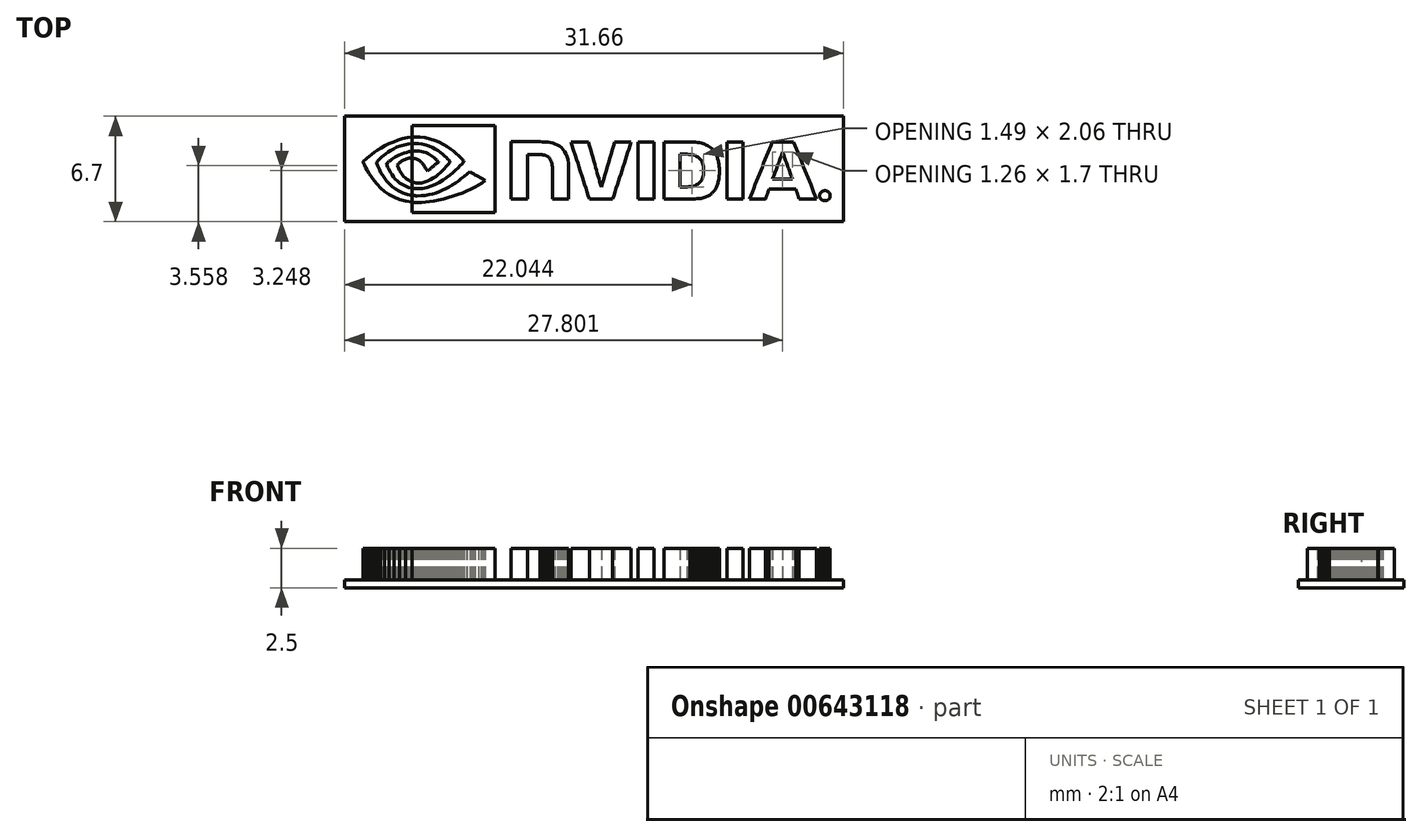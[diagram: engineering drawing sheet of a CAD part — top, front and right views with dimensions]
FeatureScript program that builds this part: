
annotation { "Feature Type Name" : "Feature", "Feature Type Description" : "" }
export const myFeature = defineFeature(function(context is Context, id is Id, definition is map)
    precondition{}
    {
        {
            var Q0;
            Q0=qCreatedBy(makeId("Top.planeOp"),FACE);
            var sketch = newSketch(context, id + "F0", { "sketchPlane" : qUnion([Q0])});
            skLineSegment(sketch, "E0", {"start": v(15, -1.7) * mm, "end": v(15, -1.67) * mm});
            skLineSegment(sketch, "E1", {"start": v(15, -1.67) * mm, "end": v(15, -1.63) * mm});
            skLineSegment(sketch, "E2", {"start": v(15, -1.63) * mm, "end": v(14.98, -1.6) * mm});
            skLineSegment(sketch, "E3", {"start": v(14.98, -1.6) * mm, "end": v(14.97, -1.57) * mm});
            skLineSegment(sketch, "E4", {"start": v(14.97, -1.57) * mm, "end": v(14.96, -1.54) * mm});
            skLineSegment(sketch, "E5", {"start": v(14.96, -1.54) * mm, "end": v(14.94, -1.51) * mm});
            skLineSegment(sketch, "E6", {"start": v(14.94, -1.51) * mm, "end": v(14.92, -1.49) * mm});
            skLineSegment(sketch, "E7", {"start": v(14.92, -1.49) * mm, "end": v(14.9, -1.47) * mm});
            skLineSegment(sketch, "E8", {"start": v(14.9, -1.47) * mm, "end": v(14.88, -1.45) * mm});
            skLineSegment(sketch, "E9", {"start": v(14.88, -1.45) * mm, "end": v(14.85, -1.43) * mm});
            skLineSegment(sketch, "E10", {"start": v(14.85, -1.43) * mm, "end": v(14.82, -1.42) * mm});
            skLineSegment(sketch, "E11", {"start": v(14.82, -1.42) * mm, "end": v(14.8, -1.4) * mm});
            skLineSegment(sketch, "E12", {"start": v(14.8, -1.4) * mm, "end": v(14.76, -1.4) * mm});
            skLineSegment(sketch, "E13", {"start": v(14.76, -1.4) * mm, "end": v(14.73, -1.39) * mm});
            skLineSegment(sketch, "E14", {"start": v(14.73, -1.39) * mm, "end": v(14.7, -1.38) * mm});
            skLineSegment(sketch, "E15", {"start": v(14.7, -1.38) * mm, "end": v(14.67, -1.38) * mm});
            skLineSegment(sketch, "E16", {"start": v(14.67, -1.38) * mm, "end": v(14.64, -1.38) * mm});
            skLineSegment(sketch, "E17", {"start": v(14.64, -1.38) * mm, "end": v(14.6, -1.39) * mm});
            skLineSegment(sketch, "E18", {"start": v(14.6, -1.39) * mm, "end": v(14.57, -1.4) * mm});
            skLineSegment(sketch, "E19", {"start": v(14.57, -1.4) * mm, "end": v(14.54, -1.4) * mm});
            skLineSegment(sketch, "E20", {"start": v(14.54, -1.4) * mm, "end": v(14.51, -1.42) * mm});
            skLineSegment(sketch, "E21", {"start": v(14.51, -1.42) * mm, "end": v(14.49, -1.43) * mm});
            skLineSegment(sketch, "E22", {"start": v(14.49, -1.43) * mm, "end": v(14.46, -1.45) * mm});
            skLineSegment(sketch, "E23", {"start": v(14.46, -1.45) * mm, "end": v(14.44, -1.47) * mm});
            skLineSegment(sketch, "E24", {"start": v(14.44, -1.47) * mm, "end": v(14.41, -1.49) * mm});
            skLineSegment(sketch, "E25", {"start": v(14.41, -1.49) * mm, "end": v(14.4, -1.51) * mm});
            skLineSegment(sketch, "E26", {"start": v(14.4, -1.51) * mm, "end": v(14.38, -1.54) * mm});
            skLineSegment(sketch, "E27", {"start": v(14.38, -1.54) * mm, "end": v(14.36, -1.57) * mm});
            skLineSegment(sketch, "E28", {"start": v(14.36, -1.57) * mm, "end": v(14.35, -1.6) * mm});
            skLineSegment(sketch, "E29", {"start": v(14.35, -1.6) * mm, "end": v(14.34, -1.63) * mm});
            skLineSegment(sketch, "E30", {"start": v(14.34, -1.63) * mm, "end": v(14.34, -1.67) * mm});
            skLineSegment(sketch, "E31", {"start": v(14.34, -1.67) * mm, "end": v(14.34, -1.7) * mm});
            skLineSegment(sketch, "E32", {"start": v(14.34, -1.7) * mm, "end": v(14.34, -1.74) * mm});
            skLineSegment(sketch, "E33", {"start": v(14.34, -1.74) * mm, "end": v(14.34, -1.77) * mm});
            skLineSegment(sketch, "E34", {"start": v(14.34, -1.77) * mm, "end": v(14.35, -1.8) * mm});
            skLineSegment(sketch, "E35", {"start": v(14.35, -1.8) * mm, "end": v(14.36, -1.84) * mm});
            skLineSegment(sketch, "E36", {"start": v(14.36, -1.84) * mm, "end": v(14.38, -1.87) * mm});
            skLineSegment(sketch, "E37", {"start": v(14.38, -1.87) * mm, "end": v(14.4, -1.9) * mm});
            skLineSegment(sketch, "E38", {"start": v(14.4, -1.9) * mm, "end": v(14.41, -1.92) * mm});
            skLineSegment(sketch, "E39", {"start": v(14.41, -1.92) * mm, "end": v(14.44, -1.94) * mm});
            skLineSegment(sketch, "E40", {"start": v(14.44, -1.94) * mm, "end": v(14.46, -1.96) * mm});
            skLineSegment(sketch, "E41", {"start": v(14.46, -1.96) * mm, "end": v(14.49, -1.97) * mm});
            skLineSegment(sketch, "E42", {"start": v(14.49, -1.97) * mm, "end": v(14.51, -1.99) * mm});
            skLineSegment(sketch, "E43", {"start": v(14.51, -1.99) * mm, "end": v(14.54, -2) * mm});
            skLineSegment(sketch, "E44", {"start": v(14.54, -2) * mm, "end": v(14.57, -2) * mm});
            skLineSegment(sketch, "E45", {"start": v(14.57, -2) * mm, "end": v(14.6, -2.02) * mm});
            skLineSegment(sketch, "E46", {"start": v(14.6, -2.02) * mm, "end": v(14.64, -2.02) * mm});
            skLineSegment(sketch, "E47", {"start": v(14.64, -2.02) * mm, "end": v(14.67, -2.02) * mm});
            skLineSegment(sketch, "E48", {"start": v(14.67, -2.02) * mm, "end": v(14.7, -2.02) * mm});
            skLineSegment(sketch, "E49", {"start": v(14.7, -2.02) * mm, "end": v(14.73, -2.02) * mm});
            skLineSegment(sketch, "E50", {"start": v(14.73, -2.02) * mm, "end": v(14.76, -2) * mm});
            skLineSegment(sketch, "E51", {"start": v(14.76, -2) * mm, "end": v(14.8, -2) * mm});
            skLineSegment(sketch, "E52", {"start": v(14.8, -2) * mm, "end": v(14.82, -1.99) * mm});
            skLineSegment(sketch, "E53", {"start": v(14.82, -1.99) * mm, "end": v(14.85, -1.97) * mm});
            skLineSegment(sketch, "E54", {"start": v(14.85, -1.97) * mm, "end": v(14.88, -1.96) * mm});
            skLineSegment(sketch, "E55", {"start": v(14.88, -1.96) * mm, "end": v(14.9, -1.94) * mm});
            skLineSegment(sketch, "E56", {"start": v(14.9, -1.94) * mm, "end": v(14.92, -1.92) * mm});
            skLineSegment(sketch, "E57", {"start": v(14.92, -1.92) * mm, "end": v(14.94, -1.9) * mm});
            skLineSegment(sketch, "E58", {"start": v(14.94, -1.9) * mm, "end": v(14.96, -1.87) * mm});
            skLineSegment(sketch, "E59", {"start": v(14.96, -1.87) * mm, "end": v(14.97, -1.84) * mm});
            skLineSegment(sketch, "E60", {"start": v(14.97, -1.84) * mm, "end": v(14.98, -1.8) * mm});
            skLineSegment(sketch, "E61", {"start": v(14.98, -1.8) * mm, "end": v(15, -1.77) * mm});
            skLineSegment(sketch, "E62", {"start": v(15, -1.77) * mm, "end": v(15, -1.74) * mm});
            skLineSegment(sketch, "E63", {"start": v(15, -1.74) * mm, "end": v(15, -1.7) * mm});
            skLineSegment(sketch, "E64", {"start": v(2.8, 1.72) * mm, "end": v(2.8, 1.5) * mm});
            skLineSegment(sketch, "E65", {"start": v(2.8, 1.5) * mm, "end": v(2.8, 1.27) * mm});
            skLineSegment(sketch, "E66", {"start": v(2.8, 1.27) * mm, "end": v(2.8, 1.04) * mm});
            skLineSegment(sketch, "E67", {"start": v(2.8, 1.04) * mm, "end": v(2.8, 0.81) * mm});
            skLineSegment(sketch, "E68", {"start": v(2.8, 0.81) * mm, "end": v(2.8, 0.59) * mm});
            skLineSegment(sketch, "E69", {"start": v(2.8, 0.59) * mm, "end": v(2.8, 0.36) * mm});
            skLineSegment(sketch, "E70", {"start": v(2.8, 0.36) * mm, "end": v(2.8, 0.13) * mm});
            skLineSegment(sketch, "E71", {"start": v(2.8, 0.13) * mm, "end": v(2.8, -0.1) * mm});
            skLineSegment(sketch, "E72", {"start": v(2.8, -0.1) * mm, "end": v(2.8, -0.32) * mm});
            skLineSegment(sketch, "E73", {"start": v(2.8, -0.32) * mm, "end": v(2.8, -0.55) * mm});
            skLineSegment(sketch, "E74", {"start": v(2.8, -0.55) * mm, "end": v(2.8, -0.78) * mm});
            skLineSegment(sketch, "E75", {"start": v(2.8, -0.78) * mm, "end": v(2.8, -1) * mm});
            skLineSegment(sketch, "E76", {"start": v(2.8, -1) * mm, "end": v(2.8, -1.23) * mm});
            skLineSegment(sketch, "E77", {"start": v(2.8, -1.23) * mm, "end": v(2.8, -1.46) * mm});
            skLineSegment(sketch, "E78", {"start": v(2.8, -1.46) * mm, "end": v(2.8, -1.68) * mm});
            skLineSegment(sketch, "E79", {"start": v(2.8, -1.68) * mm, "end": v(2.8, -1.91) * mm});
            skLineSegment(sketch, "E80", {"start": v(2.8, -1.91) * mm, "end": v(2.86, -1.91) * mm});
            skLineSegment(sketch, "E81", {"start": v(2.86, -1.91) * mm, "end": v(2.93, -1.91) * mm});
            skLineSegment(sketch, "E82", {"start": v(2.93, -1.91) * mm, "end": v(3, -1.91) * mm});
            skLineSegment(sketch, "E83", {"start": v(3, -1.91) * mm, "end": v(3.06, -1.91) * mm});
            skLineSegment(sketch, "E84", {"start": v(3.06, -1.91) * mm, "end": v(3.12, -1.91) * mm});
            skLineSegment(sketch, "E85", {"start": v(3.12, -1.91) * mm, "end": v(3.18, -1.91) * mm});
            skLineSegment(sketch, "E86", {"start": v(3.18, -1.91) * mm, "end": v(3.25, -1.91) * mm});
            skLineSegment(sketch, "E87", {"start": v(3.25, -1.91) * mm, "end": v(3.31, -1.91) * mm});
            skLineSegment(sketch, "E88", {"start": v(3.31, -1.91) * mm, "end": v(3.38, -1.91) * mm});
            skLineSegment(sketch, "E89", {"start": v(3.38, -1.91) * mm, "end": v(3.44, -1.91) * mm});
            skLineSegment(sketch, "E90", {"start": v(3.44, -1.91) * mm, "end": v(3.5, -1.91) * mm});
            skLineSegment(sketch, "E91", {"start": v(3.5, -1.91) * mm, "end": v(3.57, -1.91) * mm});
            skLineSegment(sketch, "E92", {"start": v(3.57, -1.91) * mm, "end": v(3.63, -1.91) * mm});
            skLineSegment(sketch, "E93", {"start": v(3.63, -1.91) * mm, "end": v(3.7, -1.91) * mm});
            skLineSegment(sketch, "E94", {"start": v(3.7, -1.91) * mm, "end": v(3.76, -1.91) * mm});
            skLineSegment(sketch, "E95", {"start": v(3.76, -1.91) * mm, "end": v(3.82, -1.91) * mm});
            skLineSegment(sketch, "E96", {"start": v(3.82, -1.91) * mm, "end": v(3.82, -1.68) * mm});
            skLineSegment(sketch, "E97", {"start": v(3.82, -1.68) * mm, "end": v(3.82, -1.46) * mm});
            skLineSegment(sketch, "E98", {"start": v(3.82, -1.46) * mm, "end": v(3.82, -1.23) * mm});
            skLineSegment(sketch, "E99", {"start": v(3.82, -1.23) * mm, "end": v(3.82, -1) * mm});
            skLineSegment(sketch, "E100", {"start": v(3.82, -1) * mm, "end": v(3.82, -0.78) * mm});
            skLineSegment(sketch, "E101", {"start": v(3.82, -0.78) * mm, "end": v(3.82, -0.55) * mm});
            skLineSegment(sketch, "E102", {"start": v(3.82, -0.55) * mm, "end": v(3.82, -0.32) * mm});
            skLineSegment(sketch, "E103", {"start": v(3.82, -0.32) * mm, "end": v(3.82, -0.1) * mm});
            skLineSegment(sketch, "E104", {"start": v(3.82, -0.1) * mm, "end": v(3.82, 0.13) * mm});
            skLineSegment(sketch, "E105", {"start": v(3.82, 0.13) * mm, "end": v(3.82, 0.36) * mm});
            skLineSegment(sketch, "E106", {"start": v(3.82, 0.36) * mm, "end": v(3.82, 0.59) * mm});
            skLineSegment(sketch, "E107", {"start": v(3.82, 0.59) * mm, "end": v(3.82, 0.81) * mm});
            skLineSegment(sketch, "E108", {"start": v(3.82, 0.81) * mm, "end": v(3.82, 1.04) * mm});
            skLineSegment(sketch, "E109", {"start": v(3.82, 1.04) * mm, "end": v(3.82, 1.27) * mm});
            skLineSegment(sketch, "E110", {"start": v(3.82, 1.27) * mm, "end": v(3.82, 1.5) * mm});
            skLineSegment(sketch, "E111", {"start": v(3.82, 1.5) * mm, "end": v(3.82, 1.72) * mm});
            skLineSegment(sketch, "E112", {"start": v(3.82, 1.72) * mm, "end": v(3.76, 1.72) * mm});
            skLineSegment(sketch, "E113", {"start": v(3.76, 1.72) * mm, "end": v(3.7, 1.72) * mm});
            skLineSegment(sketch, "E114", {"start": v(3.7, 1.72) * mm, "end": v(3.63, 1.72) * mm});
            skLineSegment(sketch, "E115", {"start": v(3.63, 1.72) * mm, "end": v(3.57, 1.72) * mm});
            skLineSegment(sketch, "E116", {"start": v(3.57, 1.72) * mm, "end": v(3.5, 1.72) * mm});
            skLineSegment(sketch, "E117", {"start": v(3.5, 1.72) * mm, "end": v(3.44, 1.72) * mm});
            skLineSegment(sketch, "E118", {"start": v(3.44, 1.72) * mm, "end": v(3.37, 1.72) * mm});
            skLineSegment(sketch, "E119", {"start": v(3.37, 1.72) * mm, "end": v(3.31, 1.72) * mm});
            skLineSegment(sketch, "E120", {"start": v(3.31, 1.72) * mm, "end": v(3.25, 1.72) * mm});
            skLineSegment(sketch, "E121", {"start": v(3.25, 1.72) * mm, "end": v(3.18, 1.72) * mm});
            skLineSegment(sketch, "E122", {"start": v(3.18, 1.72) * mm, "end": v(3.12, 1.72) * mm});
            skLineSegment(sketch, "E123", {"start": v(3.12, 1.72) * mm, "end": v(3.05, 1.72) * mm});
            skLineSegment(sketch, "E124", {"start": v(3.05, 1.72) * mm, "end": v(3, 1.72) * mm});
            skLineSegment(sketch, "E125", {"start": v(3, 1.72) * mm, "end": v(2.93, 1.72) * mm});
            skLineSegment(sketch, "E126", {"start": v(2.93, 1.72) * mm, "end": v(2.86, 1.72) * mm});
            skLineSegment(sketch, "E127", {"start": v(2.86, 1.72) * mm, "end": v(2.8, 1.72) * mm});
            skLineSegment(sketch, "E128", {"start": v(-5.27, 1.73) * mm, "end": v(-5.27, 1.5) * mm});
            skLineSegment(sketch, "E129", {"start": v(-5.27, 1.5) * mm, "end": v(-5.27, 1.27) * mm});
            skLineSegment(sketch, "E130", {"start": v(-5.27, 1.27) * mm, "end": v(-5.27, 1.04) * mm});
            skLineSegment(sketch, "E131", {"start": v(-5.27, 1.04) * mm, "end": v(-5.27, 0.82) * mm});
            skLineSegment(sketch, "E132", {"start": v(-5.27, 0.82) * mm, "end": v(-5.27, 0.59) * mm});
            skLineSegment(sketch, "E133", {"start": v(-5.27, 0.59) * mm, "end": v(-5.27, 0.36) * mm});
            skLineSegment(sketch, "E134", {"start": v(-5.27, 0.36) * mm, "end": v(-5.27, 0.14) * mm});
            skLineSegment(sketch, "E135", {"start": v(-5.27, 0.14) * mm, "end": v(-5.27, -0.1) * mm});
            skLineSegment(sketch, "E136", {"start": v(-5.27, -0.1) * mm, "end": v(-5.27, -0.32) * mm});
            skLineSegment(sketch, "E137", {"start": v(-5.27, -0.32) * mm, "end": v(-5.27, -0.55) * mm});
            skLineSegment(sketch, "E138", {"start": v(-5.27, -0.55) * mm, "end": v(-5.27, -0.77) * mm});
            skLineSegment(sketch, "E139", {"start": v(-5.27, -0.77) * mm, "end": v(-5.27, -1) * mm});
            skLineSegment(sketch, "E140", {"start": v(-5.27, -1) * mm, "end": v(-5.27, -1.23) * mm});
            skLineSegment(sketch, "E141", {"start": v(-5.27, -1.23) * mm, "end": v(-5.27, -1.46) * mm});
            skLineSegment(sketch, "E142", {"start": v(-5.27, -1.46) * mm, "end": v(-5.27, -1.68) * mm});
            skLineSegment(sketch, "E143", {"start": v(-5.27, -1.68) * mm, "end": v(-5.27, -1.91) * mm});
            skLineSegment(sketch, "E144", {"start": v(-5.27, -1.91) * mm, "end": v(-5.2, -1.91) * mm});
            skLineSegment(sketch, "E145", {"start": v(-5.2, -1.91) * mm, "end": v(-5.14, -1.91) * mm});
            skLineSegment(sketch, "E146", {"start": v(-5.14, -1.91) * mm, "end": v(-5.07, -1.91) * mm});
            skLineSegment(sketch, "E147", {"start": v(-5.07, -1.91) * mm, "end": v(-5, -1.91) * mm});
            skLineSegment(sketch, "E148", {"start": v(-5, -1.91) * mm, "end": v(-4.94, -1.91) * mm});
            skLineSegment(sketch, "E149", {"start": v(-4.94, -1.91) * mm, "end": v(-4.88, -1.91) * mm});
            skLineSegment(sketch, "E150", {"start": v(-4.88, -1.91) * mm, "end": v(-4.82, -1.91) * mm});
            skLineSegment(sketch, "E151", {"start": v(-4.82, -1.91) * mm, "end": v(-4.75, -1.91) * mm});
            skLineSegment(sketch, "E152", {"start": v(-4.75, -1.91) * mm, "end": v(-4.69, -1.91) * mm});
            skLineSegment(sketch, "E153", {"start": v(-4.69, -1.91) * mm, "end": v(-4.62, -1.91) * mm});
            skLineSegment(sketch, "E154", {"start": v(-4.62, -1.91) * mm, "end": v(-4.56, -1.91) * mm});
            skLineSegment(sketch, "E155", {"start": v(-4.56, -1.91) * mm, "end": v(-4.5, -1.91) * mm});
            skLineSegment(sketch, "E156", {"start": v(-4.5, -1.91) * mm, "end": v(-4.43, -1.91) * mm});
            skLineSegment(sketch, "E157", {"start": v(-4.43, -1.91) * mm, "end": v(-4.36, -1.91) * mm});
            skLineSegment(sketch, "E158", {"start": v(-4.36, -1.91) * mm, "end": v(-4.3, -1.91) * mm});
            skLineSegment(sketch, "E159", {"start": v(-4.3, -1.91) * mm, "end": v(-4.23, -1.91) * mm});
            skLineSegment(sketch, "E160", {"start": v(-4.23, -1.91) * mm, "end": v(-4.23, -1.73) * mm});
            skLineSegment(sketch, "E161", {"start": v(-4.23, -1.73) * mm, "end": v(-4.23, -1.56) * mm});
            skLineSegment(sketch, "E162", {"start": v(-4.23, -1.56) * mm, "end": v(-4.23, -1.38) * mm});
            skLineSegment(sketch, "E163", {"start": v(-4.23, -1.38) * mm, "end": v(-4.23, -1.2) * mm});
            skLineSegment(sketch, "E164", {"start": v(-4.23, -1.2) * mm, "end": v(-4.23, -1.03) * mm});
            skLineSegment(sketch, "E165", {"start": v(-4.23, -1.03) * mm, "end": v(-4.23, -0.85) * mm});
            skLineSegment(sketch, "E166", {"start": v(-4.23, -0.85) * mm, "end": v(-4.23, -0.68) * mm});
            skLineSegment(sketch, "E167", {"start": v(-4.23, -0.68) * mm, "end": v(-4.23, -0.5) * mm});
            skLineSegment(sketch, "E168", {"start": v(-4.23, -0.5) * mm, "end": v(-4.23, -0.32) * mm});
            skLineSegment(sketch, "E169", {"start": v(-4.23, -0.32) * mm, "end": v(-4.23, -0.15) * mm});
            skLineSegment(sketch, "E170", {"start": v(-4.23, -0.15) * mm, "end": v(-4.23, 0.03) * mm});
            skLineSegment(sketch, "E171", {"start": v(-4.23, 0.03) * mm, "end": v(-4.23, 0.2) * mm});
            skLineSegment(sketch, "E172", {"start": v(-4.23, 0.2) * mm, "end": v(-4.23, 0.38) * mm});
            skLineSegment(sketch, "E173", {"start": v(-4.23, 0.38) * mm, "end": v(-4.23, 0.56) * mm});
            skLineSegment(sketch, "E174", {"start": v(-4.23, 0.56) * mm, "end": v(-4.23, 0.74) * mm});
            skLineSegment(sketch, "E175", {"start": v(-4.23, 0.74) * mm, "end": v(-4.23, 0.91) * mm});
            skLineSegment(sketch, "E176", {"start": v(-4.23, 0.91) * mm, "end": v(-4.18, 0.91) * mm});
            skLineSegment(sketch, "E177", {"start": v(-4.18, 0.91) * mm, "end": v(-4.13, 0.91) * mm});
            skLineSegment(sketch, "E178", {"start": v(-4.13, 0.91) * mm, "end": v(-4.08, 0.91) * mm});
            skLineSegment(sketch, "E179", {"start": v(-4.08, 0.91) * mm, "end": v(-4.03, 0.91) * mm});
            skLineSegment(sketch, "E180", {"start": v(-4.03, 0.91) * mm, "end": v(-3.98, 0.91) * mm});
            skLineSegment(sketch, "E181", {"start": v(-3.98, 0.91) * mm, "end": v(-3.93, 0.91) * mm});
            skLineSegment(sketch, "E182", {"start": v(-3.93, 0.91) * mm, "end": v(-3.88, 0.91) * mm});
            skLineSegment(sketch, "E183", {"start": v(-3.88, 0.91) * mm, "end": v(-3.83, 0.91) * mm});
            skLineSegment(sketch, "E184", {"start": v(-3.83, 0.91) * mm, "end": v(-3.78, 0.91) * mm});
            skLineSegment(sketch, "E185", {"start": v(-3.78, 0.91) * mm, "end": v(-3.73, 0.91) * mm});
            skLineSegment(sketch, "E186", {"start": v(-3.73, 0.91) * mm, "end": v(-3.68, 0.91) * mm});
            skLineSegment(sketch, "E187", {"start": v(-3.68, 0.91) * mm, "end": v(-3.63, 0.91) * mm});
            skLineSegment(sketch, "E188", {"start": v(-3.63, 0.91) * mm, "end": v(-3.58, 0.9) * mm});
            skLineSegment(sketch, "E189", {"start": v(-3.58, 0.9) * mm, "end": v(-3.53, 0.9) * mm});
            skLineSegment(sketch, "E190", {"start": v(-3.53, 0.9) * mm, "end": v(-3.48, 0.9) * mm});
            skLineSegment(sketch, "E191", {"start": v(-3.48, 0.9) * mm, "end": v(-3.43, 0.9) * mm});
            skLineSegment(sketch, "E192", {"start": v(-3.43, 0.9) * mm, "end": v(-3.38, 0.9) * mm});
            skLineSegment(sketch, "E193", {"start": v(-3.38, 0.9) * mm, "end": v(-3.33, 0.9) * mm});
            skLineSegment(sketch, "E194", {"start": v(-3.33, 0.9) * mm, "end": v(-3.29, 0.9) * mm});
            skLineSegment(sketch, "E195", {"start": v(-3.29, 0.9) * mm, "end": v(-3.24, 0.9) * mm});
            skLineSegment(sketch, "E196", {"start": v(-3.24, 0.9) * mm, "end": v(-3.2, 0.9) * mm});
            skLineSegment(sketch, "E197", {"start": v(-3.2, 0.9) * mm, "end": v(-3.16, 0.88) * mm});
            skLineSegment(sketch, "E198", {"start": v(-3.16, 0.88) * mm, "end": v(-3.12, 0.87) * mm});
            skLineSegment(sketch, "E199", {"start": v(-3.12, 0.87) * mm, "end": v(-3.09, 0.86) * mm});
            skLineSegment(sketch, "E200", {"start": v(-3.09, 0.86) * mm, "end": v(-3.05, 0.85) * mm});
            skLineSegment(sketch, "E201", {"start": v(-3.05, 0.85) * mm, "end": v(-3.02, 0.83) * mm});
            skLineSegment(sketch, "E202", {"start": v(-3.02, 0.83) * mm, "end": v(-2.99, 0.82) * mm});
            skLineSegment(sketch, "E203", {"start": v(-2.99, 0.82) * mm, "end": v(-2.96, 0.8) * mm});
            skLineSegment(sketch, "E204", {"start": v(-2.96, 0.8) * mm, "end": v(-2.93, 0.78) * mm});
            skLineSegment(sketch, "E205", {"start": v(-2.93, 0.78) * mm, "end": v(-2.9, 0.76) * mm});
            skLineSegment(sketch, "E206", {"start": v(-2.9, 0.76) * mm, "end": v(-2.87, 0.73) * mm});
            skLineSegment(sketch, "E207", {"start": v(-2.87, 0.73) * mm, "end": v(-2.85, 0.7) * mm});
            skLineSegment(sketch, "E208", {"start": v(-2.85, 0.7) * mm, "end": v(-2.82, 0.68) * mm});
            skLineSegment(sketch, "E209", {"start": v(-2.82, 0.68) * mm, "end": v(-2.8, 0.64) * mm});
            skLineSegment(sketch, "E210", {"start": v(-2.8, 0.64) * mm, "end": v(-2.77, 0.6) * mm});
            skLineSegment(sketch, "E211", {"start": v(-2.77, 0.6) * mm, "end": v(-2.75, 0.56) * mm});
            skLineSegment(sketch, "E212", {"start": v(-2.75, 0.56) * mm, "end": v(-2.72, 0.51) * mm});
            skLineSegment(sketch, "E213", {"start": v(-2.72, 0.51) * mm, "end": v(-2.7, 0.46) * mm});
            skLineSegment(sketch, "E214", {"start": v(-2.7, 0.46) * mm, "end": v(-2.69, 0.41) * mm});
            skLineSegment(sketch, "E215", {"start": v(-2.69, 0.41) * mm, "end": v(-2.67, 0.36) * mm});
            skLineSegment(sketch, "E216", {"start": v(-2.67, 0.36) * mm, "end": v(-2.66, 0.3) * mm});
            skLineSegment(sketch, "E217", {"start": v(-2.66, 0.3) * mm, "end": v(-2.65, 0.23) * mm});
            skLineSegment(sketch, "E218", {"start": v(-2.65, 0.23) * mm, "end": v(-2.64, 0.16) * mm});
            skLineSegment(sketch, "E219", {"start": v(-2.64, 0.16) * mm, "end": v(-2.63, 0.09) * mm});
            skLineSegment(sketch, "E220", {"start": v(-2.63, 0.09) * mm, "end": v(-2.63, 0.01) * mm});
            skLineSegment(sketch, "E221", {"start": v(-2.63, 0.01) * mm, "end": v(-2.62, -0.07) * mm});
            skLineSegment(sketch, "E222", {"start": v(-2.62, -0.07) * mm, "end": v(-2.62, -0.16) * mm});
            skLineSegment(sketch, "E223", {"start": v(-2.62, -0.16) * mm, "end": v(-2.62, -0.25) * mm});
            skLineSegment(sketch, "E224", {"start": v(-2.62, -0.25) * mm, "end": v(-2.62, -0.36) * mm});
            skLineSegment(sketch, "E225", {"start": v(-2.62, -0.36) * mm, "end": v(-2.62, -0.46) * mm});
            skLineSegment(sketch, "E226", {"start": v(-2.62, -0.46) * mm, "end": v(-2.62, -0.56) * mm});
            skLineSegment(sketch, "E227", {"start": v(-2.62, -0.56) * mm, "end": v(-2.62, -0.67) * mm});
            skLineSegment(sketch, "E228", {"start": v(-2.62, -0.67) * mm, "end": v(-2.62, -0.77) * mm});
            skLineSegment(sketch, "E229", {"start": v(-2.62, -0.77) * mm, "end": v(-2.62, -0.87) * mm});
            skLineSegment(sketch, "E230", {"start": v(-2.62, -0.87) * mm, "end": v(-2.62, -0.98) * mm});
            skLineSegment(sketch, "E231", {"start": v(-2.62, -0.98) * mm, "end": v(-2.62, -1.08) * mm});
            skLineSegment(sketch, "E232", {"start": v(-2.62, -1.08) * mm, "end": v(-2.62, -1.18) * mm});
            skLineSegment(sketch, "E233", {"start": v(-2.62, -1.18) * mm, "end": v(-2.62, -1.29) * mm});
            skLineSegment(sketch, "E234", {"start": v(-2.62, -1.29) * mm, "end": v(-2.62, -1.4) * mm});
            skLineSegment(sketch, "E235", {"start": v(-2.62, -1.4) * mm, "end": v(-2.62, -1.5) * mm});
            skLineSegment(sketch, "E236", {"start": v(-2.62, -1.5) * mm, "end": v(-2.62, -1.6) * mm});
            skLineSegment(sketch, "E237", {"start": v(-2.62, -1.6) * mm, "end": v(-2.62, -1.7) * mm});
            skLineSegment(sketch, "E238", {"start": v(-2.62, -1.7) * mm, "end": v(-2.62, -1.8) * mm});
            skLineSegment(sketch, "E239", {"start": v(-2.62, -1.8) * mm, "end": v(-2.62, -1.91) * mm});
            skLineSegment(sketch, "E240", {"start": v(-2.62, -1.91) * mm, "end": v(-2.56, -1.91) * mm});
            skLineSegment(sketch, "E241", {"start": v(-2.56, -1.91) * mm, "end": v(-2.5, -1.91) * mm});
            skLineSegment(sketch, "E242", {"start": v(-2.5, -1.91) * mm, "end": v(-2.43, -1.91) * mm});
            skLineSegment(sketch, "E243", {"start": v(-2.43, -1.91) * mm, "end": v(-2.37, -1.91) * mm});
            skLineSegment(sketch, "E244", {"start": v(-2.37, -1.91) * mm, "end": v(-2.3, -1.91) * mm});
            skLineSegment(sketch, "E245", {"start": v(-2.3, -1.91) * mm, "end": v(-2.25, -1.91) * mm});
            skLineSegment(sketch, "E246", {"start": v(-2.25, -1.91) * mm, "end": v(-2.18, -1.91) * mm});
            skLineSegment(sketch, "E247", {"start": v(-2.18, -1.91) * mm, "end": v(-2.12, -1.91) * mm});
            skLineSegment(sketch, "E248", {"start": v(-2.12, -1.91) * mm, "end": v(-2.06, -1.91) * mm});
            skLineSegment(sketch, "E249", {"start": v(-2.06, -1.91) * mm, "end": v(-2, -1.91) * mm});
            skLineSegment(sketch, "E250", {"start": v(-2, -1.91) * mm, "end": v(-1.93, -1.91) * mm});
            skLineSegment(sketch, "E251", {"start": v(-1.93, -1.91) * mm, "end": v(-1.87, -1.91) * mm});
            skLineSegment(sketch, "E252", {"start": v(-1.87, -1.91) * mm, "end": v(-1.8, -1.91) * mm});
            skLineSegment(sketch, "E253", {"start": v(-1.8, -1.91) * mm, "end": v(-1.74, -1.91) * mm});
            skLineSegment(sketch, "E254", {"start": v(-1.74, -1.91) * mm, "end": v(-1.68, -1.91) * mm});
            skLineSegment(sketch, "E255", {"start": v(-1.68, -1.91) * mm, "end": v(-1.62, -1.91) * mm});
            skLineSegment(sketch, "E256", {"start": v(-1.62, -1.91) * mm, "end": v(-1.62, -1.78) * mm});
            skLineSegment(sketch, "E257", {"start": v(-1.62, -1.78) * mm, "end": v(-1.62, -1.66) * mm});
            skLineSegment(sketch, "E258", {"start": v(-1.62, -1.66) * mm, "end": v(-1.62, -1.53) * mm});
            skLineSegment(sketch, "E259", {"start": v(-1.62, -1.53) * mm, "end": v(-1.62, -1.4) * mm});
            skLineSegment(sketch, "E260", {"start": v(-1.62, -1.4) * mm, "end": v(-1.62, -1.28) * mm});
            skLineSegment(sketch, "E261", {"start": v(-1.62, -1.28) * mm, "end": v(-1.62, -1.16) * mm});
            skLineSegment(sketch, "E262", {"start": v(-1.62, -1.16) * mm, "end": v(-1.62, -1.03) * mm});
            skLineSegment(sketch, "E263", {"start": v(-1.62, -1.03) * mm, "end": v(-1.62, -0.9) * mm});
            skLineSegment(sketch, "E264", {"start": v(-1.62, -0.9) * mm, "end": v(-1.62, -0.78) * mm});
            skLineSegment(sketch, "E265", {"start": v(-1.62, -0.78) * mm, "end": v(-1.62, -0.65) * mm});
            skLineSegment(sketch, "E266", {"start": v(-1.62, -0.65) * mm, "end": v(-1.62, -0.53) * mm});
            skLineSegment(sketch, "E267", {"start": v(-1.62, -0.53) * mm, "end": v(-1.62, -0.4) * mm});
            skLineSegment(sketch, "E268", {"start": v(-1.62, -0.4) * mm, "end": v(-1.62, -0.28) * mm});
            skLineSegment(sketch, "E269", {"start": v(-1.62, -0.28) * mm, "end": v(-1.62, -0.15) * mm});
            skLineSegment(sketch, "E270", {"start": v(-1.62, -0.15) * mm, "end": v(-1.62, -0.03) * mm});
            skLineSegment(sketch, "E271", {"start": v(-1.62, -0.03) * mm, "end": v(-1.62, 0.1) * mm});
            skLineSegment(sketch, "E272", {"start": v(-1.62, 0.1) * mm, "end": v(-1.63, 0.35) * mm});
            skLineSegment(sketch, "E273", {"start": v(-1.63, 0.35) * mm, "end": v(-1.66, 0.58) * mm});
            skLineSegment(sketch, "E274", {"start": v(-1.66, 0.58) * mm, "end": v(-1.7, 0.78) * mm});
            skLineSegment(sketch, "E275", {"start": v(-1.7, 0.78) * mm, "end": v(-1.78, 0.96) * mm});
            skLineSegment(sketch, "E276", {"start": v(-1.78, 0.96) * mm, "end": v(-1.86, 1.11) * mm});
            skLineSegment(sketch, "E277", {"start": v(-1.86, 1.11) * mm, "end": v(-1.96, 1.24) * mm});
            skLineSegment(sketch, "E278", {"start": v(-1.96, 1.24) * mm, "end": v(-2.07, 1.36) * mm});
            skLineSegment(sketch, "E279", {"start": v(-2.07, 1.36) * mm, "end": v(-2.19, 1.45) * mm});
            skLineSegment(sketch, "E280", {"start": v(-2.19, 1.45) * mm, "end": v(-2.32, 1.53) * mm});
            skLineSegment(sketch, "E281", {"start": v(-2.32, 1.53) * mm, "end": v(-2.46, 1.59) * mm});
            skLineSegment(sketch, "E282", {"start": v(-2.46, 1.59) * mm, "end": v(-2.61, 1.64) * mm});
            skLineSegment(sketch, "E283", {"start": v(-2.61, 1.64) * mm, "end": v(-2.77, 1.67) * mm});
            skLineSegment(sketch, "E284", {"start": v(-2.77, 1.67) * mm, "end": v(-2.93, 1.7) * mm});
            skLineSegment(sketch, "E285", {"start": v(-2.93, 1.7) * mm, "end": v(-3.1, 1.71) * mm});
            skLineSegment(sketch, "E286", {"start": v(-3.1, 1.71) * mm, "end": v(-3.26, 1.72) * mm});
            skLineSegment(sketch, "E287", {"start": v(-3.26, 1.72) * mm, "end": v(-3.43, 1.73) * mm});
            skLineSegment(sketch, "E288", {"start": v(-3.43, 1.73) * mm, "end": v(-3.54, 1.73) * mm});
            skLineSegment(sketch, "E289", {"start": v(-3.54, 1.73) * mm, "end": v(-3.66, 1.73) * mm});
            skLineSegment(sketch, "E290", {"start": v(-3.66, 1.73) * mm, "end": v(-3.77, 1.73) * mm});
            skLineSegment(sketch, "E291", {"start": v(-3.77, 1.73) * mm, "end": v(-3.89, 1.73) * mm});
            skLineSegment(sketch, "E292", {"start": v(-3.89, 1.73) * mm, "end": v(-4, 1.73) * mm});
            skLineSegment(sketch, "E293", {"start": v(-4, 1.73) * mm, "end": v(-4.12, 1.73) * mm});
            skLineSegment(sketch, "E294", {"start": v(-4.12, 1.73) * mm, "end": v(-4.23, 1.73) * mm});
            skLineSegment(sketch, "E295", {"start": v(-4.23, 1.73) * mm, "end": v(-4.35, 1.73) * mm});
            skLineSegment(sketch, "E296", {"start": v(-4.35, 1.73) * mm, "end": v(-4.46, 1.73) * mm});
            skLineSegment(sketch, "E297", {"start": v(-4.46, 1.73) * mm, "end": v(-4.58, 1.73) * mm});
            skLineSegment(sketch, "E298", {"start": v(-4.58, 1.73) * mm, "end": v(-4.7, 1.73) * mm});
            skLineSegment(sketch, "E299", {"start": v(-4.7, 1.73) * mm, "end": v(-4.8, 1.73) * mm});
            skLineSegment(sketch, "E300", {"start": v(-4.8, 1.73) * mm, "end": v(-4.92, 1.73) * mm});
            skLineSegment(sketch, "E301", {"start": v(-4.92, 1.73) * mm, "end": v(-5.04, 1.73) * mm});
            skLineSegment(sketch, "E302", {"start": v(-5.04, 1.73) * mm, "end": v(-5.15, 1.73) * mm});
            skLineSegment(sketch, "E303", {"start": v(-5.15, 1.73) * mm, "end": v(-5.27, 1.73) * mm});
            skLineSegment(sketch, "E304", {"start": v(4.45, 1.72) * mm, "end": v(4.45, 1.5) * mm});
            skLineSegment(sketch, "E305", {"start": v(4.45, 1.5) * mm, "end": v(4.45, 1.27) * mm});
            skLineSegment(sketch, "E306", {"start": v(4.45, 1.27) * mm, "end": v(4.45, 1.04) * mm});
            skLineSegment(sketch, "E307", {"start": v(4.45, 1.04) * mm, "end": v(4.45, 0.81) * mm});
            skLineSegment(sketch, "E308", {"start": v(4.45, 0.81) * mm, "end": v(4.45, 0.59) * mm});
            skLineSegment(sketch, "E309", {"start": v(4.45, 0.59) * mm, "end": v(4.45, 0.36) * mm});
            skLineSegment(sketch, "E310", {"start": v(4.45, 0.36) * mm, "end": v(4.45, 0.13) * mm});
            skLineSegment(sketch, "E311", {"start": v(4.45, 0.13) * mm, "end": v(4.45, -0.1) * mm});
            skLineSegment(sketch, "E312", {"start": v(4.45, -0.1) * mm, "end": v(4.45, -0.32) * mm});
            skLineSegment(sketch, "E313", {"start": v(4.45, -0.32) * mm, "end": v(4.45, -0.55) * mm});
            skLineSegment(sketch, "E314", {"start": v(4.45, -0.55) * mm, "end": v(4.45, -0.78) * mm});
            skLineSegment(sketch, "E315", {"start": v(4.45, -0.78) * mm, "end": v(4.45, -1) * mm});
            skLineSegment(sketch, "E316", {"start": v(4.45, -1) * mm, "end": v(4.45, -1.23) * mm});
            skLineSegment(sketch, "E317", {"start": v(4.45, -1.23) * mm, "end": v(4.45, -1.46) * mm});
            skLineSegment(sketch, "E318", {"start": v(4.45, -1.46) * mm, "end": v(4.45, -1.68) * mm});
            skLineSegment(sketch, "E319", {"start": v(4.45, -1.68) * mm, "end": v(4.45, -1.91) * mm});
            skLineSegment(sketch, "E320", {"start": v(4.45, -1.91) * mm, "end": v(4.55, -1.91) * mm});
            skLineSegment(sketch, "E321", {"start": v(4.55, -1.91) * mm, "end": v(4.66, -1.91) * mm});
            skLineSegment(sketch, "E322", {"start": v(4.66, -1.91) * mm, "end": v(4.76, -1.91) * mm});
            skLineSegment(sketch, "E323", {"start": v(4.76, -1.91) * mm, "end": v(4.86, -1.91) * mm});
            skLineSegment(sketch, "E324", {"start": v(4.86, -1.91) * mm, "end": v(4.97, -1.91) * mm});
            skLineSegment(sketch, "E325", {"start": v(4.97, -1.91) * mm, "end": v(5.07, -1.91) * mm});
            skLineSegment(sketch, "E326", {"start": v(5.07, -1.91) * mm, "end": v(5.18, -1.91) * mm});
            skLineSegment(sketch, "E327", {"start": v(5.18, -1.91) * mm, "end": v(5.28, -1.91) * mm});
            skLineSegment(sketch, "E328", {"start": v(5.28, -1.91) * mm, "end": v(5.38, -1.91) * mm});
            skLineSegment(sketch, "E329", {"start": v(5.38, -1.91) * mm, "end": v(5.49, -1.91) * mm});
            skLineSegment(sketch, "E330", {"start": v(5.49, -1.91) * mm, "end": v(5.6, -1.91) * mm});
            skLineSegment(sketch, "E331", {"start": v(5.6, -1.91) * mm, "end": v(5.7, -1.91) * mm});
            skLineSegment(sketch, "E332", {"start": v(5.7, -1.91) * mm, "end": v(5.8, -1.91) * mm});
            skLineSegment(sketch, "E333", {"start": v(5.8, -1.91) * mm, "end": v(5.9, -1.91) * mm});
            skLineSegment(sketch, "E334", {"start": v(5.9, -1.91) * mm, "end": v(6, -1.91) * mm});
            skLineSegment(sketch, "E335", {"start": v(6, -1.91) * mm, "end": v(6.11, -1.91) * mm});
            skLineSegment(sketch, "E336", {"start": v(6.11, -1.91) * mm, "end": v(6.27, -1.9) * mm});
            skLineSegment(sketch, "E337", {"start": v(6.27, -1.9) * mm, "end": v(6.42, -1.9) * mm});
            skLineSegment(sketch, "E338", {"start": v(6.42, -1.9) * mm, "end": v(6.55, -1.9) * mm});
            skLineSegment(sketch, "E339", {"start": v(6.55, -1.9) * mm, "end": v(6.67, -1.88) * mm});
            skLineSegment(sketch, "E340", {"start": v(6.67, -1.88) * mm, "end": v(6.79, -1.87) * mm});
            skLineSegment(sketch, "E341", {"start": v(6.79, -1.87) * mm, "end": v(6.9, -1.85) * mm});
            skLineSegment(sketch, "E342", {"start": v(6.9, -1.85) * mm, "end": v(6.98, -1.82) * mm});
            skLineSegment(sketch, "E343", {"start": v(6.98, -1.82) * mm, "end": v(7.07, -1.8) * mm});
            skLineSegment(sketch, "E344", {"start": v(7.07, -1.8) * mm, "end": v(7.15, -1.76) * mm});
            skLineSegment(sketch, "E345", {"start": v(7.15, -1.76) * mm, "end": v(7.23, -1.73) * mm});
            skLineSegment(sketch, "E346", {"start": v(7.23, -1.73) * mm, "end": v(7.3, -1.69) * mm});
            skLineSegment(sketch, "E347", {"start": v(7.3, -1.69) * mm, "end": v(7.36, -1.65) * mm});
            skLineSegment(sketch, "E348", {"start": v(7.36, -1.65) * mm, "end": v(7.42, -1.6) * mm});
            skLineSegment(sketch, "E349", {"start": v(7.42, -1.6) * mm, "end": v(7.48, -1.55) * mm});
            skLineSegment(sketch, "E350", {"start": v(7.48, -1.55) * mm, "end": v(7.54, -1.5) * mm});
            skLineSegment(sketch, "E351", {"start": v(7.54, -1.5) * mm, "end": v(7.6, -1.43) * mm});
            skLineSegment(sketch, "E352", {"start": v(7.6, -1.43) * mm, "end": v(7.64, -1.39) * mm});
            skLineSegment(sketch, "E353", {"start": v(7.64, -1.39) * mm, "end": v(7.68, -1.33) * mm});
            skLineSegment(sketch, "E354", {"start": v(7.68, -1.33) * mm, "end": v(7.72, -1.27) * mm});
            skLineSegment(sketch, "E355", {"start": v(7.72, -1.27) * mm, "end": v(7.75, -1.2) * mm});
            skLineSegment(sketch, "E356", {"start": v(7.75, -1.2) * mm, "end": v(7.78, -1.14) * mm});
            skLineSegment(sketch, "E357", {"start": v(7.78, -1.14) * mm, "end": v(7.81, -1.07) * mm});
            skLineSegment(sketch, "E358", {"start": v(7.81, -1.07) * mm, "end": v(7.84, -0.99) * mm});
            skLineSegment(sketch, "E359", {"start": v(7.84, -0.99) * mm, "end": v(7.87, -0.9) * mm});
            skLineSegment(sketch, "E360", {"start": v(7.87, -0.9) * mm, "end": v(7.89, -0.82) * mm});
            skLineSegment(sketch, "E361", {"start": v(7.89, -0.82) * mm, "end": v(7.9, -0.73) * mm});
            skLineSegment(sketch, "E362", {"start": v(7.9, -0.73) * mm, "end": v(7.92, -0.64) * mm});
            skLineSegment(sketch, "E363", {"start": v(7.92, -0.64) * mm, "end": v(7.94, -0.54) * mm});
            skLineSegment(sketch, "E364", {"start": v(7.94, -0.54) * mm, "end": v(7.95, -0.44) * mm});
            skLineSegment(sketch, "E365", {"start": v(7.95, -0.44) * mm, "end": v(7.96, -0.34) * mm});
            skLineSegment(sketch, "E366", {"start": v(7.96, -0.34) * mm, "end": v(7.96, -0.24) * mm});
            skLineSegment(sketch, "E367", {"start": v(7.96, -0.24) * mm, "end": v(7.96, -0.13) * mm});
            skLineSegment(sketch, "E368", {"start": v(7.96, -0.13) * mm, "end": v(7.96, -0.04) * mm});
            skLineSegment(sketch, "E369", {"start": v(7.96, -0.04) * mm, "end": v(7.96, 0.05) * mm});
            skLineSegment(sketch, "E370", {"start": v(7.96, 0.05) * mm, "end": v(7.95, 0.15) * mm});
            skLineSegment(sketch, "E371", {"start": v(7.95, 0.15) * mm, "end": v(7.94, 0.24) * mm});
            skLineSegment(sketch, "E372", {"start": v(7.94, 0.24) * mm, "end": v(7.93, 0.32) * mm});
            skLineSegment(sketch, "E373", {"start": v(7.93, 0.32) * mm, "end": v(7.91, 0.41) * mm});
            skLineSegment(sketch, "E374", {"start": v(7.91, 0.41) * mm, "end": v(7.9, 0.5) * mm});
            skLineSegment(sketch, "E375", {"start": v(7.9, 0.5) * mm, "end": v(7.88, 0.57) * mm});
            skLineSegment(sketch, "E376", {"start": v(7.88, 0.57) * mm, "end": v(7.85, 0.65) * mm});
            skLineSegment(sketch, "E377", {"start": v(7.85, 0.65) * mm, "end": v(7.83, 0.73) * mm});
            skLineSegment(sketch, "E378", {"start": v(7.83, 0.73) * mm, "end": v(7.8, 0.8) * mm});
            skLineSegment(sketch, "E379", {"start": v(7.8, 0.8) * mm, "end": v(7.77, 0.87) * mm});
            skLineSegment(sketch, "E380", {"start": v(7.77, 0.87) * mm, "end": v(7.74, 0.94) * mm});
            skLineSegment(sketch, "E381", {"start": v(7.74, 0.94) * mm, "end": v(7.7, 1) * mm});
            skLineSegment(sketch, "E382", {"start": v(7.7, 1) * mm, "end": v(7.67, 1.06) * mm});
            skLineSegment(sketch, "E383", {"start": v(7.67, 1.06) * mm, "end": v(7.63, 1.11) * mm});
            skLineSegment(sketch, "E384", {"start": v(7.63, 1.11) * mm, "end": v(7.56, 1.2) * mm});
            skLineSegment(sketch, "E385", {"start": v(7.56, 1.2) * mm, "end": v(7.48, 1.29) * mm});
            skLineSegment(sketch, "E386", {"start": v(7.48, 1.29) * mm, "end": v(7.4, 1.36) * mm});
            skLineSegment(sketch, "E387", {"start": v(7.4, 1.36) * mm, "end": v(7.31, 1.42) * mm});
            skLineSegment(sketch, "E388", {"start": v(7.31, 1.42) * mm, "end": v(7.22, 1.48) * mm});
            skLineSegment(sketch, "E389", {"start": v(7.22, 1.48) * mm, "end": v(7.13, 1.53) * mm});
            skLineSegment(sketch, "E390", {"start": v(7.13, 1.53) * mm, "end": v(7.03, 1.57) * mm});
            skLineSegment(sketch, "E391", {"start": v(7.03, 1.57) * mm, "end": v(6.92, 1.6) * mm});
            skLineSegment(sketch, "E392", {"start": v(6.92, 1.6) * mm, "end": v(6.81, 1.64) * mm});
            skLineSegment(sketch, "E393", {"start": v(6.81, 1.64) * mm, "end": v(6.7, 1.66) * mm});
            skLineSegment(sketch, "E394", {"start": v(6.7, 1.66) * mm, "end": v(6.58, 1.68) * mm});
            skLineSegment(sketch, "E395", {"start": v(6.58, 1.68) * mm, "end": v(6.45, 1.7) * mm});
            skLineSegment(sketch, "E396", {"start": v(6.45, 1.7) * mm, "end": v(6.32, 1.7) * mm});
            skLineSegment(sketch, "E397", {"start": v(6.32, 1.7) * mm, "end": v(6.18, 1.72) * mm});
            skLineSegment(sketch, "E398", {"start": v(6.18, 1.72) * mm, "end": v(6.04, 1.72) * mm});
            skLineSegment(sketch, "E399", {"start": v(6.04, 1.72) * mm, "end": v(5.89, 1.72) * mm});
            skLineSegment(sketch, "E400", {"start": v(5.89, 1.72) * mm, "end": v(5.8, 1.72) * mm});
            skLineSegment(sketch, "E401", {"start": v(5.8, 1.72) * mm, "end": v(5.7, 1.72) * mm});
            skLineSegment(sketch, "E402", {"start": v(5.7, 1.72) * mm, "end": v(5.62, 1.72) * mm});
            skLineSegment(sketch, "E403", {"start": v(5.62, 1.72) * mm, "end": v(5.53, 1.72) * mm});
            skLineSegment(sketch, "E404", {"start": v(5.53, 1.72) * mm, "end": v(5.44, 1.72) * mm});
            skLineSegment(sketch, "E405", {"start": v(5.44, 1.72) * mm, "end": v(5.35, 1.72) * mm});
            skLineSegment(sketch, "E406", {"start": v(5.35, 1.72) * mm, "end": v(5.26, 1.72) * mm});
            skLineSegment(sketch, "E407", {"start": v(5.26, 1.72) * mm, "end": v(5.17, 1.72) * mm});
            skLineSegment(sketch, "E408", {"start": v(5.17, 1.72) * mm, "end": v(5.08, 1.72) * mm});
            skLineSegment(sketch, "E409", {"start": v(5.08, 1.72) * mm, "end": v(4.99, 1.72) * mm});
            skLineSegment(sketch, "E410", {"start": v(4.99, 1.72) * mm, "end": v(4.9, 1.72) * mm});
            skLineSegment(sketch, "E411", {"start": v(4.9, 1.72) * mm, "end": v(4.8, 1.72) * mm});
            skLineSegment(sketch, "E412", {"start": v(4.8, 1.72) * mm, "end": v(4.72, 1.72) * mm});
            skLineSegment(sketch, "E413", {"start": v(4.72, 1.72) * mm, "end": v(4.63, 1.72) * mm});
            skLineSegment(sketch, "E414", {"start": v(4.63, 1.72) * mm, "end": v(4.54, 1.72) * mm});
            skLineSegment(sketch, "E415", {"start": v(4.54, 1.72) * mm, "end": v(4.45, 1.72) * mm});
            skLineSegment(sketch, "E416", {"start": v(5.47, 0.93) * mm, "end": v(5.5, 0.93) * mm});
            skLineSegment(sketch, "E417", {"start": v(5.5, 0.93) * mm, "end": v(5.52, 0.93) * mm});
            skLineSegment(sketch, "E418", {"start": v(5.52, 0.93) * mm, "end": v(5.55, 0.93) * mm});
            skLineSegment(sketch, "E419", {"start": v(5.55, 0.93) * mm, "end": v(5.58, 0.93) * mm});
            skLineSegment(sketch, "E420", {"start": v(5.58, 0.93) * mm, "end": v(5.6, 0.93) * mm});
            skLineSegment(sketch, "E421", {"start": v(5.6, 0.93) * mm, "end": v(5.63, 0.93) * mm});
            skLineSegment(sketch, "E422", {"start": v(5.63, 0.93) * mm, "end": v(5.66, 0.93) * mm});
            skLineSegment(sketch, "E423", {"start": v(5.66, 0.93) * mm, "end": v(5.69, 0.93) * mm});
            skLineSegment(sketch, "E424", {"start": v(5.69, 0.93) * mm, "end": v(5.71, 0.93) * mm});
            skLineSegment(sketch, "E425", {"start": v(5.71, 0.93) * mm, "end": v(5.74, 0.93) * mm});
            skLineSegment(sketch, "E426", {"start": v(5.74, 0.93) * mm, "end": v(5.77, 0.93) * mm});
            skLineSegment(sketch, "E427", {"start": v(5.77, 0.93) * mm, "end": v(5.8, 0.93) * mm});
            skLineSegment(sketch, "E428", {"start": v(5.8, 0.93) * mm, "end": v(5.82, 0.93) * mm});
            skLineSegment(sketch, "E429", {"start": v(5.82, 0.93) * mm, "end": v(5.85, 0.93) * mm});
            skLineSegment(sketch, "E430", {"start": v(5.85, 0.93) * mm, "end": v(5.88, 0.93) * mm});
            skLineSegment(sketch, "E431", {"start": v(5.88, 0.93) * mm, "end": v(5.9, 0.93) * mm});
            skLineSegment(sketch, "E432", {"start": v(5.9, 0.93) * mm, "end": v(6.02, 0.93) * mm});
            skLineSegment(sketch, "E433", {"start": v(6.02, 0.93) * mm, "end": v(6.14, 0.92) * mm});
            skLineSegment(sketch, "E434", {"start": v(6.14, 0.92) * mm, "end": v(6.24, 0.9) * mm});
            skLineSegment(sketch, "E435", {"start": v(6.24, 0.9) * mm, "end": v(6.34, 0.87) * mm});
            skLineSegment(sketch, "E436", {"start": v(6.34, 0.87) * mm, "end": v(6.43, 0.84) * mm});
            skLineSegment(sketch, "E437", {"start": v(6.43, 0.84) * mm, "end": v(6.52, 0.8) * mm});
            skLineSegment(sketch, "E438", {"start": v(6.52, 0.8) * mm, "end": v(6.6, 0.75) * mm});
            skLineSegment(sketch, "E439", {"start": v(6.6, 0.75) * mm, "end": v(6.67, 0.7) * mm});
            skLineSegment(sketch, "E440", {"start": v(6.67, 0.7) * mm, "end": v(6.74, 0.63) * mm});
            skLineSegment(sketch, "E441", {"start": v(6.74, 0.63) * mm, "end": v(6.8, 0.55) * mm});
            skLineSegment(sketch, "E442", {"start": v(6.8, 0.55) * mm, "end": v(6.84, 0.47) * mm});
            skLineSegment(sketch, "E443", {"start": v(6.84, 0.47) * mm, "end": v(6.89, 0.37) * mm});
            skLineSegment(sketch, "E444", {"start": v(6.89, 0.37) * mm, "end": v(6.92, 0.27) * mm});
            skLineSegment(sketch, "E445", {"start": v(6.92, 0.27) * mm, "end": v(6.94, 0.16) * mm});
            skLineSegment(sketch, "E446", {"start": v(6.94, 0.16) * mm, "end": v(6.96, 0.03) * mm});
            skLineSegment(sketch, "E447", {"start": v(6.96, 0.03) * mm, "end": v(6.96, -0.1) * mm});
            skLineSegment(sketch, "E448", {"start": v(6.96, -0.1) * mm, "end": v(6.96, -0.24) * mm});
            skLineSegment(sketch, "E449", {"start": v(6.96, -0.24) * mm, "end": v(6.94, -0.36) * mm});
            skLineSegment(sketch, "E450", {"start": v(6.94, -0.36) * mm, "end": v(6.92, -0.47) * mm});
            skLineSegment(sketch, "E451", {"start": v(6.92, -0.47) * mm, "end": v(6.89, -0.58) * mm});
            skLineSegment(sketch, "E452", {"start": v(6.89, -0.58) * mm, "end": v(6.84, -0.67) * mm});
            skLineSegment(sketch, "E453", {"start": v(6.84, -0.67) * mm, "end": v(6.8, -0.76) * mm});
            skLineSegment(sketch, "E454", {"start": v(6.8, -0.76) * mm, "end": v(6.74, -0.83) * mm});
            skLineSegment(sketch, "E455", {"start": v(6.74, -0.83) * mm, "end": v(6.67, -0.9) * mm});
            skLineSegment(sketch, "E456", {"start": v(6.67, -0.9) * mm, "end": v(6.6, -0.96) * mm});
            skLineSegment(sketch, "E457", {"start": v(6.6, -0.96) * mm, "end": v(6.52, -1) * mm});
            skLineSegment(sketch, "E458", {"start": v(6.52, -1) * mm, "end": v(6.43, -1.05) * mm});
            skLineSegment(sketch, "E459", {"start": v(6.43, -1.05) * mm, "end": v(6.34, -1.08) * mm});
            skLineSegment(sketch, "E460", {"start": v(6.34, -1.08) * mm, "end": v(6.24, -1.1) * mm});
            skLineSegment(sketch, "E461", {"start": v(6.24, -1.1) * mm, "end": v(6.14, -1.12) * mm});
            skLineSegment(sketch, "E462", {"start": v(6.14, -1.12) * mm, "end": v(6.02, -1.13) * mm});
            skLineSegment(sketch, "E463", {"start": v(6.02, -1.13) * mm, "end": v(5.9, -1.13) * mm});
            skLineSegment(sketch, "E464", {"start": v(5.9, -1.13) * mm, "end": v(5.88, -1.13) * mm});
            skLineSegment(sketch, "E465", {"start": v(5.88, -1.13) * mm, "end": v(5.85, -1.13) * mm});
            skLineSegment(sketch, "E466", {"start": v(5.85, -1.13) * mm, "end": v(5.82, -1.13) * mm});
            skLineSegment(sketch, "E467", {"start": v(5.82, -1.13) * mm, "end": v(5.8, -1.13) * mm});
            skLineSegment(sketch, "E468", {"start": v(5.8, -1.13) * mm, "end": v(5.77, -1.13) * mm});
            skLineSegment(sketch, "E469", {"start": v(5.77, -1.13) * mm, "end": v(5.74, -1.13) * mm});
            skLineSegment(sketch, "E470", {"start": v(5.74, -1.13) * mm, "end": v(5.71, -1.13) * mm});
            skLineSegment(sketch, "E471", {"start": v(5.71, -1.13) * mm, "end": v(5.69, -1.13) * mm});
            skLineSegment(sketch, "E472", {"start": v(5.69, -1.13) * mm, "end": v(5.66, -1.13) * mm});
            skLineSegment(sketch, "E473", {"start": v(5.66, -1.13) * mm, "end": v(5.63, -1.13) * mm});
            skLineSegment(sketch, "E474", {"start": v(5.63, -1.13) * mm, "end": v(5.6, -1.13) * mm});
            skLineSegment(sketch, "E475", {"start": v(5.6, -1.13) * mm, "end": v(5.58, -1.13) * mm});
            skLineSegment(sketch, "E476", {"start": v(5.58, -1.13) * mm, "end": v(5.55, -1.13) * mm});
            skLineSegment(sketch, "E477", {"start": v(5.55, -1.13) * mm, "end": v(5.52, -1.13) * mm});
            skLineSegment(sketch, "E478", {"start": v(5.52, -1.13) * mm, "end": v(5.5, -1.13) * mm});
            skLineSegment(sketch, "E479", {"start": v(5.5, -1.13) * mm, "end": v(5.47, -1.13) * mm});
            skLineSegment(sketch, "E480", {"start": v(5.47, -1.13) * mm, "end": v(5.47, -1) * mm});
            skLineSegment(sketch, "E481", {"start": v(5.47, -1) * mm, "end": v(5.47, -0.88) * mm});
            skLineSegment(sketch, "E482", {"start": v(5.47, -0.88) * mm, "end": v(5.47, -0.75) * mm});
            skLineSegment(sketch, "E483", {"start": v(5.47, -0.75) * mm, "end": v(5.47, -0.62) * mm});
            skLineSegment(sketch, "E484", {"start": v(5.47, -0.62) * mm, "end": v(5.47, -0.49) * mm});
            skLineSegment(sketch, "E485", {"start": v(5.47, -0.49) * mm, "end": v(5.47, -0.36) * mm});
            skLineSegment(sketch, "E486", {"start": v(5.47, -0.36) * mm, "end": v(5.47, -0.23) * mm});
            skLineSegment(sketch, "E487", {"start": v(5.47, -0.23) * mm, "end": v(5.47, -0.1) * mm});
            skLineSegment(sketch, "E488", {"start": v(5.47, -0.1) * mm, "end": v(5.47, 0.03) * mm});
            skLineSegment(sketch, "E489", {"start": v(5.47, 0.03) * mm, "end": v(5.47, 0.16) * mm});
            skLineSegment(sketch, "E490", {"start": v(5.47, 0.16) * mm, "end": v(5.47, 0.28) * mm});
            skLineSegment(sketch, "E491", {"start": v(5.47, 0.28) * mm, "end": v(5.47, 0.41) * mm});
            skLineSegment(sketch, "E492", {"start": v(5.47, 0.41) * mm, "end": v(5.47, 0.54) * mm});
            skLineSegment(sketch, "E493", {"start": v(5.47, 0.54) * mm, "end": v(5.47, 0.67) * mm});
            skLineSegment(sketch, "E494", {"start": v(5.47, 0.67) * mm, "end": v(5.47, 0.8) * mm});
            skLineSegment(sketch, "E495", {"start": v(5.47, 0.8) * mm, "end": v(5.47, 0.93) * mm});
            skLineSegment(sketch, "E496", {"start": v(1.32, 1.72) * mm, "end": v(1.27, 1.54) * mm});
            skLineSegment(sketch, "E497", {"start": v(1.27, 1.54) * mm, "end": v(1.21, 1.36) * mm});
            skLineSegment(sketch, "E498", {"start": v(1.21, 1.36) * mm, "end": v(1.16, 1.18) * mm});
            skLineSegment(sketch, "E499", {"start": v(1.16, 1.18) * mm, "end": v(1.1, 1) * mm});
            skLineSegment(sketch, "E500", {"start": v(1.1, 1) * mm, "end": v(1.05, 0.82) * mm});
            skLineSegment(sketch, "E501", {"start": v(1.05, 0.82) * mm, "end": v(1, 0.64) * mm});
            skLineSegment(sketch, "E502", {"start": v(1, 0.64) * mm, "end": v(0.95, 0.46) * mm});
            skLineSegment(sketch, "E503", {"start": v(0.95, 0.46) * mm, "end": v(0.9, 0.28) * mm});
            skLineSegment(sketch, "E504", {"start": v(0.9, 0.28) * mm, "end": v(0.84, 0.1) * mm});
            skLineSegment(sketch, "E505", {"start": v(0.84, 0.1) * mm, "end": v(0.79, -0.08) * mm});
            skLineSegment(sketch, "E506", {"start": v(0.79, -0.08) * mm, "end": v(0.73, -0.26) * mm});
            skLineSegment(sketch, "E507", {"start": v(0.73, -0.26) * mm, "end": v(0.68, -0.44) * mm});
            skLineSegment(sketch, "E508", {"start": v(0.68, -0.44) * mm, "end": v(0.62, -0.62) * mm});
            skLineSegment(sketch, "E509", {"start": v(0.62, -0.62) * mm, "end": v(0.57, -0.8) * mm});
            skLineSegment(sketch, "E510", {"start": v(0.57, -0.8) * mm, "end": v(0.52, -0.98) * mm});
            skLineSegment(sketch, "E511", {"start": v(0.52, -0.98) * mm, "end": v(0.46, -1.16) * mm});
            skLineSegment(sketch, "E512", {"start": v(0.46, -1.16) * mm, "end": v(0.41, -0.98) * mm});
            skLineSegment(sketch, "E513", {"start": v(0.41, -0.98) * mm, "end": v(0.36, -0.8) * mm});
            skLineSegment(sketch, "E514", {"start": v(0.36, -0.8) * mm, "end": v(0.31, -0.62) * mm});
            skLineSegment(sketch, "E515", {"start": v(0.31, -0.62) * mm, "end": v(0.26, -0.44) * mm});
            skLineSegment(sketch, "E516", {"start": v(0.26, -0.44) * mm, "end": v(0.2, -0.26) * mm});
            skLineSegment(sketch, "E517", {"start": v(0.2, -0.26) * mm, "end": v(0.16, -0.08) * mm});
            skLineSegment(sketch, "E518", {"start": v(0.16, -0.08) * mm, "end": v(0.1, 0.1) * mm});
            skLineSegment(sketch, "E519", {"start": v(0.1, 0.1) * mm, "end": v(0.05, 0.28) * mm});
            skLineSegment(sketch, "E520", {"start": v(0.05, 0.28) * mm, "end": v(0, 0.46) * mm});
            skLineSegment(sketch, "E521", {"start": v(0, 0.46) * mm, "end": v(-0.05, 0.64) * mm});
            skLineSegment(sketch, "E522", {"start": v(-0.05, 0.64) * mm, "end": v(-0.1, 0.82) * mm});
            skLineSegment(sketch, "E523", {"start": v(-0.1, 0.82) * mm, "end": v(-0.15, 1) * mm});
            skLineSegment(sketch, "E524", {"start": v(-0.15, 1) * mm, "end": v(-0.2, 1.18) * mm});
            skLineSegment(sketch, "E525", {"start": v(-0.2, 1.18) * mm, "end": v(-0.25, 1.36) * mm});
            skLineSegment(sketch, "E526", {"start": v(-0.25, 1.36) * mm, "end": v(-0.3, 1.54) * mm});
            skLineSegment(sketch, "E527", {"start": v(-0.3, 1.54) * mm, "end": v(-0.36, 1.72) * mm});
            skLineSegment(sketch, "E528", {"start": v(-0.36, 1.72) * mm, "end": v(-0.43, 1.72) * mm});
            skLineSegment(sketch, "E529", {"start": v(-0.43, 1.72) * mm, "end": v(-0.5, 1.72) * mm});
            skLineSegment(sketch, "E530", {"start": v(-0.5, 1.72) * mm, "end": v(-0.56, 1.72) * mm});
            skLineSegment(sketch, "E531", {"start": v(-0.56, 1.72) * mm, "end": v(-0.63, 1.72) * mm});
            skLineSegment(sketch, "E532", {"start": v(-0.63, 1.72) * mm, "end": v(-0.7, 1.72) * mm});
            skLineSegment(sketch, "E533", {"start": v(-0.7, 1.72) * mm, "end": v(-0.77, 1.72) * mm});
            skLineSegment(sketch, "E534", {"start": v(-0.77, 1.72) * mm, "end": v(-0.84, 1.72) * mm});
            skLineSegment(sketch, "E535", {"start": v(-0.84, 1.72) * mm, "end": v(-0.9, 1.72) * mm});
            skLineSegment(sketch, "E536", {"start": v(-0.9, 1.72) * mm, "end": v(-0.98, 1.72) * mm});
            skLineSegment(sketch, "E537", {"start": v(-0.98, 1.72) * mm, "end": v(-1.05, 1.72) * mm});
            skLineSegment(sketch, "E538", {"start": v(-1.05, 1.72) * mm, "end": v(-1.12, 1.72) * mm});
            skLineSegment(sketch, "E539", {"start": v(-1.12, 1.72) * mm, "end": v(-1.19, 1.72) * mm});
            skLineSegment(sketch, "E540", {"start": v(-1.19, 1.72) * mm, "end": v(-1.26, 1.72) * mm});
            skLineSegment(sketch, "E541", {"start": v(-1.26, 1.72) * mm, "end": v(-1.32, 1.72) * mm});
            skLineSegment(sketch, "E542", {"start": v(-1.32, 1.72) * mm, "end": v(-1.4, 1.72) * mm});
            skLineSegment(sketch, "E543", {"start": v(-1.4, 1.72) * mm, "end": v(-1.46, 1.72) * mm});
            skLineSegment(sketch, "E544", {"start": v(-1.46, 1.72) * mm, "end": v(-1.4, 1.5) * mm});
            skLineSegment(sketch, "E545", {"start": v(-1.4, 1.5) * mm, "end": v(-1.32, 1.27) * mm});
            skLineSegment(sketch, "E546", {"start": v(-1.32, 1.27) * mm, "end": v(-1.24, 1.04) * mm});
            skLineSegment(sketch, "E547", {"start": v(-1.24, 1.04) * mm, "end": v(-1.17, 0.81) * mm});
            skLineSegment(sketch, "E548", {"start": v(-1.17, 0.81) * mm, "end": v(-1.1, 0.59) * mm});
            skLineSegment(sketch, "E549", {"start": v(-1.1, 0.59) * mm, "end": v(-1.02, 0.36) * mm});
            skLineSegment(sketch, "E550", {"start": v(-1.02, 0.36) * mm, "end": v(-0.95, 0.13) * mm});
            skLineSegment(sketch, "E551", {"start": v(-0.95, 0.13) * mm, "end": v(-0.88, -0.1) * mm});
            skLineSegment(sketch, "E552", {"start": v(-0.88, -0.1) * mm, "end": v(-0.8, -0.32) * mm});
            skLineSegment(sketch, "E553", {"start": v(-0.8, -0.32) * mm, "end": v(-0.73, -0.55) * mm});
            skLineSegment(sketch, "E554", {"start": v(-0.73, -0.55) * mm, "end": v(-0.66, -0.78) * mm});
            skLineSegment(sketch, "E555", {"start": v(-0.66, -0.78) * mm, "end": v(-0.58, -1) * mm});
            skLineSegment(sketch, "E556", {"start": v(-0.58, -1) * mm, "end": v(-0.51, -1.23) * mm});
            skLineSegment(sketch, "E557", {"start": v(-0.51, -1.23) * mm, "end": v(-0.44, -1.46) * mm});
            skLineSegment(sketch, "E558", {"start": v(-0.44, -1.46) * mm, "end": v(-0.37, -1.68) * mm});
            skLineSegment(sketch, "E559", {"start": v(-0.37, -1.68) * mm, "end": v(-0.3, -1.91) * mm});
            skLineSegment(sketch, "E560", {"start": v(-0.3, -1.91) * mm, "end": v(-0.2, -1.91) * mm});
            skLineSegment(sketch, "E561", {"start": v(-0.2, -1.91) * mm, "end": v(-0.1, -1.91) * mm});
            skLineSegment(sketch, "E562", {"start": v(-0.1, -1.91) * mm, "end": v(-0.01, -1.91) * mm});
            skLineSegment(sketch, "E563", {"start": v(-0.01, -1.91) * mm, "end": v(0.08, -1.91) * mm});
            skLineSegment(sketch, "E564", {"start": v(0.08, -1.91) * mm, "end": v(0.17, -1.91) * mm});
            skLineSegment(sketch, "E565", {"start": v(0.17, -1.91) * mm, "end": v(0.26, -1.91) * mm});
            skLineSegment(sketch, "E566", {"start": v(0.26, -1.91) * mm, "end": v(0.35, -1.91) * mm});
            skLineSegment(sketch, "E567", {"start": v(0.35, -1.91) * mm, "end": v(0.45, -1.91) * mm});
            skLineSegment(sketch, "E568", {"start": v(0.45, -1.91) * mm, "end": v(0.54, -1.91) * mm});
            skLineSegment(sketch, "E569", {"start": v(0.54, -1.91) * mm, "end": v(0.63, -1.91) * mm});
            skLineSegment(sketch, "E570", {"start": v(0.63, -1.91) * mm, "end": v(0.72, -1.91) * mm});
            skLineSegment(sketch, "E571", {"start": v(0.72, -1.91) * mm, "end": v(0.82, -1.91) * mm});
            skLineSegment(sketch, "E572", {"start": v(0.82, -1.91) * mm, "end": v(0.9, -1.91) * mm});
            skLineSegment(sketch, "E573", {"start": v(0.9, -1.91) * mm, "end": v(1, -1.91) * mm});
            skLineSegment(sketch, "E574", {"start": v(1, -1.91) * mm, "end": v(1.1, -1.91) * mm});
            skLineSegment(sketch, "E575", {"start": v(1.1, -1.91) * mm, "end": v(1.19, -1.91) * mm});
            skLineSegment(sketch, "E576", {"start": v(1.19, -1.91) * mm, "end": v(1.26, -1.68) * mm});
            skLineSegment(sketch, "E577", {"start": v(1.26, -1.68) * mm, "end": v(1.33, -1.46) * mm});
            skLineSegment(sketch, "E578", {"start": v(1.33, -1.46) * mm, "end": v(1.4, -1.23) * mm});
            skLineSegment(sketch, "E579", {"start": v(1.4, -1.23) * mm, "end": v(1.48, -1) * mm});
            skLineSegment(sketch, "E580", {"start": v(1.48, -1) * mm, "end": v(1.56, -0.78) * mm});
            skLineSegment(sketch, "E581", {"start": v(1.56, -0.78) * mm, "end": v(1.63, -0.55) * mm});
            skLineSegment(sketch, "E582", {"start": v(1.63, -0.55) * mm, "end": v(1.7, -0.32) * mm});
            skLineSegment(sketch, "E583", {"start": v(1.7, -0.32) * mm, "end": v(1.78, -0.1) * mm});
            skLineSegment(sketch, "E584", {"start": v(1.78, -0.1) * mm, "end": v(1.85, 0.13) * mm});
            skLineSegment(sketch, "E585", {"start": v(1.85, 0.13) * mm, "end": v(1.92, 0.36) * mm});
            skLineSegment(sketch, "E586", {"start": v(1.92, 0.36) * mm, "end": v(2, 0.59) * mm});
            skLineSegment(sketch, "E587", {"start": v(2, 0.59) * mm, "end": v(2.07, 0.81) * mm});
            skLineSegment(sketch, "E588", {"start": v(2.07, 0.81) * mm, "end": v(2.14, 1.04) * mm});
            skLineSegment(sketch, "E589", {"start": v(2.14, 1.04) * mm, "end": v(2.22, 1.27) * mm});
            skLineSegment(sketch, "E590", {"start": v(2.22, 1.27) * mm, "end": v(2.3, 1.5) * mm});
            skLineSegment(sketch, "E591", {"start": v(2.3, 1.5) * mm, "end": v(2.37, 1.72) * mm});
            skLineSegment(sketch, "E592", {"start": v(2.37, 1.72) * mm, "end": v(2.3, 1.72) * mm});
            skLineSegment(sketch, "E593", {"start": v(2.3, 1.72) * mm, "end": v(2.24, 1.72) * mm});
            skLineSegment(sketch, "E594", {"start": v(2.24, 1.72) * mm, "end": v(2.17, 1.72) * mm});
            skLineSegment(sketch, "E595", {"start": v(2.17, 1.72) * mm, "end": v(2.1, 1.72) * mm});
            skLineSegment(sketch, "E596", {"start": v(2.1, 1.72) * mm, "end": v(2.04, 1.72) * mm});
            skLineSegment(sketch, "E597", {"start": v(2.04, 1.72) * mm, "end": v(1.97, 1.72) * mm});
            skLineSegment(sketch, "E598", {"start": v(1.97, 1.72) * mm, "end": v(1.9, 1.72) * mm});
            skLineSegment(sketch, "E599", {"start": v(1.9, 1.72) * mm, "end": v(1.84, 1.72) * mm});
            skLineSegment(sketch, "E600", {"start": v(1.84, 1.72) * mm, "end": v(1.78, 1.72) * mm});
            skLineSegment(sketch, "E601", {"start": v(1.78, 1.72) * mm, "end": v(1.71, 1.72) * mm});
            skLineSegment(sketch, "E602", {"start": v(1.71, 1.72) * mm, "end": v(1.65, 1.72) * mm});
            skLineSegment(sketch, "E603", {"start": v(1.65, 1.72) * mm, "end": v(1.58, 1.72) * mm});
            skLineSegment(sketch, "E604", {"start": v(1.58, 1.72) * mm, "end": v(1.52, 1.72) * mm});
            skLineSegment(sketch, "E605", {"start": v(1.52, 1.72) * mm, "end": v(1.45, 1.72) * mm});
            skLineSegment(sketch, "E606", {"start": v(1.45, 1.72) * mm, "end": v(1.39, 1.72) * mm});
            skLineSegment(sketch, "E607", {"start": v(1.39, 1.72) * mm, "end": v(1.32, 1.72) * mm});
            skLineSegment(sketch, "E608", {"start": v(8.44, -1.91) * mm, "end": v(8.5, -1.91) * mm});
            skLineSegment(sketch, "E609", {"start": v(8.5, -1.91) * mm, "end": v(8.57, -1.91) * mm});
            skLineSegment(sketch, "E610", {"start": v(8.57, -1.91) * mm, "end": v(8.63, -1.91) * mm});
            skLineSegment(sketch, "E611", {"start": v(8.63, -1.91) * mm, "end": v(8.7, -1.91) * mm});
            skLineSegment(sketch, "E612", {"start": v(8.7, -1.91) * mm, "end": v(8.76, -1.91) * mm});
            skLineSegment(sketch, "E613", {"start": v(8.76, -1.91) * mm, "end": v(8.83, -1.91) * mm});
            skLineSegment(sketch, "E614", {"start": v(8.83, -1.91) * mm, "end": v(8.89, -1.91) * mm});
            skLineSegment(sketch, "E615", {"start": v(8.89, -1.91) * mm, "end": v(8.95, -1.91) * mm});
            skLineSegment(sketch, "E616", {"start": v(8.95, -1.91) * mm, "end": v(9.02, -1.91) * mm});
            skLineSegment(sketch, "E617", {"start": v(9.02, -1.91) * mm, "end": v(9.08, -1.91) * mm});
            skLineSegment(sketch, "E618", {"start": v(9.08, -1.91) * mm, "end": v(9.15, -1.91) * mm});
            skLineSegment(sketch, "E619", {"start": v(9.15, -1.91) * mm, "end": v(9.21, -1.91) * mm});
            skLineSegment(sketch, "E620", {"start": v(9.21, -1.91) * mm, "end": v(9.27, -1.91) * mm});
            skLineSegment(sketch, "E621", {"start": v(9.27, -1.91) * mm, "end": v(9.34, -1.91) * mm});
            skLineSegment(sketch, "E622", {"start": v(9.34, -1.91) * mm, "end": v(9.4, -1.91) * mm});
            skLineSegment(sketch, "E623", {"start": v(9.4, -1.91) * mm, "end": v(9.47, -1.91) * mm});
            skLineSegment(sketch, "E624", {"start": v(9.47, -1.91) * mm, "end": v(9.47, -1.68) * mm});
            skLineSegment(sketch, "E625", {"start": v(9.47, -1.68) * mm, "end": v(9.47, -1.46) * mm});
            skLineSegment(sketch, "E626", {"start": v(9.47, -1.46) * mm, "end": v(9.47, -1.23) * mm});
            skLineSegment(sketch, "E627", {"start": v(9.47, -1.23) * mm, "end": v(9.47, -1) * mm});
            skLineSegment(sketch, "E628", {"start": v(9.47, -1) * mm, "end": v(9.47, -0.78) * mm});
            skLineSegment(sketch, "E629", {"start": v(9.47, -0.78) * mm, "end": v(9.47, -0.55) * mm});
            skLineSegment(sketch, "E630", {"start": v(9.47, -0.55) * mm, "end": v(9.47, -0.32) * mm});
            skLineSegment(sketch, "E631", {"start": v(9.47, -0.32) * mm, "end": v(9.47, -0.1) * mm});
            skLineSegment(sketch, "E632", {"start": v(9.47, -0.1) * mm, "end": v(9.47, 0.13) * mm});
            skLineSegment(sketch, "E633", {"start": v(9.47, 0.13) * mm, "end": v(9.47, 0.36) * mm});
            skLineSegment(sketch, "E634", {"start": v(9.47, 0.36) * mm, "end": v(9.47, 0.59) * mm});
            skLineSegment(sketch, "E635", {"start": v(9.47, 0.59) * mm, "end": v(9.47, 0.81) * mm});
            skLineSegment(sketch, "E636", {"start": v(9.47, 0.81) * mm, "end": v(9.47, 1.04) * mm});
            skLineSegment(sketch, "E637", {"start": v(9.47, 1.04) * mm, "end": v(9.47, 1.27) * mm});
            skLineSegment(sketch, "E638", {"start": v(9.47, 1.27) * mm, "end": v(9.47, 1.5) * mm});
            skLineSegment(sketch, "E639", {"start": v(9.47, 1.5) * mm, "end": v(9.47, 1.72) * mm});
            skLineSegment(sketch, "E640", {"start": v(9.47, 1.72) * mm, "end": v(9.4, 1.72) * mm});
            skLineSegment(sketch, "E641", {"start": v(9.4, 1.72) * mm, "end": v(9.34, 1.72) * mm});
            skLineSegment(sketch, "E642", {"start": v(9.34, 1.72) * mm, "end": v(9.27, 1.72) * mm});
            skLineSegment(sketch, "E643", {"start": v(9.27, 1.72) * mm, "end": v(9.21, 1.72) * mm});
            skLineSegment(sketch, "E644", {"start": v(9.21, 1.72) * mm, "end": v(9.15, 1.72) * mm});
            skLineSegment(sketch, "E645", {"start": v(9.15, 1.72) * mm, "end": v(9.08, 1.72) * mm});
            skLineSegment(sketch, "E646", {"start": v(9.08, 1.72) * mm, "end": v(9.02, 1.72) * mm});
            skLineSegment(sketch, "E647", {"start": v(9.02, 1.72) * mm, "end": v(8.95, 1.72) * mm});
            skLineSegment(sketch, "E648", {"start": v(8.95, 1.72) * mm, "end": v(8.89, 1.72) * mm});
            skLineSegment(sketch, "E649", {"start": v(8.89, 1.72) * mm, "end": v(8.83, 1.72) * mm});
            skLineSegment(sketch, "E650", {"start": v(8.83, 1.72) * mm, "end": v(8.76, 1.72) * mm});
            skLineSegment(sketch, "E651", {"start": v(8.76, 1.72) * mm, "end": v(8.7, 1.72) * mm});
            skLineSegment(sketch, "E652", {"start": v(8.7, 1.72) * mm, "end": v(8.63, 1.72) * mm});
            skLineSegment(sketch, "E653", {"start": v(8.63, 1.72) * mm, "end": v(8.57, 1.72) * mm});
            skLineSegment(sketch, "E654", {"start": v(8.57, 1.72) * mm, "end": v(8.5, 1.72) * mm});
            skLineSegment(sketch, "E655", {"start": v(8.5, 1.72) * mm, "end": v(8.44, 1.72) * mm});
            skLineSegment(sketch, "E656", {"start": v(8.44, 1.72) * mm, "end": v(8.44, 1.5) * mm});
            skLineSegment(sketch, "E657", {"start": v(8.44, 1.5) * mm, "end": v(8.44, 1.27) * mm});
            skLineSegment(sketch, "E658", {"start": v(8.44, 1.27) * mm, "end": v(8.44, 1.04) * mm});
            skLineSegment(sketch, "E659", {"start": v(8.44, 1.04) * mm, "end": v(8.44, 0.81) * mm});
            skLineSegment(sketch, "E660", {"start": v(8.44, 0.81) * mm, "end": v(8.44, 0.59) * mm});
            skLineSegment(sketch, "E661", {"start": v(8.44, 0.59) * mm, "end": v(8.44, 0.36) * mm});
            skLineSegment(sketch, "E662", {"start": v(8.44, 0.36) * mm, "end": v(8.44, 0.13) * mm});
            skLineSegment(sketch, "E663", {"start": v(8.44, 0.13) * mm, "end": v(8.44, -0.1) * mm});
            skLineSegment(sketch, "E664", {"start": v(8.44, -0.1) * mm, "end": v(8.44, -0.32) * mm});
            skLineSegment(sketch, "E665", {"start": v(8.44, -0.32) * mm, "end": v(8.44, -0.55) * mm});
            skLineSegment(sketch, "E666", {"start": v(8.44, -0.55) * mm, "end": v(8.44, -0.78) * mm});
            skLineSegment(sketch, "E667", {"start": v(8.44, -0.78) * mm, "end": v(8.44, -1) * mm});
            skLineSegment(sketch, "E668", {"start": v(8.44, -1) * mm, "end": v(8.44, -1.23) * mm});
            skLineSegment(sketch, "E669", {"start": v(8.44, -1.23) * mm, "end": v(8.44, -1.46) * mm});
            skLineSegment(sketch, "E670", {"start": v(8.44, -1.46) * mm, "end": v(8.44, -1.68) * mm});
            skLineSegment(sketch, "E671", {"start": v(8.44, -1.68) * mm, "end": v(8.44, -1.91) * mm});
            skLineSegment(sketch, "E672", {"start": v(11.32, 1.72) * mm, "end": v(11.23, 1.5) * mm});
            skLineSegment(sketch, "E673", {"start": v(11.23, 1.5) * mm, "end": v(11.14, 1.27) * mm});
            skLineSegment(sketch, "E674", {"start": v(11.14, 1.27) * mm, "end": v(11.05, 1.04) * mm});
            skLineSegment(sketch, "E675", {"start": v(11.05, 1.04) * mm, "end": v(10.96, 0.81) * mm});
            skLineSegment(sketch, "E676", {"start": v(10.96, 0.81) * mm, "end": v(10.87, 0.59) * mm});
            skLineSegment(sketch, "E677", {"start": v(10.87, 0.59) * mm, "end": v(10.78, 0.36) * mm});
            skLineSegment(sketch, "E678", {"start": v(10.78, 0.36) * mm, "end": v(10.69, 0.13) * mm});
            skLineSegment(sketch, "E679", {"start": v(10.69, 0.13) * mm, "end": v(10.6, -0.1) * mm});
            skLineSegment(sketch, "E680", {"start": v(10.6, -0.1) * mm, "end": v(10.5, -0.32) * mm});
            skLineSegment(sketch, "E681", {"start": v(10.5, -0.32) * mm, "end": v(10.42, -0.55) * mm});
            skLineSegment(sketch, "E682", {"start": v(10.42, -0.55) * mm, "end": v(10.33, -0.78) * mm});
            skLineSegment(sketch, "E683", {"start": v(10.33, -0.78) * mm, "end": v(10.24, -1) * mm});
            skLineSegment(sketch, "E684", {"start": v(10.24, -1) * mm, "end": v(10.15, -1.23) * mm});
            skLineSegment(sketch, "E685", {"start": v(10.15, -1.23) * mm, "end": v(10.06, -1.46) * mm});
            skLineSegment(sketch, "E686", {"start": v(10.06, -1.46) * mm, "end": v(9.97, -1.68) * mm});
            skLineSegment(sketch, "E687", {"start": v(9.97, -1.68) * mm, "end": v(9.88, -1.9) * mm});
            skLineSegment(sketch, "E688", {"start": v(9.88, -1.9) * mm, "end": v(9.95, -1.9) * mm});
            skLineSegment(sketch, "E689", {"start": v(9.95, -1.9) * mm, "end": v(10, -1.9) * mm});
            skLineSegment(sketch, "E690", {"start": v(10, -1.9) * mm, "end": v(10.07, -1.9) * mm});
            skLineSegment(sketch, "E691", {"start": v(10.07, -1.9) * mm, "end": v(10.14, -1.9) * mm});
            skLineSegment(sketch, "E692", {"start": v(10.14, -1.9) * mm, "end": v(10.2, -1.9) * mm});
            skLineSegment(sketch, "E693", {"start": v(10.2, -1.9) * mm, "end": v(10.26, -1.9) * mm});
            skLineSegment(sketch, "E694", {"start": v(10.26, -1.9) * mm, "end": v(10.33, -1.9) * mm});
            skLineSegment(sketch, "E695", {"start": v(10.33, -1.9) * mm, "end": v(10.39, -1.9) * mm});
            skLineSegment(sketch, "E696", {"start": v(10.39, -1.9) * mm, "end": v(10.45, -1.9) * mm});
            skLineSegment(sketch, "E697", {"start": v(10.45, -1.9) * mm, "end": v(10.52, -1.9) * mm});
            skLineSegment(sketch, "E698", {"start": v(10.52, -1.9) * mm, "end": v(10.58, -1.9) * mm});
            skLineSegment(sketch, "E699", {"start": v(10.58, -1.9) * mm, "end": v(10.64, -1.9) * mm});
            skLineSegment(sketch, "E700", {"start": v(10.64, -1.9) * mm, "end": v(10.7, -1.9) * mm});
            skLineSegment(sketch, "E701", {"start": v(10.7, -1.9) * mm, "end": v(10.77, -1.9) * mm});
            skLineSegment(sketch, "E702", {"start": v(10.77, -1.9) * mm, "end": v(10.83, -1.9) * mm});
            skLineSegment(sketch, "E703", {"start": v(10.83, -1.9) * mm, "end": v(10.9, -1.9) * mm});
            skLineSegment(sketch, "E704", {"start": v(10.9, -1.9) * mm, "end": v(10.9, -1.87) * mm});
            skLineSegment(sketch, "E705", {"start": v(10.9, -1.87) * mm, "end": v(10.92, -1.83) * mm});
            skLineSegment(sketch, "E706", {"start": v(10.92, -1.83) * mm, "end": v(10.94, -1.79) * mm});
            skLineSegment(sketch, "E707", {"start": v(10.94, -1.79) * mm, "end": v(10.95, -1.75) * mm});
            skLineSegment(sketch, "E708", {"start": v(10.95, -1.75) * mm, "end": v(10.97, -1.7) * mm});
            skLineSegment(sketch, "E709", {"start": v(10.97, -1.7) * mm, "end": v(10.98, -1.67) * mm});
            skLineSegment(sketch, "E710", {"start": v(10.98, -1.67) * mm, "end": v(11, -1.63) * mm});
            skLineSegment(sketch, "E711", {"start": v(11, -1.63) * mm, "end": v(11, -1.59) * mm});
            skLineSegment(sketch, "E712", {"start": v(11, -1.59) * mm, "end": v(11.02, -1.55) * mm});
            skLineSegment(sketch, "E713", {"start": v(11.02, -1.55) * mm, "end": v(11.04, -1.5) * mm});
            skLineSegment(sketch, "E714", {"start": v(11.04, -1.5) * mm, "end": v(11.05, -1.47) * mm});
            skLineSegment(sketch, "E715", {"start": v(11.05, -1.47) * mm, "end": v(11.06, -1.43) * mm});
            skLineSegment(sketch, "E716", {"start": v(11.06, -1.43) * mm, "end": v(11.08, -1.39) * mm});
            skLineSegment(sketch, "E717", {"start": v(11.08, -1.39) * mm, "end": v(11.1, -1.35) * mm});
            skLineSegment(sketch, "E718", {"start": v(11.1, -1.35) * mm, "end": v(11.1, -1.3) * mm});
            skLineSegment(sketch, "E719", {"start": v(11.1, -1.3) * mm, "end": v(11.12, -1.27) * mm});
            skLineSegment(sketch, "E720", {"start": v(11.12, -1.27) * mm, "end": v(11.23, -1.27) * mm});
            skLineSegment(sketch, "E721", {"start": v(11.23, -1.27) * mm, "end": v(11.33, -1.27) * mm});
            skLineSegment(sketch, "E722", {"start": v(11.33, -1.27) * mm, "end": v(11.44, -1.27) * mm});
            skLineSegment(sketch, "E723", {"start": v(11.44, -1.27) * mm, "end": v(11.54, -1.27) * mm});
            skLineSegment(sketch, "E724", {"start": v(11.54, -1.27) * mm, "end": v(11.65, -1.27) * mm});
            skLineSegment(sketch, "E725", {"start": v(11.65, -1.27) * mm, "end": v(11.76, -1.27) * mm});
            skLineSegment(sketch, "E726", {"start": v(11.76, -1.27) * mm, "end": v(11.86, -1.27) * mm});
            skLineSegment(sketch, "E727", {"start": v(11.86, -1.27) * mm, "end": v(11.97, -1.27) * mm});
            skLineSegment(sketch, "E728", {"start": v(11.97, -1.27) * mm, "end": v(12.07, -1.27) * mm});
            skLineSegment(sketch, "E729", {"start": v(12.07, -1.27) * mm, "end": v(12.18, -1.27) * mm});
            skLineSegment(sketch, "E730", {"start": v(12.18, -1.27) * mm, "end": v(12.29, -1.27) * mm});
            skLineSegment(sketch, "E731", {"start": v(12.29, -1.27) * mm, "end": v(12.4, -1.27) * mm});
            skLineSegment(sketch, "E732", {"start": v(12.4, -1.27) * mm, "end": v(12.5, -1.27) * mm});
            skLineSegment(sketch, "E733", {"start": v(12.5, -1.27) * mm, "end": v(12.6, -1.27) * mm});
            skLineSegment(sketch, "E734", {"start": v(12.6, -1.27) * mm, "end": v(12.7, -1.27) * mm});
            skLineSegment(sketch, "E735", {"start": v(12.7, -1.27) * mm, "end": v(12.82, -1.27) * mm});
            skLineSegment(sketch, "E736", {"start": v(12.82, -1.27) * mm, "end": v(12.83, -1.3) * mm});
            skLineSegment(sketch, "E737", {"start": v(12.83, -1.3) * mm, "end": v(12.84, -1.35) * mm});
            skLineSegment(sketch, "E738", {"start": v(12.84, -1.35) * mm, "end": v(12.86, -1.39) * mm});
            skLineSegment(sketch, "E739", {"start": v(12.86, -1.39) * mm, "end": v(12.87, -1.43) * mm});
            skLineSegment(sketch, "E740", {"start": v(12.87, -1.43) * mm, "end": v(12.88, -1.47) * mm});
            skLineSegment(sketch, "E741", {"start": v(12.88, -1.47) * mm, "end": v(12.9, -1.5) * mm});
            skLineSegment(sketch, "E742", {"start": v(12.9, -1.5) * mm, "end": v(12.9, -1.55) * mm});
            skLineSegment(sketch, "E743", {"start": v(12.9, -1.55) * mm, "end": v(12.92, -1.59) * mm});
            skLineSegment(sketch, "E744", {"start": v(12.92, -1.59) * mm, "end": v(12.94, -1.63) * mm});
            skLineSegment(sketch, "E745", {"start": v(12.94, -1.63) * mm, "end": v(12.95, -1.67) * mm});
            skLineSegment(sketch, "E746", {"start": v(12.95, -1.67) * mm, "end": v(12.96, -1.7) * mm});
            skLineSegment(sketch, "E747", {"start": v(12.96, -1.7) * mm, "end": v(12.98, -1.75) * mm});
            skLineSegment(sketch, "E748", {"start": v(12.98, -1.75) * mm, "end": v(13, -1.79) * mm});
            skLineSegment(sketch, "E749", {"start": v(13, -1.79) * mm, "end": v(13, -1.83) * mm});
            skLineSegment(sketch, "E750", {"start": v(13, -1.83) * mm, "end": v(13.02, -1.87) * mm});
            skLineSegment(sketch, "E751", {"start": v(13.02, -1.87) * mm, "end": v(13.03, -1.9) * mm});
            skLineSegment(sketch, "E752", {"start": v(13.03, -1.9) * mm, "end": v(13.1, -1.9) * mm});
            skLineSegment(sketch, "E753", {"start": v(13.1, -1.9) * mm, "end": v(13.17, -1.9) * mm});
            skLineSegment(sketch, "E754", {"start": v(13.17, -1.9) * mm, "end": v(13.24, -1.9) * mm});
            skLineSegment(sketch, "E755", {"start": v(13.24, -1.9) * mm, "end": v(13.3, -1.9) * mm});
            skLineSegment(sketch, "E756", {"start": v(13.3, -1.9) * mm, "end": v(13.37, -1.9) * mm});
            skLineSegment(sketch, "E757", {"start": v(13.37, -1.9) * mm, "end": v(13.44, -1.9) * mm});
            skLineSegment(sketch, "E758", {"start": v(13.44, -1.9) * mm, "end": v(13.51, -1.9) * mm});
            skLineSegment(sketch, "E759", {"start": v(13.51, -1.9) * mm, "end": v(13.58, -1.9) * mm});
            skLineSegment(sketch, "E760", {"start": v(13.58, -1.9) * mm, "end": v(13.65, -1.9) * mm});
            skLineSegment(sketch, "E761", {"start": v(13.65, -1.9) * mm, "end": v(13.72, -1.9) * mm});
            skLineSegment(sketch, "E762", {"start": v(13.72, -1.9) * mm, "end": v(13.79, -1.9) * mm});
            skLineSegment(sketch, "E763", {"start": v(13.79, -1.9) * mm, "end": v(13.85, -1.9) * mm});
            skLineSegment(sketch, "E764", {"start": v(13.85, -1.9) * mm, "end": v(13.92, -1.9) * mm});
            skLineSegment(sketch, "E765", {"start": v(13.92, -1.9) * mm, "end": v(14, -1.9) * mm});
            skLineSegment(sketch, "E766", {"start": v(14, -1.9) * mm, "end": v(14.06, -1.9) * mm});
            skLineSegment(sketch, "E767", {"start": v(14.06, -1.9) * mm, "end": v(14.13, -1.9) * mm});
            skLineSegment(sketch, "E768", {"start": v(14.13, -1.9) * mm, "end": v(14.04, -1.68) * mm});
            skLineSegment(sketch, "E769", {"start": v(14.04, -1.68) * mm, "end": v(13.95, -1.46) * mm});
            skLineSegment(sketch, "E770", {"start": v(13.95, -1.46) * mm, "end": v(13.86, -1.23) * mm});
            skLineSegment(sketch, "E771", {"start": v(13.86, -1.23) * mm, "end": v(13.77, -1) * mm});
            skLineSegment(sketch, "E772", {"start": v(13.77, -1) * mm, "end": v(13.68, -0.78) * mm});
            skLineSegment(sketch, "E773", {"start": v(13.68, -0.78) * mm, "end": v(13.59, -0.55) * mm});
            skLineSegment(sketch, "E774", {"start": v(13.59, -0.55) * mm, "end": v(13.5, -0.32) * mm});
            skLineSegment(sketch, "E775", {"start": v(13.5, -0.32) * mm, "end": v(13.4, -0.1) * mm});
            skLineSegment(sketch, "E776", {"start": v(13.4, -0.1) * mm, "end": v(13.32, 0.13) * mm});
            skLineSegment(sketch, "E777", {"start": v(13.32, 0.13) * mm, "end": v(13.23, 0.36) * mm});
            skLineSegment(sketch, "E778", {"start": v(13.23, 0.36) * mm, "end": v(13.14, 0.59) * mm});
            skLineSegment(sketch, "E779", {"start": v(13.14, 0.59) * mm, "end": v(13.05, 0.81) * mm});
            skLineSegment(sketch, "E780", {"start": v(13.05, 0.81) * mm, "end": v(12.96, 1.04) * mm});
            skLineSegment(sketch, "E781", {"start": v(12.96, 1.04) * mm, "end": v(12.87, 1.27) * mm});
            skLineSegment(sketch, "E782", {"start": v(12.87, 1.27) * mm, "end": v(12.78, 1.5) * mm});
            skLineSegment(sketch, "E783", {"start": v(12.78, 1.5) * mm, "end": v(12.68, 1.72) * mm});
            skLineSegment(sketch, "E784", {"start": v(12.68, 1.72) * mm, "end": v(12.6, 1.72) * mm});
            skLineSegment(sketch, "E785", {"start": v(12.6, 1.72) * mm, "end": v(12.51, 1.72) * mm});
            skLineSegment(sketch, "E786", {"start": v(12.51, 1.72) * mm, "end": v(12.43, 1.72) * mm});
            skLineSegment(sketch, "E787", {"start": v(12.43, 1.72) * mm, "end": v(12.34, 1.72) * mm});
            skLineSegment(sketch, "E788", {"start": v(12.34, 1.72) * mm, "end": v(12.26, 1.72) * mm});
            skLineSegment(sketch, "E789", {"start": v(12.26, 1.72) * mm, "end": v(12.17, 1.72) * mm});
            skLineSegment(sketch, "E790", {"start": v(12.17, 1.72) * mm, "end": v(12.09, 1.72) * mm});
            skLineSegment(sketch, "E791", {"start": v(12.09, 1.72) * mm, "end": v(12, 1.72) * mm});
            skLineSegment(sketch, "E792", {"start": v(12, 1.72) * mm, "end": v(11.91, 1.72) * mm});
            skLineSegment(sketch, "E793", {"start": v(11.91, 1.72) * mm, "end": v(11.83, 1.72) * mm});
            skLineSegment(sketch, "E794", {"start": v(11.83, 1.72) * mm, "end": v(11.74, 1.72) * mm});
            skLineSegment(sketch, "E795", {"start": v(11.74, 1.72) * mm, "end": v(11.66, 1.72) * mm});
            skLineSegment(sketch, "E796", {"start": v(11.66, 1.72) * mm, "end": v(11.57, 1.72) * mm});
            skLineSegment(sketch, "E797", {"start": v(11.57, 1.72) * mm, "end": v(11.49, 1.72) * mm});
            skLineSegment(sketch, "E798", {"start": v(11.49, 1.72) * mm, "end": v(11.4, 1.72) * mm});
            skLineSegment(sketch, "E799", {"start": v(11.4, 1.72) * mm, "end": v(11.32, 1.72) * mm});
            skLineSegment(sketch, "E800", {"start": v(11.98, 1.06) * mm, "end": v(12.02, 0.95) * mm});
            skLineSegment(sketch, "E801", {"start": v(12.02, 0.95) * mm, "end": v(12.06, 0.85) * mm});
            skLineSegment(sketch, "E802", {"start": v(12.06, 0.85) * mm, "end": v(12.1, 0.74) * mm});
            skLineSegment(sketch, "E803", {"start": v(12.1, 0.74) * mm, "end": v(12.14, 0.63) * mm});
            skLineSegment(sketch, "E804", {"start": v(12.14, 0.63) * mm, "end": v(12.18, 0.53) * mm});
            skLineSegment(sketch, "E805", {"start": v(12.18, 0.53) * mm, "end": v(12.21, 0.42) * mm});
            skLineSegment(sketch, "E806", {"start": v(12.21, 0.42) * mm, "end": v(12.25, 0.31) * mm});
            skLineSegment(sketch, "E807", {"start": v(12.25, 0.31) * mm, "end": v(12.3, 0.2) * mm});
            skLineSegment(sketch, "E808", {"start": v(12.3, 0.2) * mm, "end": v(12.33, 0.1) * mm});
            skLineSegment(sketch, "E809", {"start": v(12.33, 0.1) * mm, "end": v(12.37, 0) * mm});
            skLineSegment(sketch, "E810", {"start": v(12.37, 0) * mm, "end": v(12.4, -0.11) * mm});
            skLineSegment(sketch, "E811", {"start": v(12.4, -0.11) * mm, "end": v(12.45, -0.22) * mm});
            skLineSegment(sketch, "E812", {"start": v(12.45, -0.22) * mm, "end": v(12.49, -0.32) * mm});
            skLineSegment(sketch, "E813", {"start": v(12.49, -0.32) * mm, "end": v(12.52, -0.43) * mm});
            skLineSegment(sketch, "E814", {"start": v(12.52, -0.43) * mm, "end": v(12.56, -0.54) * mm});
            skLineSegment(sketch, "E815", {"start": v(12.56, -0.54) * mm, "end": v(12.6, -0.64) * mm});
            skLineSegment(sketch, "E816", {"start": v(12.6, -0.64) * mm, "end": v(12.52, -0.64) * mm});
            skLineSegment(sketch, "E817", {"start": v(12.52, -0.64) * mm, "end": v(12.44, -0.64) * mm});
            skLineSegment(sketch, "E818", {"start": v(12.44, -0.64) * mm, "end": v(12.37, -0.64) * mm});
            skLineSegment(sketch, "E819", {"start": v(12.37, -0.64) * mm, "end": v(12.29, -0.64) * mm});
            skLineSegment(sketch, "E820", {"start": v(12.29, -0.64) * mm, "end": v(12.2, -0.64) * mm});
            skLineSegment(sketch, "E821", {"start": v(12.2, -0.64) * mm, "end": v(12.13, -0.64) * mm});
            skLineSegment(sketch, "E822", {"start": v(12.13, -0.64) * mm, "end": v(12.05, -0.64) * mm});
            skLineSegment(sketch, "E823", {"start": v(12.05, -0.64) * mm, "end": v(11.97, -0.64) * mm});
            skLineSegment(sketch, "E824", {"start": v(11.97, -0.64) * mm, "end": v(11.9, -0.64) * mm});
            skLineSegment(sketch, "E825", {"start": v(11.9, -0.64) * mm, "end": v(11.81, -0.64) * mm});
            skLineSegment(sketch, "E826", {"start": v(11.81, -0.64) * mm, "end": v(11.73, -0.64) * mm});
            skLineSegment(sketch, "E827", {"start": v(11.73, -0.64) * mm, "end": v(11.66, -0.64) * mm});
            skLineSegment(sketch, "E828", {"start": v(11.66, -0.64) * mm, "end": v(11.58, -0.64) * mm});
            skLineSegment(sketch, "E829", {"start": v(11.58, -0.64) * mm, "end": v(11.5, -0.64) * mm});
            skLineSegment(sketch, "E830", {"start": v(11.5, -0.64) * mm, "end": v(11.42, -0.64) * mm});
            skLineSegment(sketch, "E831", {"start": v(11.42, -0.64) * mm, "end": v(11.34, -0.64) * mm});
            skLineSegment(sketch, "E832", {"start": v(11.34, -0.64) * mm, "end": v(11.38, -0.54) * mm});
            skLineSegment(sketch, "E833", {"start": v(11.38, -0.54) * mm, "end": v(11.42, -0.43) * mm});
            skLineSegment(sketch, "E834", {"start": v(11.42, -0.43) * mm, "end": v(11.46, -0.32) * mm});
            skLineSegment(sketch, "E835", {"start": v(11.46, -0.32) * mm, "end": v(11.5, -0.22) * mm});
            skLineSegment(sketch, "E836", {"start": v(11.5, -0.22) * mm, "end": v(11.54, -0.11) * mm});
            skLineSegment(sketch, "E837", {"start": v(11.54, -0.11) * mm, "end": v(11.58, 0) * mm});
            skLineSegment(sketch, "E838", {"start": v(11.58, 0) * mm, "end": v(11.62, 0.1) * mm});
            skLineSegment(sketch, "E839", {"start": v(11.62, 0.1) * mm, "end": v(11.66, 0.2) * mm});
            skLineSegment(sketch, "E840", {"start": v(11.66, 0.2) * mm, "end": v(11.7, 0.31) * mm});
            skLineSegment(sketch, "E841", {"start": v(11.7, 0.31) * mm, "end": v(11.74, 0.42) * mm});
            skLineSegment(sketch, "E842", {"start": v(11.74, 0.42) * mm, "end": v(11.78, 0.53) * mm});
            skLineSegment(sketch, "E843", {"start": v(11.78, 0.53) * mm, "end": v(11.82, 0.63) * mm});
            skLineSegment(sketch, "E844", {"start": v(11.82, 0.63) * mm, "end": v(11.86, 0.74) * mm});
            skLineSegment(sketch, "E845", {"start": v(11.86, 0.74) * mm, "end": v(11.9, 0.85) * mm});
            skLineSegment(sketch, "E846", {"start": v(11.9, 0.85) * mm, "end": v(11.94, 0.95) * mm});
            skLineSegment(sketch, "E847", {"start": v(11.94, 0.95) * mm, "end": v(11.98, 1.06) * mm});
            skLineSegment(sketch, "E848", {"start": v(15.83, -3.35) * mm, "end": v(-15.83, -3.35) * mm});
            skLineSegment(sketch, "E849", {"start": v(-15.83, -3.35) * mm, "end": v(-15.83, 3.35) * mm});
            skLineSegment(sketch, "E850", {"start": v(-15.83, 3.35) * mm, "end": v(15.83, 3.35) * mm});
            skLineSegment(sketch, "E851", {"start": v(15.83, 3.35) * mm, "end": v(15.83, -3.35) * mm});
            skLineSegment(sketch, "E852", {"start": v(-11.54, 1.12) * mm, "end": v(-11.54, 1.15) * mm});
            skLineSegment(sketch, "E853", {"start": v(-11.54, 1.15) * mm, "end": v(-11.54, 1.18) * mm});
            skLineSegment(sketch, "E854", {"start": v(-11.54, 1.18) * mm, "end": v(-11.54, 1.2) * mm});
            skLineSegment(sketch, "E855", {"start": v(-11.54, 1.2) * mm, "end": v(-11.54, 1.24) * mm});
            skLineSegment(sketch, "E856", {"start": v(-11.54, 1.24) * mm, "end": v(-11.54, 1.27) * mm});
            skLineSegment(sketch, "E857", {"start": v(-11.54, 1.27) * mm, "end": v(-11.54, 1.3) * mm});
            skLineSegment(sketch, "E858", {"start": v(-11.54, 1.3) * mm, "end": v(-11.54, 1.33) * mm});
            skLineSegment(sketch, "E859", {"start": v(-11.54, 1.33) * mm, "end": v(-11.54, 1.36) * mm});
            skLineSegment(sketch, "E860", {"start": v(-11.54, 1.36) * mm, "end": v(-11.54, 1.4) * mm});
            skLineSegment(sketch, "E861", {"start": v(-11.54, 1.4) * mm, "end": v(-11.54, 1.43) * mm});
            skLineSegment(sketch, "E862", {"start": v(-11.54, 1.43) * mm, "end": v(-11.54, 1.46) * mm});
            skLineSegment(sketch, "E863", {"start": v(-11.54, 1.46) * mm, "end": v(-11.54, 1.49) * mm});
            skLineSegment(sketch, "E864", {"start": v(-11.54, 1.49) * mm, "end": v(-11.54, 1.52) * mm});
            skLineSegment(sketch, "E865", {"start": v(-11.54, 1.52) * mm, "end": v(-11.54, 1.55) * mm});
            skLineSegment(sketch, "E866", {"start": v(-11.54, 1.55) * mm, "end": v(-11.54, 1.58) * mm});
            skLineSegment(sketch, "E867", {"start": v(-11.54, 1.58) * mm, "end": v(-11.54, 1.61) * mm});
            skLineSegment(sketch, "E868", {"start": v(-11.54, 1.61) * mm, "end": v(-11.53, 1.62) * mm});
            skLineSegment(sketch, "E869", {"start": v(-11.53, 1.62) * mm, "end": v(-11.52, 1.62) * mm});
            skLineSegment(sketch, "E870", {"start": v(-11.52, 1.62) * mm, "end": v(-11.52, 1.62) * mm});
            skLineSegment(sketch, "E871", {"start": v(-11.52, 1.62) * mm, "end": v(-11.5, 1.62) * mm});
            skLineSegment(sketch, "E872", {"start": v(-11.5, 1.62) * mm, "end": v(-11.5, 1.62) * mm});
            skLineSegment(sketch, "E873", {"start": v(-11.5, 1.62) * mm, "end": v(-11.49, 1.62) * mm});
            skLineSegment(sketch, "E874", {"start": v(-11.49, 1.62) * mm, "end": v(-11.48, 1.62) * mm});
            skLineSegment(sketch, "E875", {"start": v(-11.48, 1.62) * mm, "end": v(-11.47, 1.62) * mm});
            skLineSegment(sketch, "E876", {"start": v(-11.47, 1.62) * mm, "end": v(-11.46, 1.62) * mm});
            skLineSegment(sketch, "E877", {"start": v(-11.46, 1.62) * mm, "end": v(-11.45, 1.62) * mm});
            skLineSegment(sketch, "E878", {"start": v(-11.45, 1.62) * mm, "end": v(-11.44, 1.62) * mm});
            skLineSegment(sketch, "E879", {"start": v(-11.44, 1.62) * mm, "end": v(-11.43, 1.62) * mm});
            skLineSegment(sketch, "E880", {"start": v(-11.43, 1.62) * mm, "end": v(-11.42, 1.62) * mm});
            skLineSegment(sketch, "E881", {"start": v(-11.42, 1.62) * mm, "end": v(-11.41, 1.62) * mm});
            skLineSegment(sketch, "E882", {"start": v(-11.41, 1.62) * mm, "end": v(-11.4, 1.62) * mm});
            skLineSegment(sketch, "E883", {"start": v(-11.4, 1.62) * mm, "end": v(-11.4, 1.62) * mm});
            skLineSegment(sketch, "E884", {"start": v(-11.4, 1.62) * mm, "end": v(-11.14, 1.62) * mm});
            skLineSegment(sketch, "E885", {"start": v(-11.14, 1.62) * mm, "end": v(-10.9, 1.58) * mm});
            skLineSegment(sketch, "E886", {"start": v(-10.9, 1.58) * mm, "end": v(-10.68, 1.53) * mm});
            skLineSegment(sketch, "E887", {"start": v(-10.68, 1.53) * mm, "end": v(-10.46, 1.46) * mm});
            skLineSegment(sketch, "E888", {"start": v(-10.46, 1.46) * mm, "end": v(-10.26, 1.37) * mm});
            skLineSegment(sketch, "E889", {"start": v(-10.26, 1.37) * mm, "end": v(-10.08, 1.27) * mm});
            skLineSegment(sketch, "E890", {"start": v(-10.08, 1.27) * mm, "end": v(-9.9, 1.16) * mm});
            skLineSegment(sketch, "E891", {"start": v(-9.9, 1.16) * mm, "end": v(-9.75, 1.05) * mm});
            skLineSegment(sketch, "E892", {"start": v(-9.75, 1.05) * mm, "end": v(-9.6, 0.94) * mm});
            skLineSegment(sketch, "E893", {"start": v(-9.6, 0.94) * mm, "end": v(-9.48, 0.83) * mm});
            skLineSegment(sketch, "E894", {"start": v(-9.48, 0.83) * mm, "end": v(-9.38, 0.73) * mm});
            skLineSegment(sketch, "E895", {"start": v(-9.38, 0.73) * mm, "end": v(-9.3, 0.64) * mm});
            skLineSegment(sketch, "E896", {"start": v(-9.3, 0.64) * mm, "end": v(-9.22, 0.56) * mm});
            skLineSegment(sketch, "E897", {"start": v(-9.22, 0.56) * mm, "end": v(-9.17, 0.5) * mm});
            skLineSegment(sketch, "E898", {"start": v(-9.17, 0.5) * mm, "end": v(-9.14, 0.46) * mm});
            skLineSegment(sketch, "E899", {"start": v(-9.14, 0.46) * mm, "end": v(-9.13, 0.45) * mm});
            skLineSegment(sketch, "E900", {"start": v(-9.13, 0.45) * mm, "end": v(-9.14, 0.43) * mm});
            skLineSegment(sketch, "E901", {"start": v(-9.14, 0.43) * mm, "end": v(-9.17, 0.4) * mm});
            skLineSegment(sketch, "E902", {"start": v(-9.17, 0.4) * mm, "end": v(-9.22, 0.32) * mm});
            skLineSegment(sketch, "E903", {"start": v(-9.22, 0.32) * mm, "end": v(-9.3, 0.24) * mm});
            skLineSegment(sketch, "E904", {"start": v(-9.3, 0.24) * mm, "end": v(-9.39, 0.14) * mm});
            skLineSegment(sketch, "E905", {"start": v(-9.39, 0.14) * mm, "end": v(-9.5, 0.02) * mm});
            skLineSegment(sketch, "E906", {"start": v(-9.5, 0.02) * mm, "end": v(-9.61, -0.1) * mm});
            skLineSegment(sketch, "E907", {"start": v(-9.61, -0.1) * mm, "end": v(-9.74, -0.22) * mm});
            skLineSegment(sketch, "E908", {"start": v(-9.74, -0.22) * mm, "end": v(-9.89, -0.35) * mm});
            skLineSegment(sketch, "E909", {"start": v(-9.89, -0.35) * mm, "end": v(-10.05, -0.47) * mm});
            skLineSegment(sketch, "E910", {"start": v(-10.05, -0.47) * mm, "end": v(-10.21, -0.58) * mm});
            skLineSegment(sketch, "E911", {"start": v(-10.21, -0.58) * mm, "end": v(-10.39, -0.69) * mm});
            skLineSegment(sketch, "E912", {"start": v(-10.39, -0.69) * mm, "end": v(-10.57, -0.77) * mm});
            skLineSegment(sketch, "E913", {"start": v(-10.57, -0.77) * mm, "end": v(-10.75, -0.84) * mm});
            skLineSegment(sketch, "E914", {"start": v(-10.75, -0.84) * mm, "end": v(-10.94, -0.88) * mm});
            skLineSegment(sketch, "E915", {"start": v(-10.94, -0.88) * mm, "end": v(-11.14, -0.9) * mm});
            skLineSegment(sketch, "E916", {"start": v(-11.14, -0.9) * mm, "end": v(-11.17, -0.9) * mm});
            skLineSegment(sketch, "E917", {"start": v(-11.17, -0.9) * mm, "end": v(-11.2, -0.9) * mm});
            skLineSegment(sketch, "E918", {"start": v(-11.2, -0.9) * mm, "end": v(-11.22, -0.9) * mm});
            skLineSegment(sketch, "E919", {"start": v(-11.22, -0.9) * mm, "end": v(-11.25, -0.9) * mm});
            skLineSegment(sketch, "E920", {"start": v(-11.25, -0.9) * mm, "end": v(-11.27, -0.89) * mm});
            skLineSegment(sketch, "E921", {"start": v(-11.27, -0.89) * mm, "end": v(-11.3, -0.89) * mm});
            skLineSegment(sketch, "E922", {"start": v(-11.3, -0.89) * mm, "end": v(-11.33, -0.88) * mm});
            skLineSegment(sketch, "E923", {"start": v(-11.33, -0.88) * mm, "end": v(-11.35, -0.88) * mm});
            skLineSegment(sketch, "E924", {"start": v(-11.35, -0.88) * mm, "end": v(-11.38, -0.88) * mm});
            skLineSegment(sketch, "E925", {"start": v(-11.38, -0.88) * mm, "end": v(-11.4, -0.87) * mm});
            skLineSegment(sketch, "E926", {"start": v(-11.4, -0.87) * mm, "end": v(-11.43, -0.87) * mm});
            skLineSegment(sketch, "E927", {"start": v(-11.43, -0.87) * mm, "end": v(-11.45, -0.86) * mm});
            skLineSegment(sketch, "E928", {"start": v(-11.45, -0.86) * mm, "end": v(-11.47, -0.85) * mm});
            skLineSegment(sketch, "E929", {"start": v(-11.47, -0.85) * mm, "end": v(-11.5, -0.85) * mm});
            skLineSegment(sketch, "E930", {"start": v(-11.5, -0.85) * mm, "end": v(-11.52, -0.84) * mm});
            skLineSegment(sketch, "E931", {"start": v(-11.52, -0.84) * mm, "end": v(-11.54, -0.83) * mm});
            skLineSegment(sketch, "E932", {"start": v(-11.54, -0.83) * mm, "end": v(-11.54, -0.74) * mm});
            skLineSegment(sketch, "E933", {"start": v(-11.54, -0.74) * mm, "end": v(-11.54, -0.64) * mm});
            skLineSegment(sketch, "E934", {"start": v(-11.54, -0.64) * mm, "end": v(-11.54, -0.55) * mm});
            skLineSegment(sketch, "E935", {"start": v(-11.54, -0.55) * mm, "end": v(-11.54, -0.45) * mm});
            skLineSegment(sketch, "E936", {"start": v(-11.54, -0.45) * mm, "end": v(-11.54, -0.36) * mm});
            skLineSegment(sketch, "E937", {"start": v(-11.54, -0.36) * mm, "end": v(-11.54, -0.26) * mm});
            skLineSegment(sketch, "E938", {"start": v(-11.54, -0.26) * mm, "end": v(-11.54, -0.17) * mm});
            skLineSegment(sketch, "E939", {"start": v(-11.54, -0.17) * mm, "end": v(-11.54, -0.07) * mm});
            skLineSegment(sketch, "E940", {"start": v(-11.54, -0.07) * mm, "end": v(-11.54, 0.02) * mm});
            skLineSegment(sketch, "E941", {"start": v(-11.54, 0.02) * mm, "end": v(-11.54, 0.11) * mm});
            skLineSegment(sketch, "E942", {"start": v(-11.54, 0.11) * mm, "end": v(-11.54, 0.2) * mm});
            skLineSegment(sketch, "E943", {"start": v(-11.54, 0.2) * mm, "end": v(-11.54, 0.3) * mm});
            skLineSegment(sketch, "E944", {"start": v(-11.54, 0.3) * mm, "end": v(-11.54, 0.4) * mm});
            skLineSegment(sketch, "E945", {"start": v(-11.54, 0.4) * mm, "end": v(-11.54, 0.5) * mm});
            skLineSegment(sketch, "E946", {"start": v(-11.54, 0.5) * mm, "end": v(-11.54, 0.59) * mm});
            skLineSegment(sketch, "E947", {"start": v(-11.54, 0.59) * mm, "end": v(-11.54, 0.68) * mm});
            skLineSegment(sketch, "E948", {"start": v(-11.54, 0.68) * mm, "end": v(-11.45, 0.67) * mm});
            skLineSegment(sketch, "E949", {"start": v(-11.45, 0.67) * mm, "end": v(-11.36, 0.65) * mm});
            skLineSegment(sketch, "E950", {"start": v(-11.36, 0.65) * mm, "end": v(-11.28, 0.63) * mm});
            skLineSegment(sketch, "E951", {"start": v(-11.28, 0.63) * mm, "end": v(-11.21, 0.6) * mm});
            skLineSegment(sketch, "E952", {"start": v(-11.21, 0.6) * mm, "end": v(-11.15, 0.57) * mm});
            skLineSegment(sketch, "E953", {"start": v(-11.15, 0.57) * mm, "end": v(-11.09, 0.53) * mm});
            skLineSegment(sketch, "E954", {"start": v(-11.09, 0.53) * mm, "end": v(-11.03, 0.49) * mm});
            skLineSegment(sketch, "E955", {"start": v(-11.03, 0.49) * mm, "end": v(-10.98, 0.44) * mm});
            skLineSegment(sketch, "E956", {"start": v(-10.98, 0.44) * mm, "end": v(-10.93, 0.39) * mm});
            skLineSegment(sketch, "E957", {"start": v(-10.93, 0.39) * mm, "end": v(-10.89, 0.33) * mm});
            skLineSegment(sketch, "E958", {"start": v(-10.89, 0.33) * mm, "end": v(-10.84, 0.27) * mm});
            skLineSegment(sketch, "E959", {"start": v(-10.84, 0.27) * mm, "end": v(-10.8, 0.2) * mm});
            skLineSegment(sketch, "E960", {"start": v(-10.8, 0.2) * mm, "end": v(-10.74, 0.12) * mm});
            skLineSegment(sketch, "E961", {"start": v(-10.74, 0.12) * mm, "end": v(-10.7, 0.04) * mm});
            skLineSegment(sketch, "E962", {"start": v(-10.7, 0.04) * mm, "end": v(-10.64, -0.05) * mm});
            skLineSegment(sketch, "E963", {"start": v(-10.64, -0.05) * mm, "end": v(-10.58, -0.15) * mm});
            skLineSegment(sketch, "E964", {"start": v(-10.58, -0.15) * mm, "end": v(-10.54, -0.11) * mm});
            skLineSegment(sketch, "E965", {"start": v(-10.54, -0.11) * mm, "end": v(-10.5, -0.07) * mm});
            skLineSegment(sketch, "E966", {"start": v(-10.5, -0.07) * mm, "end": v(-10.45, -0.04) * mm});
            skLineSegment(sketch, "E967", {"start": v(-10.45, -0.04) * mm, "end": v(-10.4, 0) * mm});
            skLineSegment(sketch, "E968", {"start": v(-10.4, 0) * mm, "end": v(-10.36, 0.04) * mm});
            skLineSegment(sketch, "E969", {"start": v(-10.36, 0.04) * mm, "end": v(-10.32, 0.08) * mm});
            skLineSegment(sketch, "E970", {"start": v(-10.32, 0.08) * mm, "end": v(-10.27, 0.11) * mm});
            skLineSegment(sketch, "E971", {"start": v(-10.27, 0.11) * mm, "end": v(-10.23, 0.15) * mm});
            skLineSegment(sketch, "E972", {"start": v(-10.23, 0.15) * mm, "end": v(-10.18, 0.19) * mm});
            skLineSegment(sketch, "E973", {"start": v(-10.18, 0.19) * mm, "end": v(-10.14, 0.23) * mm});
            skLineSegment(sketch, "E974", {"start": v(-10.14, 0.23) * mm, "end": v(-10.1, 0.26) * mm});
            skLineSegment(sketch, "E975", {"start": v(-10.1, 0.26) * mm, "end": v(-10.05, 0.3) * mm});
            skLineSegment(sketch, "E976", {"start": v(-10.05, 0.3) * mm, "end": v(-10, 0.34) * mm});
            skLineSegment(sketch, "E977", {"start": v(-10, 0.34) * mm, "end": v(-9.96, 0.38) * mm});
            skLineSegment(sketch, "E978", {"start": v(-9.96, 0.38) * mm, "end": v(-9.91, 0.41) * mm});
            skLineSegment(sketch, "E979", {"start": v(-9.91, 0.41) * mm, "end": v(-9.87, 0.45) * mm});
            skLineSegment(sketch, "E980", {"start": v(-9.87, 0.45) * mm, "end": v(-9.88, 0.46) * mm});
            skLineSegment(sketch, "E981", {"start": v(-9.88, 0.46) * mm, "end": v(-9.9, 0.48) * mm});
            skLineSegment(sketch, "E982", {"start": v(-9.9, 0.48) * mm, "end": v(-9.92, 0.51) * mm});
            skLineSegment(sketch, "E983", {"start": v(-9.92, 0.51) * mm, "end": v(-9.96, 0.56) * mm});
            skLineSegment(sketch, "E984", {"start": v(-9.96, 0.56) * mm, "end": v(-10.02, 0.6) * mm});
            skLineSegment(sketch, "E985", {"start": v(-10.02, 0.6) * mm, "end": v(-10.08, 0.67) * mm});
            skLineSegment(sketch, "E986", {"start": v(-10.08, 0.67) * mm, "end": v(-10.15, 0.73) * mm});
            skLineSegment(sketch, "E987", {"start": v(-10.15, 0.73) * mm, "end": v(-10.24, 0.8) * mm});
            skLineSegment(sketch, "E988", {"start": v(-10.24, 0.8) * mm, "end": v(-10.33, 0.85) * mm});
            skLineSegment(sketch, "E989", {"start": v(-10.33, 0.85) * mm, "end": v(-10.44, 0.92) * mm});
            skLineSegment(sketch, "E990", {"start": v(-10.44, 0.92) * mm, "end": v(-10.55, 0.97) * mm});
            skLineSegment(sketch, "E991", {"start": v(-10.55, 0.97) * mm, "end": v(-10.68, 1.03) * mm});
            skLineSegment(sketch, "E992", {"start": v(-10.68, 1.03) * mm, "end": v(-10.81, 1.07) * mm});
            skLineSegment(sketch, "E993", {"start": v(-10.81, 1.07) * mm, "end": v(-10.95, 1.1) * mm});
            skLineSegment(sketch, "E994", {"start": v(-10.95, 1.1) * mm, "end": v(-11.1, 1.12) * mm});
            skLineSegment(sketch, "E995", {"start": v(-11.1, 1.12) * mm, "end": v(-11.27, 1.13) * mm});
            skLineSegment(sketch, "E996", {"start": v(-11.27, 1.13) * mm, "end": v(-11.28, 1.13) * mm});
            skLineSegment(sketch, "E997", {"start": v(-11.28, 1.13) * mm, "end": v(-11.3, 1.13) * mm});
            skLineSegment(sketch, "E998", {"start": v(-11.3, 1.13) * mm, "end": v(-11.32, 1.13) * mm});
            skLineSegment(sketch, "E999", {"start": v(-11.32, 1.13) * mm, "end": v(-11.34, 1.13) * mm});
            skLineSegment(sketch, "E1000", {"start": v(-11.34, 1.13) * mm, "end": v(-11.35, 1.13) * mm});
            skLineSegment(sketch, "E1001", {"start": v(-11.35, 1.13) * mm, "end": v(-11.37, 1.13) * mm});
            skLineSegment(sketch, "E1002", {"start": v(-11.37, 1.13) * mm, "end": v(-11.39, 1.13) * mm});
            skLineSegment(sketch, "E1003", {"start": v(-11.39, 1.13) * mm, "end": v(-11.4, 1.13) * mm});
            skLineSegment(sketch, "E1004", {"start": v(-11.4, 1.13) * mm, "end": v(-11.42, 1.13) * mm});
            skLineSegment(sketch, "E1005", {"start": v(-11.42, 1.13) * mm, "end": v(-11.44, 1.12) * mm});
            skLineSegment(sketch, "E1006", {"start": v(-11.44, 1.12) * mm, "end": v(-11.46, 1.12) * mm});
            skLineSegment(sketch, "E1007", {"start": v(-11.46, 1.12) * mm, "end": v(-11.47, 1.12) * mm});
            skLineSegment(sketch, "E1008", {"start": v(-11.47, 1.12) * mm, "end": v(-11.5, 1.12) * mm});
            skLineSegment(sketch, "E1009", {"start": v(-11.5, 1.12) * mm, "end": v(-11.5, 1.12) * mm});
            skLineSegment(sketch, "E1010", {"start": v(-11.5, 1.12) * mm, "end": v(-11.53, 1.12) * mm});
            skLineSegment(sketch, "E1011", {"start": v(-11.53, 1.12) * mm, "end": v(-11.54, 1.12) * mm});
            skLineSegment(sketch, "E1012", {"start": v(-11.54, 2.77) * mm, "end": v(-11.54, 2.72) * mm});
            skLineSegment(sketch, "E1013", {"start": v(-11.54, 2.72) * mm, "end": v(-11.54, 2.67) * mm});
            skLineSegment(sketch, "E1014", {"start": v(-11.54, 2.67) * mm, "end": v(-11.54, 2.63) * mm});
            skLineSegment(sketch, "E1015", {"start": v(-11.54, 2.63) * mm, "end": v(-11.54, 2.58) * mm});
            skLineSegment(sketch, "E1016", {"start": v(-11.54, 2.58) * mm, "end": v(-11.54, 2.53) * mm});
            skLineSegment(sketch, "E1017", {"start": v(-11.54, 2.53) * mm, "end": v(-11.54, 2.49) * mm});
            skLineSegment(sketch, "E1018", {"start": v(-11.54, 2.49) * mm, "end": v(-11.54, 2.44) * mm});
            skLineSegment(sketch, "E1019", {"start": v(-11.54, 2.44) * mm, "end": v(-11.54, 2.4) * mm});
            skLineSegment(sketch, "E1020", {"start": v(-11.54, 2.4) * mm, "end": v(-11.54, 2.35) * mm});
            skLineSegment(sketch, "E1021", {"start": v(-11.54, 2.35) * mm, "end": v(-11.54, 2.3) * mm});
            skLineSegment(sketch, "E1022", {"start": v(-11.54, 2.3) * mm, "end": v(-11.54, 2.25) * mm});
            skLineSegment(sketch, "E1023", {"start": v(-11.54, 2.25) * mm, "end": v(-11.54, 2.2) * mm});
            skLineSegment(sketch, "E1024", {"start": v(-11.54, 2.2) * mm, "end": v(-11.54, 2.16) * mm});
            skLineSegment(sketch, "E1025", {"start": v(-11.54, 2.16) * mm, "end": v(-11.54, 2.11) * mm});
            skLineSegment(sketch, "E1026", {"start": v(-11.54, 2.11) * mm, "end": v(-11.54, 2.07) * mm});
            skLineSegment(sketch, "E1027", {"start": v(-11.54, 2.07) * mm, "end": v(-11.54, 2.02) * mm});
            skLineSegment(sketch, "E1028", {"start": v(-11.54, 2.02) * mm, "end": v(-11.53, 2.02) * mm});
            skLineSegment(sketch, "E1029", {"start": v(-11.53, 2.02) * mm, "end": v(-11.52, 2.02) * mm});
            skLineSegment(sketch, "E1030", {"start": v(-11.52, 2.02) * mm, "end": v(-11.51, 2.02) * mm});
            skLineSegment(sketch, "E1031", {"start": v(-11.51, 2.02) * mm, "end": v(-11.5, 2.02) * mm});
            skLineSegment(sketch, "E1032", {"start": v(-11.5, 2.02) * mm, "end": v(-11.5, 2.02) * mm});
            skLineSegment(sketch, "E1033", {"start": v(-11.5, 2.02) * mm, "end": v(-11.49, 2.02) * mm});
            skLineSegment(sketch, "E1034", {"start": v(-11.49, 2.02) * mm, "end": v(-11.48, 2.02) * mm});
            skLineSegment(sketch, "E1035", {"start": v(-11.48, 2.02) * mm, "end": v(-11.47, 2.02) * mm});
            skLineSegment(sketch, "E1036", {"start": v(-11.47, 2.02) * mm, "end": v(-11.46, 2.03) * mm});
            skLineSegment(sketch, "E1037", {"start": v(-11.46, 2.03) * mm, "end": v(-11.45, 2.03) * mm});
            skLineSegment(sketch, "E1038", {"start": v(-11.45, 2.03) * mm, "end": v(-11.44, 2.03) * mm});
            skLineSegment(sketch, "E1039", {"start": v(-11.44, 2.03) * mm, "end": v(-11.43, 2.03) * mm});
            skLineSegment(sketch, "E1040", {"start": v(-11.43, 2.03) * mm, "end": v(-11.42, 2.03) * mm});
            skLineSegment(sketch, "E1041", {"start": v(-11.42, 2.03) * mm, "end": v(-11.41, 2.03) * mm});
            skLineSegment(sketch, "E1042", {"start": v(-11.41, 2.03) * mm, "end": v(-11.4, 2.03) * mm});
            skLineSegment(sketch, "E1043", {"start": v(-11.4, 2.03) * mm, "end": v(-11.4, 2.03) * mm});
            skLineSegment(sketch, "E1044", {"start": v(-11.4, 2.03) * mm, "end": v(-11.05, 2.02) * mm});
            skLineSegment(sketch, "E1045", {"start": v(-11.05, 2.02) * mm, "end": v(-10.71, 1.98) * mm});
            skLineSegment(sketch, "E1046", {"start": v(-10.71, 1.98) * mm, "end": v(-10.4, 1.9) * mm});
            skLineSegment(sketch, "E1047", {"start": v(-10.4, 1.9) * mm, "end": v(-10.1, 1.81) * mm});
            skLineSegment(sketch, "E1048", {"start": v(-10.1, 1.81) * mm, "end": v(-9.82, 1.7) * mm});
            skLineSegment(sketch, "E1049", {"start": v(-9.82, 1.7) * mm, "end": v(-9.56, 1.56) * mm});
            skLineSegment(sketch, "E1050", {"start": v(-9.56, 1.56) * mm, "end": v(-9.33, 1.42) * mm});
            skLineSegment(sketch, "E1051", {"start": v(-9.33, 1.42) * mm, "end": v(-9.1, 1.27) * mm});
            skLineSegment(sketch, "E1052", {"start": v(-9.1, 1.27) * mm, "end": v(-8.92, 1.12) * mm});
            skLineSegment(sketch, "E1053", {"start": v(-8.92, 1.12) * mm, "end": v(-8.74, 0.98) * mm});
            skLineSegment(sketch, "E1054", {"start": v(-8.74, 0.98) * mm, "end": v(-8.6, 0.84) * mm});
            skLineSegment(sketch, "E1055", {"start": v(-8.6, 0.84) * mm, "end": v(-8.48, 0.72) * mm});
            skLineSegment(sketch, "E1056", {"start": v(-8.48, 0.72) * mm, "end": v(-8.38, 0.62) * mm});
            skLineSegment(sketch, "E1057", {"start": v(-8.38, 0.62) * mm, "end": v(-8.3, 0.54) * mm});
            skLineSegment(sketch, "E1058", {"start": v(-8.3, 0.54) * mm, "end": v(-8.27, 0.49) * mm});
            skLineSegment(sketch, "E1059", {"start": v(-8.27, 0.49) * mm, "end": v(-8.25, 0.47) * mm});
            skLineSegment(sketch, "E1060", {"start": v(-8.25, 0.47) * mm, "end": v(-8.27, 0.45) * mm});
            skLineSegment(sketch, "E1061", {"start": v(-8.27, 0.45) * mm, "end": v(-8.32, 0.4) * mm});
            skLineSegment(sketch, "E1062", {"start": v(-8.32, 0.4) * mm, "end": v(-8.4, 0.3) * mm});
            skLineSegment(sketch, "E1063", {"start": v(-8.4, 0.3) * mm, "end": v(-8.5, 0.2) * mm});
            skLineSegment(sketch, "E1064", {"start": v(-8.5, 0.2) * mm, "end": v(-8.63, 0.07) * mm});
            skLineSegment(sketch, "E1065", {"start": v(-8.63, 0.07) * mm, "end": v(-8.78, -0.08) * mm});
            skLineSegment(sketch, "E1066", {"start": v(-8.78, -0.08) * mm, "end": v(-8.96, -0.23) * mm});
            skLineSegment(sketch, "E1067", {"start": v(-8.96, -0.23) * mm, "end": v(-9.15, -0.4) * mm});
            skLineSegment(sketch, "E1068", {"start": v(-9.15, -0.4) * mm, "end": v(-9.36, -0.56) * mm});
            skLineSegment(sketch, "E1069", {"start": v(-9.36, -0.56) * mm, "end": v(-9.59, -0.71) * mm});
            skLineSegment(sketch, "E1070", {"start": v(-9.59, -0.71) * mm, "end": v(-9.83, -0.86) * mm});
            skLineSegment(sketch, "E1071", {"start": v(-9.83, -0.86) * mm, "end": v(-10.08, -0.99) * mm});
            skLineSegment(sketch, "E1072", {"start": v(-10.08, -0.99) * mm, "end": v(-10.34, -1.1) * mm});
            skLineSegment(sketch, "E1073", {"start": v(-10.34, -1.1) * mm, "end": v(-10.6, -1.19) * mm});
            skLineSegment(sketch, "E1074", {"start": v(-10.6, -1.19) * mm, "end": v(-10.88, -1.24) * mm});
            skLineSegment(sketch, "E1075", {"start": v(-10.88, -1.24) * mm, "end": v(-11.16, -1.26) * mm});
            skLineSegment(sketch, "E1076", {"start": v(-11.16, -1.26) * mm, "end": v(-11.19, -1.26) * mm});
            skLineSegment(sketch, "E1077", {"start": v(-11.19, -1.26) * mm, "end": v(-11.21, -1.26) * mm});
            skLineSegment(sketch, "E1078", {"start": v(-11.21, -1.26) * mm, "end": v(-11.24, -1.26) * mm});
            skLineSegment(sketch, "E1079", {"start": v(-11.24, -1.26) * mm, "end": v(-11.26, -1.26) * mm});
            skLineSegment(sketch, "E1080", {"start": v(-11.26, -1.26) * mm, "end": v(-11.28, -1.26) * mm});
            skLineSegment(sketch, "E1081", {"start": v(-11.28, -1.26) * mm, "end": v(-11.3, -1.26) * mm});
            skLineSegment(sketch, "E1082", {"start": v(-11.3, -1.26) * mm, "end": v(-11.33, -1.25) * mm});
            skLineSegment(sketch, "E1083", {"start": v(-11.33, -1.25) * mm, "end": v(-11.36, -1.25) * mm});
            skLineSegment(sketch, "E1084", {"start": v(-11.36, -1.25) * mm, "end": v(-11.38, -1.25) * mm});
            skLineSegment(sketch, "E1085", {"start": v(-11.38, -1.25) * mm, "end": v(-11.4, -1.25) * mm});
            skLineSegment(sketch, "E1086", {"start": v(-11.4, -1.25) * mm, "end": v(-11.43, -1.24) * mm});
            skLineSegment(sketch, "E1087", {"start": v(-11.43, -1.24) * mm, "end": v(-11.45, -1.24) * mm});
            skLineSegment(sketch, "E1088", {"start": v(-11.45, -1.24) * mm, "end": v(-11.47, -1.24) * mm});
            skLineSegment(sketch, "E1089", {"start": v(-11.47, -1.24) * mm, "end": v(-11.5, -1.23) * mm});
            skLineSegment(sketch, "E1090", {"start": v(-11.5, -1.23) * mm, "end": v(-11.52, -1.23) * mm});
            skLineSegment(sketch, "E1091", {"start": v(-11.52, -1.23) * mm, "end": v(-11.54, -1.23) * mm});
            skLineSegment(sketch, "E1092", {"start": v(-11.54, -1.23) * mm, "end": v(-11.54, -1.26) * mm});
            skLineSegment(sketch, "E1093", {"start": v(-11.54, -1.26) * mm, "end": v(-11.54, -1.28) * mm});
            skLineSegment(sketch, "E1094", {"start": v(-11.54, -1.28) * mm, "end": v(-11.54, -1.31) * mm});
            skLineSegment(sketch, "E1095", {"start": v(-11.54, -1.31) * mm, "end": v(-11.54, -1.34) * mm});
            skLineSegment(sketch, "E1096", {"start": v(-11.54, -1.34) * mm, "end": v(-11.54, -1.37) * mm});
            skLineSegment(sketch, "E1097", {"start": v(-11.54, -1.37) * mm, "end": v(-11.54, -1.4) * mm});
            skLineSegment(sketch, "E1098", {"start": v(-11.54, -1.4) * mm, "end": v(-11.54, -1.43) * mm});
            skLineSegment(sketch, "E1099", {"start": v(-11.54, -1.43) * mm, "end": v(-11.54, -1.46) * mm});
            skLineSegment(sketch, "E1100", {"start": v(-11.54, -1.46) * mm, "end": v(-11.54, -1.49) * mm});
            skLineSegment(sketch, "E1101", {"start": v(-11.54, -1.49) * mm, "end": v(-11.54, -1.51) * mm});
            skLineSegment(sketch, "E1102", {"start": v(-11.54, -1.51) * mm, "end": v(-11.54, -1.54) * mm});
            skLineSegment(sketch, "E1103", {"start": v(-11.54, -1.54) * mm, "end": v(-11.54, -1.57) * mm});
            skLineSegment(sketch, "E1104", {"start": v(-11.54, -1.57) * mm, "end": v(-11.54, -1.6) * mm});
            skLineSegment(sketch, "E1105", {"start": v(-11.54, -1.6) * mm, "end": v(-11.54, -1.63) * mm});
            skLineSegment(sketch, "E1106", {"start": v(-11.54, -1.63) * mm, "end": v(-11.54, -1.66) * mm});
            skLineSegment(sketch, "E1107", {"start": v(-11.54, -1.66) * mm, "end": v(-11.54, -1.69) * mm});
            skLineSegment(sketch, "E1108", {"start": v(-11.54, -1.69) * mm, "end": v(-11.52, -1.69) * mm});
            skLineSegment(sketch, "E1109", {"start": v(-11.52, -1.69) * mm, "end": v(-11.5, -1.7) * mm});
            skLineSegment(sketch, "E1110", {"start": v(-11.5, -1.7) * mm, "end": v(-11.48, -1.7) * mm});
            skLineSegment(sketch, "E1111", {"start": v(-11.48, -1.7) * mm, "end": v(-11.47, -1.7) * mm});
            skLineSegment(sketch, "E1112", {"start": v(-11.47, -1.7) * mm, "end": v(-11.45, -1.7) * mm});
            skLineSegment(sketch, "E1113", {"start": v(-11.45, -1.7) * mm, "end": v(-11.43, -1.7) * mm});
            skLineSegment(sketch, "E1114", {"start": v(-11.43, -1.7) * mm, "end": v(-11.4, -1.7) * mm});
            skLineSegment(sketch, "E1115", {"start": v(-11.4, -1.7) * mm, "end": v(-11.39, -1.7) * mm});
            skLineSegment(sketch, "E1116", {"start": v(-11.39, -1.7) * mm, "end": v(-11.37, -1.7) * mm});
            skLineSegment(sketch, "E1117", {"start": v(-11.37, -1.7) * mm, "end": v(-11.35, -1.7) * mm});
            skLineSegment(sketch, "E1118", {"start": v(-11.35, -1.7) * mm, "end": v(-11.33, -1.7) * mm});
            skLineSegment(sketch, "E1119", {"start": v(-11.33, -1.7) * mm, "end": v(-11.3, -1.7) * mm});
            skLineSegment(sketch, "E1120", {"start": v(-11.3, -1.7) * mm, "end": v(-11.29, -1.7) * mm});
            skLineSegment(sketch, "E1121", {"start": v(-11.29, -1.7) * mm, "end": v(-11.27, -1.7) * mm});
            skLineSegment(sketch, "E1122", {"start": v(-11.27, -1.7) * mm, "end": v(-11.24, -1.7) * mm});
            skLineSegment(sketch, "E1123", {"start": v(-11.24, -1.7) * mm, "end": v(-11.22, -1.7) * mm});
            skLineSegment(sketch, "E1124", {"start": v(-11.22, -1.7) * mm, "end": v(-10.97, -1.7) * mm});
            skLineSegment(sketch, "E1125", {"start": v(-10.97, -1.7) * mm, "end": v(-10.72, -1.68) * mm});
            skLineSegment(sketch, "E1126", {"start": v(-10.72, -1.68) * mm, "end": v(-10.49, -1.64) * mm});
            skLineSegment(sketch, "E1127", {"start": v(-10.49, -1.64) * mm, "end": v(-10.25, -1.59) * mm});
            skLineSegment(sketch, "E1128", {"start": v(-10.25, -1.59) * mm, "end": v(-10.03, -1.52) * mm});
            skLineSegment(sketch, "E1129", {"start": v(-10.03, -1.52) * mm, "end": v(-9.81, -1.44) * mm});
            skLineSegment(sketch, "E1130", {"start": v(-9.81, -1.44) * mm, "end": v(-9.6, -1.35) * mm});
            skLineSegment(sketch, "E1131", {"start": v(-9.6, -1.35) * mm, "end": v(-9.4, -1.25) * mm});
            skLineSegment(sketch, "E1132", {"start": v(-9.4, -1.25) * mm, "end": v(-9.2, -1.14) * mm});
            skLineSegment(sketch, "E1133", {"start": v(-9.2, -1.14) * mm, "end": v(-9, -1.02) * mm});
            skLineSegment(sketch, "E1134", {"start": v(-9, -1.02) * mm, "end": v(-8.8, -0.9) * mm});
            skLineSegment(sketch, "E1135", {"start": v(-8.8, -0.9) * mm, "end": v(-8.61, -0.76) * mm});
            skLineSegment(sketch, "E1136", {"start": v(-8.61, -0.76) * mm, "end": v(-8.43, -0.62) * mm});
            skLineSegment(sketch, "E1137", {"start": v(-8.43, -0.62) * mm, "end": v(-8.24, -0.48) * mm});
            skLineSegment(sketch, "E1138", {"start": v(-8.24, -0.48) * mm, "end": v(-8.06, -0.33) * mm});
            skLineSegment(sketch, "E1139", {"start": v(-8.06, -0.33) * mm, "end": v(-7.88, -0.17) * mm});
            skLineSegment(sketch, "E1140", {"start": v(-7.88, -0.17) * mm, "end": v(-7.84, -0.2) * mm});
            skLineSegment(sketch, "E1141", {"start": v(-7.84, -0.2) * mm, "end": v(-7.8, -0.23) * mm});
            skLineSegment(sketch, "E1142", {"start": v(-7.8, -0.23) * mm, "end": v(-7.74, -0.26) * mm});
            skLineSegment(sketch, "E1143", {"start": v(-7.74, -0.26) * mm, "end": v(-7.68, -0.3) * mm});
            skLineSegment(sketch, "E1144", {"start": v(-7.68, -0.3) * mm, "end": v(-7.61, -0.33) * mm});
            skLineSegment(sketch, "E1145", {"start": v(-7.61, -0.33) * mm, "end": v(-7.54, -0.37) * mm});
            skLineSegment(sketch, "E1146", {"start": v(-7.54, -0.37) * mm, "end": v(-7.47, -0.41) * mm});
            skLineSegment(sketch, "E1147", {"start": v(-7.47, -0.41) * mm, "end": v(-7.4, -0.46) * mm});
            skLineSegment(sketch, "E1148", {"start": v(-7.4, -0.46) * mm, "end": v(-7.32, -0.5) * mm});
            skLineSegment(sketch, "E1149", {"start": v(-7.32, -0.5) * mm, "end": v(-7.24, -0.54) * mm});
            skLineSegment(sketch, "E1150", {"start": v(-7.24, -0.54) * mm, "end": v(-7.17, -0.58) * mm});
            skLineSegment(sketch, "E1151", {"start": v(-7.17, -0.58) * mm, "end": v(-7.1, -0.62) * mm});
            skLineSegment(sketch, "E1152", {"start": v(-7.1, -0.62) * mm, "end": v(-7.05, -0.65) * mm});
            skLineSegment(sketch, "E1153", {"start": v(-7.05, -0.65) * mm, "end": v(-7, -0.69) * mm});
            skLineSegment(sketch, "E1154", {"start": v(-7, -0.69) * mm, "end": v(-6.96, -0.72) * mm});
            skLineSegment(sketch, "E1155", {"start": v(-6.96, -0.72) * mm, "end": v(-6.93, -0.75) * mm});
            skLineSegment(sketch, "E1156", {"start": v(-6.93, -0.75) * mm, "end": v(-7.11, -0.89) * mm});
            skLineSegment(sketch, "E1157", {"start": v(-7.11, -0.89) * mm, "end": v(-7.32, -1.03) * mm});
            skLineSegment(sketch, "E1158", {"start": v(-7.32, -1.03) * mm, "end": v(-7.56, -1.16) * mm});
            skLineSegment(sketch, "E1159", {"start": v(-7.56, -1.16) * mm, "end": v(-7.81, -1.29) * mm});
            skLineSegment(sketch, "E1160", {"start": v(-7.81, -1.29) * mm, "end": v(-8.08, -1.4) * mm});
            skLineSegment(sketch, "E1161", {"start": v(-8.08, -1.4) * mm, "end": v(-8.36, -1.52) * mm});
            skLineSegment(sketch, "E1162", {"start": v(-8.36, -1.52) * mm, "end": v(-8.66, -1.63) * mm});
            skLineSegment(sketch, "E1163", {"start": v(-8.66, -1.63) * mm, "end": v(-8.95, -1.73) * mm});
            skLineSegment(sketch, "E1164", {"start": v(-8.95, -1.73) * mm, "end": v(-9.26, -1.82) * mm});
            skLineSegment(sketch, "E1165", {"start": v(-9.26, -1.82) * mm, "end": v(-9.56, -1.9) * mm});
            skLineSegment(sketch, "E1166", {"start": v(-9.56, -1.9) * mm, "end": v(-9.86, -1.97) * mm});
            skLineSegment(sketch, "E1167", {"start": v(-9.86, -1.97) * mm, "end": v(-10.15, -2.03) * mm});
            skLineSegment(sketch, "E1168", {"start": v(-10.15, -2.03) * mm, "end": v(-10.44, -2.07) * mm});
            skLineSegment(sketch, "E1169", {"start": v(-10.44, -2.07) * mm, "end": v(-10.7, -2.1) * mm});
            skLineSegment(sketch, "E1170", {"start": v(-10.7, -2.1) * mm, "end": v(-10.96, -2.13) * mm});
            skLineSegment(sketch, "E1171", {"start": v(-10.96, -2.13) * mm, "end": v(-11.2, -2.14) * mm});
            skLineSegment(sketch, "E1172", {"start": v(-11.2, -2.14) * mm, "end": v(-11.22, -2.14) * mm});
            skLineSegment(sketch, "E1173", {"start": v(-11.22, -2.14) * mm, "end": v(-11.25, -2.13) * mm});
            skLineSegment(sketch, "E1174", {"start": v(-11.25, -2.13) * mm, "end": v(-11.27, -2.13) * mm});
            skLineSegment(sketch, "E1175", {"start": v(-11.27, -2.13) * mm, "end": v(-11.29, -2.13) * mm});
            skLineSegment(sketch, "E1176", {"start": v(-11.29, -2.13) * mm, "end": v(-11.31, -2.13) * mm});
            skLineSegment(sketch, "E1177", {"start": v(-11.31, -2.13) * mm, "end": v(-11.33, -2.13) * mm});
            skLineSegment(sketch, "E1178", {"start": v(-11.33, -2.13) * mm, "end": v(-11.35, -2.13) * mm});
            skLineSegment(sketch, "E1179", {"start": v(-11.35, -2.13) * mm, "end": v(-11.37, -2.13) * mm});
            skLineSegment(sketch, "E1180", {"start": v(-11.37, -2.13) * mm, "end": v(-11.4, -2.13) * mm});
            skLineSegment(sketch, "E1181", {"start": v(-11.4, -2.13) * mm, "end": v(-11.42, -2.13) * mm});
            skLineSegment(sketch, "E1182", {"start": v(-11.42, -2.13) * mm, "end": v(-11.44, -2.13) * mm});
            skLineSegment(sketch, "E1183", {"start": v(-11.44, -2.13) * mm, "end": v(-11.46, -2.12) * mm});
            skLineSegment(sketch, "E1184", {"start": v(-11.46, -2.12) * mm, "end": v(-11.48, -2.12) * mm});
            skLineSegment(sketch, "E1185", {"start": v(-11.48, -2.12) * mm, "end": v(-11.5, -2.12) * mm});
            skLineSegment(sketch, "E1186", {"start": v(-11.5, -2.12) * mm, "end": v(-11.52, -2.12) * mm});
            skLineSegment(sketch, "E1187", {"start": v(-11.52, -2.12) * mm, "end": v(-11.54, -2.12) * mm});
            skLineSegment(sketch, "E1188", {"start": v(-11.54, -2.12) * mm, "end": v(-11.54, -2.16) * mm});
            skLineSegment(sketch, "E1189", {"start": v(-11.54, -2.16) * mm, "end": v(-11.54, -2.2) * mm});
            skLineSegment(sketch, "E1190", {"start": v(-11.54, -2.2) * mm, "end": v(-11.54, -2.24) * mm});
            skLineSegment(sketch, "E1191", {"start": v(-11.54, -2.24) * mm, "end": v(-11.54, -2.28) * mm});
            skLineSegment(sketch, "E1192", {"start": v(-11.54, -2.28) * mm, "end": v(-11.54, -2.32) * mm});
            skLineSegment(sketch, "E1193", {"start": v(-11.54, -2.32) * mm, "end": v(-11.54, -2.36) * mm});
            skLineSegment(sketch, "E1194", {"start": v(-11.54, -2.36) * mm, "end": v(-11.54, -2.4) * mm});
            skLineSegment(sketch, "E1195", {"start": v(-11.54, -2.4) * mm, "end": v(-11.54, -2.44) * mm});
            skLineSegment(sketch, "E1196", {"start": v(-11.54, -2.44) * mm, "end": v(-11.54, -2.48) * mm});
            skLineSegment(sketch, "E1197", {"start": v(-11.54, -2.48) * mm, "end": v(-11.54, -2.52) * mm});
            skLineSegment(sketch, "E1198", {"start": v(-11.54, -2.52) * mm, "end": v(-11.54, -2.56) * mm});
            skLineSegment(sketch, "E1199", {"start": v(-11.54, -2.56) * mm, "end": v(-11.54, -2.6) * mm});
            skLineSegment(sketch, "E1200", {"start": v(-11.54, -2.6) * mm, "end": v(-11.54, -2.64) * mm});
            skLineSegment(sketch, "E1201", {"start": v(-11.54, -2.64) * mm, "end": v(-11.54, -2.69) * mm});
            skLineSegment(sketch, "E1202", {"start": v(-11.54, -2.69) * mm, "end": v(-11.54, -2.73) * mm});
            skLineSegment(sketch, "E1203", {"start": v(-11.54, -2.73) * mm, "end": v(-11.54, -2.77) * mm});
            skLineSegment(sketch, "E1204", {"start": v(-11.54, -2.77) * mm, "end": v(-11.21, -2.77) * mm});
            skLineSegment(sketch, "E1205", {"start": v(-11.21, -2.77) * mm, "end": v(-10.89, -2.77) * mm});
            skLineSegment(sketch, "E1206", {"start": v(-10.89, -2.77) * mm, "end": v(-10.56, -2.77) * mm});
            skLineSegment(sketch, "E1207", {"start": v(-10.56, -2.77) * mm, "end": v(-10.23, -2.77) * mm});
            skLineSegment(sketch, "E1208", {"start": v(-10.23, -2.77) * mm, "end": v(-9.9, -2.77) * mm});
            skLineSegment(sketch, "E1209", {"start": v(-9.9, -2.77) * mm, "end": v(-9.57, -2.77) * mm});
            skLineSegment(sketch, "E1210", {"start": v(-9.57, -2.77) * mm, "end": v(-9.25, -2.77) * mm});
            skLineSegment(sketch, "E1211", {"start": v(-9.25, -2.77) * mm, "end": v(-8.92, -2.77) * mm});
            skLineSegment(sketch, "E1212", {"start": v(-8.92, -2.77) * mm, "end": v(-8.6, -2.77) * mm});
            skLineSegment(sketch, "E1213", {"start": v(-8.6, -2.77) * mm, "end": v(-8.26, -2.77) * mm});
            skLineSegment(sketch, "E1214", {"start": v(-8.26, -2.77) * mm, "end": v(-7.93, -2.77) * mm});
            skLineSegment(sketch, "E1215", {"start": v(-7.93, -2.77) * mm, "end": v(-7.6, -2.77) * mm});
            skLineSegment(sketch, "E1216", {"start": v(-7.6, -2.77) * mm, "end": v(-7.28, -2.77) * mm});
            skLineSegment(sketch, "E1217", {"start": v(-7.28, -2.77) * mm, "end": v(-6.95, -2.77) * mm});
            skLineSegment(sketch, "E1218", {"start": v(-6.95, -2.77) * mm, "end": v(-6.62, -2.77) * mm});
            skLineSegment(sketch, "E1219", {"start": v(-6.62, -2.77) * mm, "end": v(-6.3, -2.77) * mm});
            skLineSegment(sketch, "E1220", {"start": v(-6.3, -2.77) * mm, "end": v(-6.3, -2.42) * mm});
            skLineSegment(sketch, "E1221", {"start": v(-6.3, -2.42) * mm, "end": v(-6.3, -2.07) * mm});
            skLineSegment(sketch, "E1222", {"start": v(-6.3, -2.07) * mm, "end": v(-6.3, -1.73) * mm});
            skLineSegment(sketch, "E1223", {"start": v(-6.3, -1.73) * mm, "end": v(-6.3, -1.38) * mm});
            skLineSegment(sketch, "E1224", {"start": v(-6.3, -1.38) * mm, "end": v(-6.3, -1.04) * mm});
            skLineSegment(sketch, "E1225", {"start": v(-6.3, -1.04) * mm, "end": v(-6.3, -0.7) * mm});
            skLineSegment(sketch, "E1226", {"start": v(-6.3, -0.7) * mm, "end": v(-6.3, -0.35) * mm});
            skLineSegment(sketch, "E1227", {"start": v(-6.3, -0.35) * mm, "end": v(-6.3, 0) * mm});
            skLineSegment(sketch, "E1228", {"start": v(-6.3, 0) * mm, "end": v(-6.3, 0.35) * mm});
            skLineSegment(sketch, "E1229", {"start": v(-6.3, 0.35) * mm, "end": v(-6.3, 0.7) * mm});
            skLineSegment(sketch, "E1230", {"start": v(-6.3, 0.7) * mm, "end": v(-6.3, 1.04) * mm});
            skLineSegment(sketch, "E1231", {"start": v(-6.3, 1.04) * mm, "end": v(-6.3, 1.38) * mm});
            skLineSegment(sketch, "E1232", {"start": v(-6.3, 1.38) * mm, "end": v(-6.3, 1.73) * mm});
            skLineSegment(sketch, "E1233", {"start": v(-6.3, 1.73) * mm, "end": v(-6.3, 2.07) * mm});
            skLineSegment(sketch, "E1234", {"start": v(-6.3, 2.07) * mm, "end": v(-6.3, 2.42) * mm});
            skLineSegment(sketch, "E1235", {"start": v(-6.3, 2.42) * mm, "end": v(-6.3, 2.77) * mm});
            skLineSegment(sketch, "E1236", {"start": v(-6.3, 2.77) * mm, "end": v(-6.62, 2.77) * mm});
            skLineSegment(sketch, "E1237", {"start": v(-6.62, 2.77) * mm, "end": v(-6.95, 2.77) * mm});
            skLineSegment(sketch, "E1238", {"start": v(-6.95, 2.77) * mm, "end": v(-7.28, 2.77) * mm});
            skLineSegment(sketch, "E1239", {"start": v(-7.28, 2.77) * mm, "end": v(-7.6, 2.77) * mm});
            skLineSegment(sketch, "E1240", {"start": v(-7.6, 2.77) * mm, "end": v(-7.93, 2.77) * mm});
            skLineSegment(sketch, "E1241", {"start": v(-7.93, 2.77) * mm, "end": v(-8.26, 2.77) * mm});
            skLineSegment(sketch, "E1242", {"start": v(-8.26, 2.77) * mm, "end": v(-8.6, 2.77) * mm});
            skLineSegment(sketch, "E1243", {"start": v(-8.6, 2.77) * mm, "end": v(-8.92, 2.77) * mm});
            skLineSegment(sketch, "E1244", {"start": v(-8.92, 2.77) * mm, "end": v(-9.25, 2.77) * mm});
            skLineSegment(sketch, "E1245", {"start": v(-9.25, 2.77) * mm, "end": v(-9.57, 2.77) * mm});
            skLineSegment(sketch, "E1246", {"start": v(-9.57, 2.77) * mm, "end": v(-9.9, 2.77) * mm});
            skLineSegment(sketch, "E1247", {"start": v(-9.9, 2.77) * mm, "end": v(-10.23, 2.77) * mm});
            skLineSegment(sketch, "E1248", {"start": v(-10.23, 2.77) * mm, "end": v(-10.56, 2.77) * mm});
            skLineSegment(sketch, "E1249", {"start": v(-10.56, 2.77) * mm, "end": v(-10.89, 2.77) * mm});
            skLineSegment(sketch, "E1250", {"start": v(-10.89, 2.77) * mm, "end": v(-11.21, 2.77) * mm});
            skLineSegment(sketch, "E1251", {"start": v(-11.21, 2.77) * mm, "end": v(-11.54, 2.77) * mm});
            skLineSegment(sketch, "E1252", {"start": v(-11.54, -0.83) * mm, "end": v(-11.54, -0.86) * mm});
            skLineSegment(sketch, "E1253", {"start": v(-11.54, -0.86) * mm, "end": v(-11.54, -0.88) * mm});
            skLineSegment(sketch, "E1254", {"start": v(-11.54, -0.88) * mm, "end": v(-11.54, -0.9) * mm});
            skLineSegment(sketch, "E1255", {"start": v(-11.54, -0.9) * mm, "end": v(-11.54, -0.93) * mm});
            skLineSegment(sketch, "E1256", {"start": v(-11.54, -0.93) * mm, "end": v(-11.54, -0.96) * mm});
            skLineSegment(sketch, "E1257", {"start": v(-11.54, -0.96) * mm, "end": v(-11.54, -0.98) * mm});
            skLineSegment(sketch, "E1258", {"start": v(-11.54, -0.98) * mm, "end": v(-11.54, -1) * mm});
            skLineSegment(sketch, "E1259", {"start": v(-11.54, -1) * mm, "end": v(-11.54, -1.03) * mm});
            skLineSegment(sketch, "E1260", {"start": v(-11.54, -1.03) * mm, "end": v(-11.54, -1.05) * mm});
            skLineSegment(sketch, "E1261", {"start": v(-11.54, -1.05) * mm, "end": v(-11.54, -1.08) * mm});
            skLineSegment(sketch, "E1262", {"start": v(-11.54, -1.08) * mm, "end": v(-11.54, -1.1) * mm});
            skLineSegment(sketch, "E1263", {"start": v(-11.54, -1.1) * mm, "end": v(-11.54, -1.13) * mm});
            skLineSegment(sketch, "E1264", {"start": v(-11.54, -1.13) * mm, "end": v(-11.54, -1.15) * mm});
            skLineSegment(sketch, "E1265", {"start": v(-11.54, -1.15) * mm, "end": v(-11.54, -1.18) * mm});
            skLineSegment(sketch, "E1266", {"start": v(-11.54, -1.18) * mm, "end": v(-11.54, -1.2) * mm});
            skLineSegment(sketch, "E1267", {"start": v(-11.54, -1.2) * mm, "end": v(-11.54, -1.23) * mm});
            skLineSegment(sketch, "E1268", {"start": v(-11.54, -1.23) * mm, "end": v(-11.77, -1.17) * mm});
            skLineSegment(sketch, "E1269", {"start": v(-11.77, -1.17) * mm, "end": v(-11.98, -1.1) * mm});
            skLineSegment(sketch, "E1270", {"start": v(-11.98, -1.1) * mm, "end": v(-12.17, -1) * mm});
            skLineSegment(sketch, "E1271", {"start": v(-12.17, -1) * mm, "end": v(-12.34, -0.89) * mm});
            skLineSegment(sketch, "E1272", {"start": v(-12.34, -0.89) * mm, "end": v(-12.49, -0.77) * mm});
            skLineSegment(sketch, "E1273", {"start": v(-12.49, -0.77) * mm, "end": v(-12.62, -0.63) * mm});
            skLineSegment(sketch, "E1274", {"start": v(-12.62, -0.63) * mm, "end": v(-12.74, -0.5) * mm});
            skLineSegment(sketch, "E1275", {"start": v(-12.74, -0.5) * mm, "end": v(-12.84, -0.36) * mm});
            skLineSegment(sketch, "E1276", {"start": v(-12.84, -0.36) * mm, "end": v(-12.92, -0.23) * mm});
            skLineSegment(sketch, "E1277", {"start": v(-12.92, -0.23) * mm, "end": v(-13, -0.1) * mm});
            skLineSegment(sketch, "E1278", {"start": v(-13, -0.1) * mm, "end": v(-13.05, 0.01) * mm});
            skLineSegment(sketch, "E1279", {"start": v(-13.05, 0.01) * mm, "end": v(-13.1, 0.12) * mm});
            skLineSegment(sketch, "E1280", {"start": v(-13.1, 0.12) * mm, "end": v(-13.13, 0.2) * mm});
            skLineSegment(sketch, "E1281", {"start": v(-13.13, 0.2) * mm, "end": v(-13.16, 0.27) * mm});
            skLineSegment(sketch, "E1282", {"start": v(-13.16, 0.27) * mm, "end": v(-13.17, 0.31) * mm});
            skLineSegment(sketch, "E1283", {"start": v(-13.17, 0.31) * mm, "end": v(-13.17, 0.33) * mm});
            skLineSegment(sketch, "E1284", {"start": v(-13.17, 0.33) * mm, "end": v(-13.17, 0.33) * mm});
            skLineSegment(sketch, "E1285", {"start": v(-13.17, 0.33) * mm, "end": v(-13.15, 0.36) * mm});
            skLineSegment(sketch, "E1286", {"start": v(-13.15, 0.36) * mm, "end": v(-13.11, 0.4) * mm});
            skLineSegment(sketch, "E1287", {"start": v(-13.11, 0.4) * mm, "end": v(-13.06, 0.43) * mm});
            skLineSegment(sketch, "E1288", {"start": v(-13.06, 0.43) * mm, "end": v(-13, 0.49) * mm});
            skLineSegment(sketch, "E1289", {"start": v(-13, 0.49) * mm, "end": v(-12.93, 0.55) * mm});
            skLineSegment(sketch, "E1290", {"start": v(-12.93, 0.55) * mm, "end": v(-12.84, 0.61) * mm});
            skLineSegment(sketch, "E1291", {"start": v(-12.84, 0.61) * mm, "end": v(-12.74, 0.68) * mm});
            skLineSegment(sketch, "E1292", {"start": v(-12.74, 0.68) * mm, "end": v(-12.63, 0.75) * mm});
            skLineSegment(sketch, "E1293", {"start": v(-12.63, 0.75) * mm, "end": v(-12.5, 0.82) * mm});
            skLineSegment(sketch, "E1294", {"start": v(-12.5, 0.82) * mm, "end": v(-12.37, 0.88) * mm});
            skLineSegment(sketch, "E1295", {"start": v(-12.37, 0.88) * mm, "end": v(-12.23, 0.95) * mm});
            skLineSegment(sketch, "E1296", {"start": v(-12.23, 0.95) * mm, "end": v(-12.07, 1) * mm});
            skLineSegment(sketch, "E1297", {"start": v(-12.07, 1) * mm, "end": v(-11.9, 1.05) * mm});
            skLineSegment(sketch, "E1298", {"start": v(-11.9, 1.05) * mm, "end": v(-11.73, 1.09) * mm});
            skLineSegment(sketch, "E1299", {"start": v(-11.73, 1.09) * mm, "end": v(-11.54, 1.12) * mm});
            skLineSegment(sketch, "E1300", {"start": v(-11.54, 1.12) * mm, "end": v(-11.54, 1.09) * mm});
            skLineSegment(sketch, "E1301", {"start": v(-11.54, 1.09) * mm, "end": v(-11.54, 1.06) * mm});
            skLineSegment(sketch, "E1302", {"start": v(-11.54, 1.06) * mm, "end": v(-11.54, 1.03) * mm});
            skLineSegment(sketch, "E1303", {"start": v(-11.54, 1.03) * mm, "end": v(-11.54, 1) * mm});
            skLineSegment(sketch, "E1304", {"start": v(-11.54, 1) * mm, "end": v(-11.54, 0.98) * mm});
            skLineSegment(sketch, "E1305", {"start": v(-11.54, 0.98) * mm, "end": v(-11.54, 0.95) * mm});
            skLineSegment(sketch, "E1306", {"start": v(-11.54, 0.95) * mm, "end": v(-11.54, 0.93) * mm});
            skLineSegment(sketch, "E1307", {"start": v(-11.54, 0.93) * mm, "end": v(-11.54, 0.9) * mm});
            skLineSegment(sketch, "E1308", {"start": v(-11.54, 0.9) * mm, "end": v(-11.54, 0.87) * mm});
            skLineSegment(sketch, "E1309", {"start": v(-11.54, 0.87) * mm, "end": v(-11.54, 0.85) * mm});
            skLineSegment(sketch, "E1310", {"start": v(-11.54, 0.85) * mm, "end": v(-11.54, 0.82) * mm});
            skLineSegment(sketch, "E1311", {"start": v(-11.54, 0.82) * mm, "end": v(-11.54, 0.8) * mm});
            skLineSegment(sketch, "E1312", {"start": v(-11.54, 0.8) * mm, "end": v(-11.54, 0.76) * mm});
            skLineSegment(sketch, "E1313", {"start": v(-11.54, 0.76) * mm, "end": v(-11.54, 0.74) * mm});
            skLineSegment(sketch, "E1314", {"start": v(-11.54, 0.74) * mm, "end": v(-11.54, 0.71) * mm});
            skLineSegment(sketch, "E1315", {"start": v(-11.54, 0.71) * mm, "end": v(-11.54, 0.68) * mm});
            skLineSegment(sketch, "E1316", {"start": v(-11.54, 0.68) * mm, "end": v(-11.54, 0.68) * mm});
            skLineSegment(sketch, "E1317", {"start": v(-11.54, 0.68) * mm, "end": v(-11.64, 0.69) * mm});
            skLineSegment(sketch, "E1318", {"start": v(-11.64, 0.69) * mm, "end": v(-11.74, 0.68) * mm});
            skLineSegment(sketch, "E1319", {"start": v(-11.74, 0.68) * mm, "end": v(-11.83, 0.67) * mm});
            skLineSegment(sketch, "E1320", {"start": v(-11.83, 0.67) * mm, "end": v(-11.92, 0.64) * mm});
            skLineSegment(sketch, "E1321", {"start": v(-11.92, 0.64) * mm, "end": v(-12, 0.61) * mm});
            skLineSegment(sketch, "E1322", {"start": v(-12, 0.61) * mm, "end": v(-12.08, 0.57) * mm});
            skLineSegment(sketch, "E1323", {"start": v(-12.08, 0.57) * mm, "end": v(-12.15, 0.53) * mm});
            skLineSegment(sketch, "E1324", {"start": v(-12.15, 0.53) * mm, "end": v(-12.22, 0.49) * mm});
            skLineSegment(sketch, "E1325", {"start": v(-12.22, 0.49) * mm, "end": v(-12.28, 0.45) * mm});
            skLineSegment(sketch, "E1326", {"start": v(-12.28, 0.45) * mm, "end": v(-12.34, 0.4) * mm});
            skLineSegment(sketch, "E1327", {"start": v(-12.34, 0.4) * mm, "end": v(-12.38, 0.36) * mm});
            skLineSegment(sketch, "E1328", {"start": v(-12.38, 0.36) * mm, "end": v(-12.42, 0.33) * mm});
            skLineSegment(sketch, "E1329", {"start": v(-12.42, 0.33) * mm, "end": v(-12.45, 0.3) * mm});
            skLineSegment(sketch, "E1330", {"start": v(-12.45, 0.3) * mm, "end": v(-12.48, 0.27) * mm});
            skLineSegment(sketch, "E1331", {"start": v(-12.48, 0.27) * mm, "end": v(-12.5, 0.25) * mm});
            skLineSegment(sketch, "E1332", {"start": v(-12.5, 0.25) * mm, "end": v(-12.5, 0.25) * mm});
            skLineSegment(sketch, "E1333", {"start": v(-12.5, 0.25) * mm, "end": v(-12.5, 0.24) * mm});
            skLineSegment(sketch, "E1334", {"start": v(-12.5, 0.24) * mm, "end": v(-12.48, 0.21) * mm});
            skLineSegment(sketch, "E1335", {"start": v(-12.48, 0.21) * mm, "end": v(-12.47, 0.17) * mm});
            skLineSegment(sketch, "E1336", {"start": v(-12.47, 0.17) * mm, "end": v(-12.45, 0.11) * mm});
            skLineSegment(sketch, "E1337", {"start": v(-12.45, 0.11) * mm, "end": v(-12.42, 0.05) * mm});
            skLineSegment(sketch, "E1338", {"start": v(-12.42, 0.05) * mm, "end": v(-12.38, -0.03) * mm});
            skLineSegment(sketch, "E1339", {"start": v(-12.38, -0.03) * mm, "end": v(-12.34, -0.11) * mm});
            skLineSegment(sketch, "E1340", {"start": v(-12.34, -0.11) * mm, "end": v(-12.29, -0.2) * mm});
            skLineSegment(sketch, "E1341", {"start": v(-12.29, -0.2) * mm, "end": v(-12.23, -0.3) * mm});
            skLineSegment(sketch, "E1342", {"start": v(-12.23, -0.3) * mm, "end": v(-12.16, -0.38) * mm});
            skLineSegment(sketch, "E1343", {"start": v(-12.16, -0.38) * mm, "end": v(-12.08, -0.47) * mm});
            skLineSegment(sketch, "E1344", {"start": v(-12.08, -0.47) * mm, "end": v(-12, -0.56) * mm});
            skLineSegment(sketch, "E1345", {"start": v(-12, -0.56) * mm, "end": v(-11.9, -0.64) * mm});
            skLineSegment(sketch, "E1346", {"start": v(-11.9, -0.64) * mm, "end": v(-11.8, -0.72) * mm});
            skLineSegment(sketch, "E1347", {"start": v(-11.8, -0.72) * mm, "end": v(-11.67, -0.78) * mm});
            skLineSegment(sketch, "E1348", {"start": v(-11.67, -0.78) * mm, "end": v(-11.54, -0.83) * mm});
            skLineSegment(sketch, "E1349", {"start": v(-13.81, 0.38) * mm, "end": v(-13.8, 0.4) * mm});
            skLineSegment(sketch, "E1350", {"start": v(-13.8, 0.4) * mm, "end": v(-13.78, 0.43) * mm});
            skLineSegment(sketch, "E1351", {"start": v(-13.78, 0.43) * mm, "end": v(-13.73, 0.49) * mm});
            skLineSegment(sketch, "E1352", {"start": v(-13.73, 0.49) * mm, "end": v(-13.67, 0.56) * mm});
            skLineSegment(sketch, "E1353", {"start": v(-13.67, 0.56) * mm, "end": v(-13.59, 0.65) * mm});
            skLineSegment(sketch, "E1354", {"start": v(-13.59, 0.65) * mm, "end": v(-13.5, 0.74) * mm});
            skLineSegment(sketch, "E1355", {"start": v(-13.5, 0.74) * mm, "end": v(-13.38, 0.85) * mm});
            skLineSegment(sketch, "E1356", {"start": v(-13.38, 0.85) * mm, "end": v(-13.24, 0.96) * mm});
            skLineSegment(sketch, "E1357", {"start": v(-13.24, 0.96) * mm, "end": v(-13.1, 1.07) * mm});
            skLineSegment(sketch, "E1358", {"start": v(-13.1, 1.07) * mm, "end": v(-12.92, 1.17) * mm});
            skLineSegment(sketch, "E1359", {"start": v(-12.92, 1.17) * mm, "end": v(-12.74, 1.28) * mm});
            skLineSegment(sketch, "E1360", {"start": v(-12.74, 1.28) * mm, "end": v(-12.53, 1.37) * mm});
            skLineSegment(sketch, "E1361", {"start": v(-12.53, 1.37) * mm, "end": v(-12.31, 1.46) * mm});
            skLineSegment(sketch, "E1362", {"start": v(-12.31, 1.46) * mm, "end": v(-12.07, 1.53) * mm});
            skLineSegment(sketch, "E1363", {"start": v(-12.07, 1.53) * mm, "end": v(-11.82, 1.58) * mm});
            skLineSegment(sketch, "E1364", {"start": v(-11.82, 1.58) * mm, "end": v(-11.54, 1.61) * mm});
            skLineSegment(sketch, "E1365", {"start": v(-11.54, 1.61) * mm, "end": v(-11.54, 1.64) * mm});
            skLineSegment(sketch, "E1366", {"start": v(-11.54, 1.64) * mm, "end": v(-11.54, 1.67) * mm});
            skLineSegment(sketch, "E1367", {"start": v(-11.54, 1.67) * mm, "end": v(-11.54, 1.7) * mm});
            skLineSegment(sketch, "E1368", {"start": v(-11.54, 1.7) * mm, "end": v(-11.54, 1.72) * mm});
            skLineSegment(sketch, "E1369", {"start": v(-11.54, 1.72) * mm, "end": v(-11.54, 1.74) * mm});
            skLineSegment(sketch, "E1370", {"start": v(-11.54, 1.74) * mm, "end": v(-11.54, 1.77) * mm});
            skLineSegment(sketch, "E1371", {"start": v(-11.54, 1.77) * mm, "end": v(-11.54, 1.8) * mm});
            skLineSegment(sketch, "E1372", {"start": v(-11.54, 1.8) * mm, "end": v(-11.54, 1.82) * mm});
            skLineSegment(sketch, "E1373", {"start": v(-11.54, 1.82) * mm, "end": v(-11.54, 1.84) * mm});
            skLineSegment(sketch, "E1374", {"start": v(-11.54, 1.84) * mm, "end": v(-11.54, 1.87) * mm});
            skLineSegment(sketch, "E1375", {"start": v(-11.54, 1.87) * mm, "end": v(-11.54, 1.9) * mm});
            skLineSegment(sketch, "E1376", {"start": v(-11.54, 1.9) * mm, "end": v(-11.54, 1.92) * mm});
            skLineSegment(sketch, "E1377", {"start": v(-11.54, 1.92) * mm, "end": v(-11.54, 1.94) * mm});
            skLineSegment(sketch, "E1378", {"start": v(-11.54, 1.94) * mm, "end": v(-11.54, 1.97) * mm});
            skLineSegment(sketch, "E1379", {"start": v(-11.54, 1.97) * mm, "end": v(-11.54, 2) * mm});
            skLineSegment(sketch, "E1380", {"start": v(-11.54, 2) * mm, "end": v(-11.54, 2.02) * mm});
            skLineSegment(sketch, "E1381", {"start": v(-11.54, 2.02) * mm, "end": v(-11.85, 1.98) * mm});
            skLineSegment(sketch, "E1382", {"start": v(-11.85, 1.98) * mm, "end": v(-12.16, 1.91) * mm});
            skLineSegment(sketch, "E1383", {"start": v(-12.16, 1.91) * mm, "end": v(-12.45, 1.83) * mm});
            skLineSegment(sketch, "E1384", {"start": v(-12.45, 1.83) * mm, "end": v(-12.74, 1.72) * mm});
            skLineSegment(sketch, "E1385", {"start": v(-12.74, 1.72) * mm, "end": v(-13, 1.6) * mm});
            skLineSegment(sketch, "E1386", {"start": v(-13, 1.6) * mm, "end": v(-13.27, 1.47) * mm});
            skLineSegment(sketch, "E1387", {"start": v(-13.27, 1.47) * mm, "end": v(-13.5, 1.33) * mm});
            skLineSegment(sketch, "E1388", {"start": v(-13.5, 1.33) * mm, "end": v(-13.73, 1.2) * mm});
            skLineSegment(sketch, "E1389", {"start": v(-13.73, 1.2) * mm, "end": v(-13.94, 1.06) * mm});
            skLineSegment(sketch, "E1390", {"start": v(-13.94, 1.06) * mm, "end": v(-14.12, 0.92) * mm});
            skLineSegment(sketch, "E1391", {"start": v(-14.12, 0.92) * mm, "end": v(-14.28, 0.8) * mm});
            skLineSegment(sketch, "E1392", {"start": v(-14.28, 0.8) * mm, "end": v(-14.41, 0.7) * mm});
            skLineSegment(sketch, "E1393", {"start": v(-14.41, 0.7) * mm, "end": v(-14.52, 0.6) * mm});
            skLineSegment(sketch, "E1394", {"start": v(-14.52, 0.6) * mm, "end": v(-14.6, 0.53) * mm});
            skLineSegment(sketch, "E1395", {"start": v(-14.6, 0.53) * mm, "end": v(-14.65, 0.49) * mm});
            skLineSegment(sketch, "E1396", {"start": v(-14.65, 0.49) * mm, "end": v(-14.67, 0.47) * mm});
            skLineSegment(sketch, "E1397", {"start": v(-14.67, 0.47) * mm, "end": v(-14.66, 0.44) * mm});
            skLineSegment(sketch, "E1398", {"start": v(-14.66, 0.44) * mm, "end": v(-14.63, 0.37) * mm});
            skLineSegment(sketch, "E1399", {"start": v(-14.63, 0.37) * mm, "end": v(-14.57, 0.25) * mm});
            skLineSegment(sketch, "E1400", {"start": v(-14.57, 0.25) * mm, "end": v(-14.5, 0.1) * mm});
            skLineSegment(sketch, "E1401", {"start": v(-14.5, 0.1) * mm, "end": v(-14.4, -0.09) * mm});
            skLineSegment(sketch, "E1402", {"start": v(-14.4, -0.09) * mm, "end": v(-14.28, -0.3) * mm});
            skLineSegment(sketch, "E1403", {"start": v(-14.28, -0.3) * mm, "end": v(-14.14, -0.51) * mm});
            skLineSegment(sketch, "E1404", {"start": v(-14.14, -0.51) * mm, "end": v(-13.97, -0.74) * mm});
            skLineSegment(sketch, "E1405", {"start": v(-13.97, -0.74) * mm, "end": v(-13.77, -0.97) * mm});
            skLineSegment(sketch, "E1406", {"start": v(-13.77, -0.97) * mm, "end": v(-13.54, -1.2) * mm});
            skLineSegment(sketch, "E1407", {"start": v(-13.54, -1.2) * mm, "end": v(-13.29, -1.42) * mm});
            skLineSegment(sketch, "E1408", {"start": v(-13.29, -1.42) * mm, "end": v(-13, -1.62) * mm});
            skLineSegment(sketch, "E1409", {"start": v(-13, -1.62) * mm, "end": v(-12.69, -1.8) * mm});
            skLineSegment(sketch, "E1410", {"start": v(-12.69, -1.8) * mm, "end": v(-12.34, -1.94) * mm});
            skLineSegment(sketch, "E1411", {"start": v(-12.34, -1.94) * mm, "end": v(-11.96, -2.05) * mm});
            skLineSegment(sketch, "E1412", {"start": v(-11.96, -2.05) * mm, "end": v(-11.54, -2.12) * mm});
            skLineSegment(sketch, "E1413", {"start": v(-11.54, -2.12) * mm, "end": v(-11.54, -2.1) * mm});
            skLineSegment(sketch, "E1414", {"start": v(-11.54, -2.1) * mm, "end": v(-11.54, -2.06) * mm});
            skLineSegment(sketch, "E1415", {"start": v(-11.54, -2.06) * mm, "end": v(-11.54, -2.04) * mm});
            skLineSegment(sketch, "E1416", {"start": v(-11.54, -2.04) * mm, "end": v(-11.54, -2) * mm});
            skLineSegment(sketch, "E1417", {"start": v(-11.54, -2) * mm, "end": v(-11.54, -1.98) * mm});
            skLineSegment(sketch, "E1418", {"start": v(-11.54, -1.98) * mm, "end": v(-11.54, -1.96) * mm});
            skLineSegment(sketch, "E1419", {"start": v(-11.54, -1.96) * mm, "end": v(-11.54, -1.93) * mm});
            skLineSegment(sketch, "E1420", {"start": v(-11.54, -1.93) * mm, "end": v(-11.54, -1.9) * mm});
            skLineSegment(sketch, "E1421", {"start": v(-11.54, -1.9) * mm, "end": v(-11.54, -1.88) * mm});
            skLineSegment(sketch, "E1422", {"start": v(-11.54, -1.88) * mm, "end": v(-11.54, -1.85) * mm});
            skLineSegment(sketch, "E1423", {"start": v(-11.54, -1.85) * mm, "end": v(-11.54, -1.82) * mm});
            skLineSegment(sketch, "E1424", {"start": v(-11.54, -1.82) * mm, "end": v(-11.54, -1.8) * mm});
            skLineSegment(sketch, "E1425", {"start": v(-11.54, -1.8) * mm, "end": v(-11.54, -1.77) * mm});
            skLineSegment(sketch, "E1426", {"start": v(-11.54, -1.77) * mm, "end": v(-11.54, -1.74) * mm});
            skLineSegment(sketch, "E1427", {"start": v(-11.54, -1.74) * mm, "end": v(-11.54, -1.71) * mm});
            skLineSegment(sketch, "E1428", {"start": v(-11.54, -1.71) * mm, "end": v(-11.54, -1.69) * mm});
            skLineSegment(sketch, "E1429", {"start": v(-11.54, -1.69) * mm, "end": v(-11.85, -1.63) * mm});
            skLineSegment(sketch, "E1430", {"start": v(-11.85, -1.63) * mm, "end": v(-12.13, -1.54) * mm});
            skLineSegment(sketch, "E1431", {"start": v(-12.13, -1.54) * mm, "end": v(-12.38, -1.42) * mm});
            skLineSegment(sketch, "E1432", {"start": v(-12.38, -1.42) * mm, "end": v(-12.6, -1.27) * mm});
            skLineSegment(sketch, "E1433", {"start": v(-12.6, -1.27) * mm, "end": v(-12.82, -1.11) * mm});
            skLineSegment(sketch, "E1434", {"start": v(-12.82, -1.11) * mm, "end": v(-13, -0.94) * mm});
            skLineSegment(sketch, "E1435", {"start": v(-13, -0.94) * mm, "end": v(-13.17, -0.76) * mm});
            skLineSegment(sketch, "E1436", {"start": v(-13.17, -0.76) * mm, "end": v(-13.31, -0.57) * mm});
            skLineSegment(sketch, "E1437", {"start": v(-13.31, -0.57) * mm, "end": v(-13.43, -0.39) * mm});
            skLineSegment(sketch, "E1438", {"start": v(-13.43, -0.39) * mm, "end": v(-13.54, -0.22) * mm});
            skLineSegment(sketch, "E1439", {"start": v(-13.54, -0.22) * mm, "end": v(-13.62, -0.05) * mm});
            skLineSegment(sketch, "E1440", {"start": v(-13.62, -0.05) * mm, "end": v(-13.7, 0.1) * mm});
            skLineSegment(sketch, "E1441", {"start": v(-13.7, 0.1) * mm, "end": v(-13.75, 0.21) * mm});
            skLineSegment(sketch, "E1442", {"start": v(-13.75, 0.21) * mm, "end": v(-13.78, 0.3) * mm});
            skLineSegment(sketch, "E1443", {"start": v(-13.78, 0.3) * mm, "end": v(-13.8, 0.36) * mm});
            skLineSegment(sketch, "E1444", {"start": v(-13.8, 0.36) * mm, "end": v(-13.81, 0.38) * mm});
            skSolve(sketch);
        }
        {
            var Q0;
            Q0=makeQuery(id+"F0.imprint","IMPRINT",FACE,{"disambiguationData":[TD([[makeQuery(id+"F0.imprint","IMPRINT",EDGE,{"derivedFrom":sQuery(id+"F0.wireOp",EDGE,"E1012")}),1.0]])]});
            var Q1;
            Q1=makeQuery(id+"F0.imprint","IMPRINT",FACE,{"disambiguationData":[TD([[makeQuery(id+"F0.imprint","IMPRINT",EDGE,{"derivedFrom":sQuery(id+"F0.wireOp",EDGE,"E852")}),-1.0]])]});
            var Q2;
            Q2=makeQuery(id+"F0.imprint","IMPRINT",FACE,{"disambiguationData":[TD([[makeQuery(id+"F0.imprint","IMPRINT",EDGE,{"derivedFrom":sQuery(id+"F0.wireOp",EDGE,"E1252")}),-1.0]])]});
            var Q3;
            Q3=makeQuery(id+"F0.imprint","IMPRINT",FACE,{"disambiguationData":[TD([[makeQuery(id+"F0.imprint","IMPRINT",EDGE,{"derivedFrom":sQuery(id+"F0.wireOp",EDGE,"E1349")}),1.0]])]});
            var Q4;
            Q4=makeQuery(id+"F0.imprint","IMPRINT",FACE,{"disambiguationData":[TD([[makeQuery(id+"F0.imprint","IMPRINT",EDGE,{"derivedFrom":sQuery(id+"F0.wireOp",EDGE,"E128")}),1.0]])]});
            var Q5;
            Q5=makeQuery(id+"F0.imprint","IMPRINT",FACE,{"disambiguationData":[TD([[makeQuery(id+"F0.imprint","IMPRINT",EDGE,{"derivedFrom":sQuery(id+"F0.wireOp",EDGE,"E496")}),1.0]])]});
            var Q6;
            Q6=makeQuery(id+"F0.imprint","IMPRINT",FACE,{"disambiguationData":[TD([[makeQuery(id+"F0.imprint","IMPRINT",EDGE,{"derivedFrom":sQuery(id+"F0.wireOp",EDGE,"E64")}),1.0]])]});
            var Q7;
            Q7=makeQuery(id+"F0.imprint","IMPRINT",FACE,{"disambiguationData":[TD([[makeQuery(id+"F0.imprint","IMPRINT",EDGE,{"derivedFrom":sQuery(id+"F0.wireOp",EDGE,"E304")}),1.0]])]});
            var Q8;
            Q8=makeQuery(id+"F0.imprint","IMPRINT",FACE,{"disambiguationData":[TD([[makeQuery(id+"F0.imprint","IMPRINT",EDGE,{"derivedFrom":sQuery(id+"F0.wireOp",EDGE,"E608")}),1.0]])]});
            var Q9;
            Q9=makeQuery(id+"F0.imprint","IMPRINT",FACE,{"disambiguationData":[TD([[makeQuery(id+"F0.imprint","IMPRINT",EDGE,{"derivedFrom":sQuery(id+"F0.wireOp",EDGE,"E672")}),1.0]])]});
            var Q10;
            Q10=makeQuery(id+"F0.imprint","IMPRINT",FACE,{"disambiguationData":[TD([[makeQuery(id+"F0.imprint","IMPRINT",EDGE,{"derivedFrom":sQuery(id+"F0.wireOp",EDGE,"E0")}),1.0]])]});
            extrude(context, id + "F1", {"entities" : qUnion([Q0, Q1, Q2, Q3, Q4, Q5, Q6, Q7, Q8, Q9, Q10]), "depth" : 2 * mm, "offsetDistance" : 25 * mm});
        }
        {
            var Q0;
            Q0=makeQuery(id+"F0.imprint","IMPRINT",FACE,{"disambiguationData":[TD([[makeQuery(id+"F0.imprint","IMPRINT",EDGE,{"derivedFrom":sQuery(id+"F0.wireOp",EDGE,"E0")}),-1.0]])]});
            var Q1;
            Q1=makeQuery(id+"F0.imprint","IMPRINT",FACE,{"disambiguationData":[TD([[makeQuery(id+"F0.imprint","IMPRINT",EDGE,{"derivedFrom":sQuery(id+"F0.wireOp",EDGE,"E1349")}),1.0]])]});
            var Q2;
            Q2=makeQuery(id+"F0.imprint","IMPRINT",FACE,{"disambiguationData":[TD([[makeQuery(id+"F0.imprint","IMPRINT",EDGE,{"derivedFrom":sQuery(id+"F0.wireOp",EDGE,"E852")}),1.0]])]});
            var Q3;
            Q3=makeQuery(id+"F0.imprint","IMPRINT",FACE,{"disambiguationData":[TD([[makeQuery(id+"F0.imprint","IMPRINT",EDGE,{"derivedFrom":sQuery(id+"F0.wireOp",EDGE,"E1252")}),-1.0]])]});
            var Q4;
            Q4=makeQuery(id+"F0.imprint","IMPRINT",FACE,{"disambiguationData":[TD([[makeQuery(id+"F0.imprint","IMPRINT",EDGE,{"derivedFrom":sQuery(id+"F0.wireOp",EDGE,"E932")}),1.0]])]});
            var Q5;
            Q5=makeQuery(id+"F0.imprint","IMPRINT",FACE,{"disambiguationData":[TD([[makeQuery(id+"F0.imprint","IMPRINT",EDGE,{"derivedFrom":sQuery(id+"F0.wireOp",EDGE,"E852")}),-1.0]])]});
            var Q6;
            Q6=makeQuery(id+"F0.imprint","IMPRINT",FACE,{"disambiguationData":[TD([[makeQuery(id+"F0.imprint","IMPRINT",EDGE,{"derivedFrom":sQuery(id+"F0.wireOp",EDGE,"E868")}),1.0]])]});
            var Q7;
            Q7=makeQuery(id+"F0.imprint","IMPRINT",FACE,{"disambiguationData":[TD([[makeQuery(id+"F0.imprint","IMPRINT",EDGE,{"derivedFrom":sQuery(id+"F0.wireOp",EDGE,"E948")}),1.0]])]});
            var Q8;
            Q8=makeQuery(id+"F0.imprint","IMPRINT",FACE,{"disambiguationData":[TD([[makeQuery(id+"F0.imprint","IMPRINT",EDGE,{"derivedFrom":sQuery(id+"F0.wireOp",EDGE,"E1012")}),1.0]])]});
            var Q9;
            Q9=makeQuery(id+"F0.imprint","IMPRINT",FACE,{"disambiguationData":[TD([[makeQuery(id+"F0.imprint","IMPRINT",EDGE,{"derivedFrom":sQuery(id+"F0.wireOp",EDGE,"E1108")}),-1.0]])]});
            var Q10;
            Q10=makeQuery(id+"F0.imprint","IMPRINT",FACE,{"disambiguationData":[TD([[makeQuery(id+"F0.imprint","IMPRINT",EDGE,{"derivedFrom":sQuery(id+"F0.wireOp",EDGE,"E496")}),1.0]])]});
            var Q11;
            Q11=makeQuery(id+"F0.imprint","IMPRINT",FACE,{"disambiguationData":[TD([[makeQuery(id+"F0.imprint","IMPRINT",EDGE,{"derivedFrom":sQuery(id+"F0.wireOp",EDGE,"E128")}),1.0]])]});
            var Q12;
            Q12=makeQuery(id+"F0.imprint","IMPRINT",FACE,{"disambiguationData":[TD([[makeQuery(id+"F0.imprint","IMPRINT",EDGE,{"derivedFrom":sQuery(id+"F0.wireOp",EDGE,"E64")}),1.0]])]});
            var Q13;
            Q13=makeQuery(id+"F0.imprint","IMPRINT",FACE,{"disambiguationData":[TD([[makeQuery(id+"F0.imprint","IMPRINT",EDGE,{"derivedFrom":sQuery(id+"F0.wireOp",EDGE,"E304")}),1.0]])]});
            var Q14;
            Q14=makeQuery(id+"F0.imprint","IMPRINT",FACE,{"disambiguationData":[TD([[makeQuery(id+"F0.imprint","IMPRINT",EDGE,{"derivedFrom":sQuery(id+"F0.wireOp",EDGE,"E416")}),-1.0]])]});
            var Q15;
            Q15=makeQuery(id+"F0.imprint","IMPRINT",FACE,{"disambiguationData":[TD([[makeQuery(id+"F0.imprint","IMPRINT",EDGE,{"derivedFrom":sQuery(id+"F0.wireOp",EDGE,"E608")}),1.0]])]});
            var Q16;
            Q16=makeQuery(id+"F0.imprint","IMPRINT",FACE,{"disambiguationData":[TD([[makeQuery(id+"F0.imprint","IMPRINT",EDGE,{"derivedFrom":sQuery(id+"F0.wireOp",EDGE,"E672")}),1.0]])]});
            var Q17;
            Q17=makeQuery(id+"F0.imprint","IMPRINT",FACE,{"disambiguationData":[TD([[makeQuery(id+"F0.imprint","IMPRINT",EDGE,{"derivedFrom":sQuery(id+"F0.wireOp",EDGE,"E800")}),-1.0]])]});
            var Q18;
            Q18=makeQuery(id+"F0.imprint","IMPRINT",FACE,{"disambiguationData":[TD([[makeQuery(id+"F0.imprint","IMPRINT",EDGE,{"derivedFrom":sQuery(id+"F0.wireOp",EDGE,"E0")}),1.0]])]});
            extrude(context, id + "F2", {"entities" : qUnion([Q0, Q1, Q2, Q3, Q4, Q5, Q6, Q7, Q8, Q9, Q10, Q11, Q12, Q13, Q14, Q15, Q16, Q17, Q18]), "oppositeDirection" : true, "depth" : 0.5 * mm, "offsetDistance" : 25 * mm});
        }
    });
